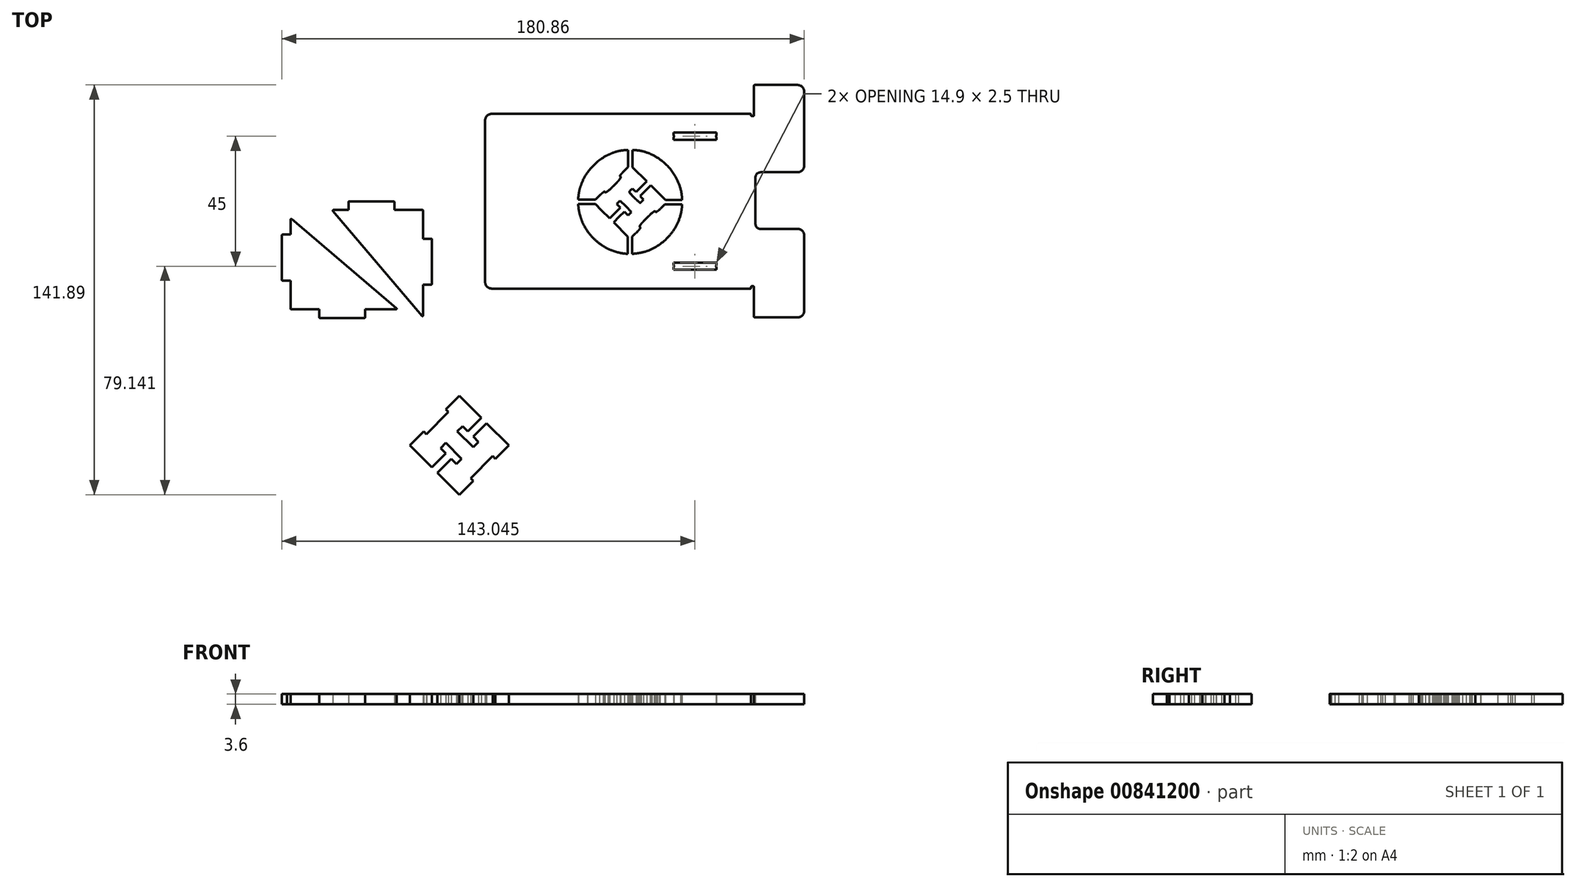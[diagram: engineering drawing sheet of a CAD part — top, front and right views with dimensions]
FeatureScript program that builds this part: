
annotation { "Feature Type Name" : "Feature", "Feature Type Description" : "" }
export const myFeature = defineFeature(function(context is Context, id is Id, definition is map)
    precondition{}
    {
        {
            assignVariable(context, id + "F0", {"name" : "Thickness", "anyValue" : 3.6});
        }
        {
            var Q0;
            Q0=qCreatedBy(makeId("Top.planeOp"),FACE);
            var sketch = newSketch(context, id + "F1", { "sketchPlane" : qUnion([Q0])});
            skLineSegment(sketch, "E0", {"start": v(-51.55, -47.18) * mm, "end": v(-51.61, -46.89) * mm});
            skArc(sketch, "E1", {"start": v(-51.61, -46.89) * mm, "mid": v(-51.65, -46.7) * mm, "end": v(-51.68, -46.5) * mm});
            skArc(sketch, "E2", {"start": v(-51.68, -46.5) * mm, "mid": v(-51.8, -45.73) * mm, "end": v(-51.89, -44.94) * mm});
            skArc(sketch, "E3", {"start": v(-51.89, -44.94) * mm, "mid": v(-51.9, -44.72) * mm, "end": v(-51.93, -44.5) * mm});
            skArc(sketch, "E4", {"start": v(-51.93, -44.5) * mm, "mid": v(-51.97, -43.8) * mm, "end": v(-52, -43.1) * mm});
            skLineSegment(sketch, "E5", {"start": v(-52, -43.1) * mm, "end": v(-44.28, -43.1) * mm});
            skLineSegment(sketch, "E6", {"start": v(-44.28, -43.1) * mm, "end": v(-41.3, -46.07) * mm});
            skLineSegment(sketch, "E7", {"start": v(-41.3, -46.07) * mm, "end": v(-37.5, -49.87) * mm});
            skLineSegment(sketch, "E8", {"start": v(-37.5, -49.87) * mm, "end": v(-35.03, -47.41) * mm});
            skLineSegment(sketch, "E9", {"start": v(-35.03, -47.41) * mm, "end": v(-32.57, -44.96) * mm});
            skLineSegment(sketch, "E10", {"start": v(-32.57, -44.96) * mm, "end": v(-33.4, -44.1) * mm});
            skLineSegment(sketch, "E11", {"start": v(-33.77, -43.73) * mm, "end": v(-34.58, -42.88) * mm});
            skLineSegment(sketch, "E12", {"start": v(-34.2, -43.25) * mm, "end": v(-33.54, -42.54) * mm});
            skArc(sketch, "E13", {"start": v(-33.54, -42.54) * mm, "mid": v(-33.33, -42.33) * mm, "end": v(-33.1, -42.13) * mm});
            skArc(sketch, "E14", {"start": v(-33.1, -42.13) * mm, "mid": v(-32.98, -42.04) * mm, "end": v(-32.86, -41.95) * mm});
            skLineSegment(sketch, "E15", {"start": v(-32.86, -41.95) * mm, "end": v(-32.8, -41.92) * mm});
            skLineSegment(sketch, "E16", {"start": v(-32.8, -41.92) * mm, "end": v(-32.77, -41.9) * mm});
            skArc(sketch, "E17", {"start": v(-32.77, -41.9) * mm, "mid": v(-32.72, -41.88) * mm, "end": v(-32.68, -41.86) * mm});
            skArc(sketch, "E18", {"start": v(-32.68, -41.86) * mm, "mid": v(-32.63, -41.84) * mm, "end": v(-32.58, -41.84) * mm});
            skLineSegment(sketch, "E19", {"start": v(-32.58, -41.84) * mm, "end": v(-32.53, -41.85) * mm});
            skArc(sketch, "E20", {"start": v(-32.53, -41.85) * mm, "mid": v(-32.43, -41.9) * mm, "end": v(-32.34, -41.97) * mm});
            skArc(sketch, "E21", {"start": v(-32.34, -41.97) * mm, "mid": v(-32.19, -42.08) * mm, "end": v(-32.04, -42.2) * mm});
            skLineSegment(sketch, "E22", {"start": v(-32.04, -42.2) * mm, "end": v(-32, -42.23) * mm});
            skLineSegment(sketch, "E23", {"start": v(-32, -42.23) * mm, "end": v(-31.86, -42.36) * mm});
            skLineSegment(sketch, "E24", {"start": v(-31.86, -42.36) * mm, "end": v(-31.79, -42.42) * mm});
            skLineSegment(sketch, "E25", {"start": v(-31.79, -42.42) * mm, "end": v(-31.72, -42.48) * mm});
            skLineSegment(sketch, "E26", {"start": v(-31.72, -42.48) * mm, "end": v(-31.44, -42.73) * mm});
            skLineSegment(sketch, "E27", {"start": v(-31.44, -42.73) * mm, "end": v(-31.18, -42.97) * mm});
            skArc(sketch, "E28", {"start": v(-31.18, -42.97) * mm, "mid": v(-30.7, -43.42) * mm, "end": v(-30.24, -43.88) * mm});
            skLineSegment(sketch, "E29", {"start": v(-30.24, -43.88) * mm, "end": v(-30.07, -44.05) * mm});
            skLineSegment(sketch, "E30", {"start": v(-30.07, -44.05) * mm, "end": v(-29.9, -44.21) * mm});
            skArc(sketch, "E31", {"start": v(-29.9, -44.21) * mm, "mid": v(-29.75, -44.36) * mm, "end": v(-29.6, -44.52) * mm});
            skLineSegment(sketch, "E32", {"start": v(-29.6, -44.52) * mm, "end": v(-29.33, -44.79) * mm});
            skLineSegment(sketch, "E33", {"start": v(-29.33, -44.79) * mm, "end": v(-29.1, -45.02) * mm});
            skLineSegment(sketch, "E34", {"start": v(-29.1, -45.02) * mm, "end": v(-28.9, -45.23) * mm});
            skLineSegment(sketch, "E35", {"start": v(-28.9, -45.23) * mm, "end": v(-28.56, -45.6) * mm});
            skLineSegment(sketch, "E36", {"start": v(-28.56, -45.6) * mm, "end": v(-28.3, -45.88) * mm});
            skLineSegment(sketch, "E37", {"start": v(-28.3, -45.88) * mm, "end": v(-28.11, -46.1) * mm});
            skLineSegment(sketch, "E38", {"start": v(-28.11, -46.1) * mm, "end": v(-28.04, -46.18) * mm});
            skLineSegment(sketch, "E39", {"start": v(-28.04, -46.18) * mm, "end": v(-28.03, -46.2) * mm});
            skArc(sketch, "E40", {"start": v(-28.03, -46.2) * mm, "mid": v(-27.98, -46.26) * mm, "end": v(-27.92, -46.32) * mm});
            skArc(sketch, "E41", {"start": v(-27.92, -46.32) * mm, "mid": v(-27.84, -46.43) * mm, "end": v(-27.75, -46.54) * mm});
            skArc(sketch, "E42", {"start": v(-27.75, -46.54) * mm, "mid": v(-27.71, -46.6) * mm, "end": v(-27.67, -46.66) * mm});
            skLineSegment(sketch, "E43", {"start": v(-27.67, -46.66) * mm, "end": v(-27.63, -46.86) * mm});
            skArc(sketch, "E44", {"start": v(-27.63, -46.86) * mm, "mid": v(-27.66, -46.93) * mm, "end": v(-27.69, -47) * mm});
            skLineSegment(sketch, "E45", {"start": v(-27.69, -47) * mm, "end": v(-27.72, -47.05) * mm});
            skArc(sketch, "E46", {"start": v(-27.72, -47.05) * mm, "mid": v(-27.85, -47.24) * mm, "end": v(-28, -47.43) * mm});
            skArc(sketch, "E47", {"start": v(-28, -47.43) * mm, "mid": v(-28.16, -47.6) * mm, "end": v(-28.32, -47.76) * mm});
            skLineSegment(sketch, "E48", {"start": v(-28.32, -47.76) * mm, "end": v(-29.03, -48.43) * mm});
            skLineSegment(sketch, "E49", {"start": v(-29.03, -48.43) * mm, "end": v(-29.88, -47.61) * mm});
            skLineSegment(sketch, "E50", {"start": v(-29.88, -47.61) * mm, "end": v(-30.74, -46.8) * mm});
            skLineSegment(sketch, "E51", {"start": v(-30.74, -46.8) * mm, "end": v(-33.2, -49.25) * mm});
            skLineSegment(sketch, "E52", {"start": v(-33.2, -49.25) * mm, "end": v(-35.65, -51.71) * mm});
            skLineSegment(sketch, "E53", {"start": v(-35.65, -51.71) * mm, "end": v(-31.85, -55.52) * mm});
            skLineSegment(sketch, "E54", {"start": v(-31.85, -55.52) * mm, "end": v(-29.1, -58.27) * mm});
            skLineSegment(sketch, "E55", {"start": v(-29.1, -58.27) * mm, "end": v(-29.1, -66.2) * mm});
            skArc(sketch, "E56", {"start": v(-29.1, -66.2) * mm, "mid": v(-29.86, -66.16) * mm, "end": v(-30.62, -66.11) * mm});
            skArc(sketch, "E57", {"start": v(-30.62, -66.11) * mm, "mid": v(-31.23, -66.05) * mm, "end": v(-31.83, -65.98) * mm});
            skArc(sketch, "E58", {"start": v(-31.83, -65.98) * mm, "mid": v(-32.16, -65.94) * mm, "end": v(-32.48, -65.89) * mm});
            skArc(sketch, "E59", {"start": v(-32.48, -65.89) * mm, "mid": v(-33.2, -65.75) * mm, "end": v(-33.93, -65.58) * mm});
            skArc(sketch, "E60", {"start": v(-33.93, -65.58) * mm, "mid": v(-36.24, -64.83) * mm, "end": v(-38.46, -63.86) * mm});
            skArc(sketch, "E61", {"start": v(-38.46, -63.86) * mm, "mid": v(-40.57, -62.67) * mm, "end": v(-42.56, -61.28) * mm});
            skArc(sketch, "E62", {"start": v(-42.56, -61.28) * mm, "mid": v(-46.08, -57.95) * mm, "end": v(-48.9, -54) * mm});
            skArc(sketch, "E63", {"start": v(-48.9, -54) * mm, "mid": v(-50.32, -51.1) * mm, "end": v(-51.35, -48.04) * mm});
            skLineSegment(sketch, "E64", {"start": v(-51.35, -48.04) * mm, "end": v(-51.43, -47.72) * mm});
            skLineSegment(sketch, "E65", {"start": v(-51.43, -47.72) * mm, "end": v(-51.5, -47.4) * mm});
            skLineSegment(sketch, "E66", {"start": v(-51.5, -47.4) * mm, "end": v(-51.52, -47.36) * mm});
            skArc(sketch, "E67", {"start": v(-51.52, -47.36) * mm, "mid": v(-51.53, -47.3) * mm, "end": v(-51.54, -47.24) * mm});
            skLineSegment(sketch, "E68", {"start": v(-51.54, -47.24) * mm, "end": v(-51.55, -47.18) * mm});
            skLineSegment(sketch, "E69", {"start": v(-28.2, -36.46) * mm, "end": v(-27.43, -35.69) * mm});
            skLineSegment(sketch, "E70", {"start": v(-27.06, -36.07) * mm, "end": v(-26.2, -36.9) * mm});
            skLineSegment(sketch, "E71", {"start": v(-26.2, -36.9) * mm, "end": v(-25.34, -37.72) * mm});
            skLineSegment(sketch, "E72", {"start": v(-25.34, -37.72) * mm, "end": v(-22.88, -35.26) * mm});
            skLineSegment(sketch, "E73", {"start": v(-22.92, -35.23) * mm, "end": v(-20.46, -32.77) * mm});
            skLineSegment(sketch, "E74", {"start": v(-20.42, -32.8) * mm, "end": v(-24.24, -29) * mm});
            skLineSegment(sketch, "E75", {"start": v(-24.23, -29) * mm, "end": v(-26.96, -26.25) * mm});
            skLineSegment(sketch, "E76", {"start": v(-26.96, -26.25) * mm, "end": v(-26.96, -18.25) * mm});
            skArc(sketch, "E77", {"start": v(-26.96, -18.25) * mm, "mid": v(-26.54, -18.27) * mm, "end": v(-26.12, -18.3) * mm});
            skArc(sketch, "E78", {"start": v(-26.12, -18.3) * mm, "mid": v(-23.87, -18.6) * mm, "end": v(-21.67, -19.11) * mm});
            skArc(sketch, "E79", {"start": v(-21.67, -19.11) * mm, "mid": v(-20.23, -19.58) * mm, "end": v(-18.82, -20.13) * mm});
            skArc(sketch, "E80", {"start": v(-18.82, -20.13) * mm, "mid": v(-17.01, -21) * mm, "end": v(-15.27, -22.02) * mm});
            skArc(sketch, "E81", {"start": v(-15.27, -22.02) * mm, "mid": v(-13.1, -23.6) * mm, "end": v(-11.1, -25.39) * mm});
            skArc(sketch, "E82", {"start": v(-11.1, -25.39) * mm, "mid": v(-8.77, -28.1) * mm, "end": v(-6.86, -31.1) * mm});
            skArc(sketch, "E83", {"start": v(-6.86, -31.1) * mm, "mid": v(-5.96, -32.94) * mm, "end": v(-5.23, -34.85) * mm});
            skArc(sketch, "E84", {"start": v(-5.23, -34.85) * mm, "mid": v(-4.6, -37.1) * mm, "end": v(-4.2, -39.4) * mm});
            skLineSegment(sketch, "E85", {"start": v(-4.2, -39.4) * mm, "end": v(-4.15, -39.74) * mm});
            skLineSegment(sketch, "E86", {"start": v(-4.15, -39.74) * mm, "end": v(-4.11, -40.09) * mm});
            skLineSegment(sketch, "E87", {"start": v(-4.11, -40.09) * mm, "end": v(-4.09, -40.32) * mm});
            skLineSegment(sketch, "E88", {"start": v(-4.09, -40.32) * mm, "end": v(-4.05, -40.63) * mm});
            skLineSegment(sketch, "E89", {"start": v(-4.05, -40.63) * mm, "end": v(-4.04, -40.81) * mm});
            skLineSegment(sketch, "E90", {"start": v(-4.04, -40.81) * mm, "end": v(-4.02, -41.02) * mm});
            skArc(sketch, "E91", {"start": v(-4.02, -41.02) * mm, "mid": v(-4, -41.15) * mm, "end": v(-4, -41.28) * mm});
            skLineSegment(sketch, "E92", {"start": v(-4, -41.28) * mm, "end": v(-11.95, -41.28) * mm});
            skLineSegment(sketch, "E93", {"start": v(-11.95, -41.28) * mm, "end": v(-14.77, -38.45) * mm});
            skLineSegment(sketch, "E94", {"start": v(-14.8, -38.42) * mm, "end": v(-18.62, -34.6) * mm});
            skLineSegment(sketch, "E95", {"start": v(-18.58, -34.64) * mm, "end": v(-21.04, -37.1) * mm});
            skLineSegment(sketch, "E96", {"start": v(-21.04, -37.1) * mm, "end": v(-23.5, -39.56) * mm});
            skLineSegment(sketch, "E97", {"start": v(-23.5, -39.56) * mm, "end": v(-22.68, -40.42) * mm});
            skLineSegment(sketch, "E98", {"start": v(-22.68, -40.42) * mm, "end": v(-21.85, -41.28) * mm});
            skLineSegment(sketch, "E99", {"start": v(-21.85, -41.28) * mm, "end": v(-22.62, -42.05) * mm});
            skLineSegment(sketch, "E100", {"start": v(-22.62, -42.05) * mm, "end": v(-23.39, -42.81) * mm});
            skLineSegment(sketch, "E101", {"start": v(-23.39, -42.81) * mm, "end": v(-26, -40.21) * mm});
            skLineSegment(sketch, "E102", {"start": v(-26, -40.21) * mm, "end": v(-28.6, -37.6) * mm});
            skLineSegment(sketch, "E103", {"start": v(-28.6, -37.6) * mm, "end": v(-27.83, -36.84) * mm});
            skArc(sketch, "E104", {"start": v(-26.67, -66.19) * mm, "mid": v(-26.1, -66.16) * mm, "end": v(-25.53, -66.12) * mm});
            skArc(sketch, "E105", {"start": v(-25.53, -66.12) * mm, "mid": v(-24.68, -66.04) * mm, "end": v(-23.83, -65.92) * mm});
            skArc(sketch, "E106", {"start": v(-23.83, -65.92) * mm, "mid": v(-23.4, -65.86) * mm, "end": v(-22.98, -65.78) * mm});
            skArc(sketch, "E107", {"start": v(-22.98, -65.78) * mm, "mid": v(-22.56, -65.69) * mm, "end": v(-22.15, -65.58) * mm});
            skArc(sketch, "E108", {"start": v(-22.15, -65.58) * mm, "mid": v(-21.29, -65.33) * mm, "end": v(-20.44, -65.05) * mm});
            skArc(sketch, "E109", {"start": v(-20.44, -65.05) * mm, "mid": v(-20.05, -64.9) * mm, "end": v(-19.66, -64.76) * mm});
            skArc(sketch, "E110", {"start": v(-19.66, -64.76) * mm, "mid": v(-18.17, -64.12) * mm, "end": v(-16.72, -63.38) * mm});
            skArc(sketch, "E111", {"start": v(-16.72, -63.38) * mm, "mid": v(-12.1, -60.09) * mm, "end": v(-8.35, -55.85) * mm});
            skArc(sketch, "E112", {"start": v(-8.35, -55.85) * mm, "mid": v(-8.3, -55.78) * mm, "end": v(-8.24, -55.7) * mm});
            skArc(sketch, "E113", {"start": v(-8.24, -55.7) * mm, "mid": v(-6.78, -53.32) * mm, "end": v(-5.6, -50.79) * mm});
            skArc(sketch, "E114", {"start": v(-5.6, -50.79) * mm, "mid": v(-5.13, -49.47) * mm, "end": v(-4.74, -48.13) * mm});
            skArc(sketch, "E115", {"start": v(-4.74, -48.13) * mm, "mid": v(-4.43, -46.76) * mm, "end": v(-4.2, -45.38) * mm});
            skArc(sketch, "E116", {"start": v(-4.2, -45.38) * mm, "mid": v(-4.2, -45.29) * mm, "end": v(-4.18, -45.2) * mm});
            skLineSegment(sketch, "E117", {"start": v(-4.18, -45.2) * mm, "end": v(-4.13, -44.83) * mm});
            skLineSegment(sketch, "E118", {"start": v(-4.13, -44.83) * mm, "end": v(-4.1, -44.5) * mm});
            skLineSegment(sketch, "E119", {"start": v(-4.1, -44.5) * mm, "end": v(-4.1, -44.5) * mm});
            skArc(sketch, "E120", {"start": v(-4.1, -44.5) * mm, "mid": v(-4.08, -44.33) * mm, "end": v(-4.06, -44.18) * mm});
            skLineSegment(sketch, "E121", {"start": v(-4.06, -44.18) * mm, "end": v(-4.03, -43.88) * mm});
            skLineSegment(sketch, "E122", {"start": v(-4.03, -43.88) * mm, "end": v(-4.02, -43.8) * mm});
            skArc(sketch, "E123", {"start": v(-4.02, -43.8) * mm, "mid": v(-4, -43.55) * mm, "end": v(-3.98, -43.28) * mm});
            skLineSegment(sketch, "E124", {"start": v(-3.98, -43.28) * mm, "end": v(-11.98, -43.28) * mm});
            skLineSegment(sketch, "E125", {"start": v(-11.98, -43.28) * mm, "end": v(-13.47, -44.76) * mm});
            skLineSegment(sketch, "E126", {"start": v(-13.47, -44.76) * mm, "end": v(-13.87, -45.16) * mm});
            skLineSegment(sketch, "E127", {"start": v(-13.87, -45.16) * mm, "end": v(-13.9, -45.18) * mm});
            skLineSegment(sketch, "E128", {"start": v(-13.9, -45.18) * mm, "end": v(-14, -45.29) * mm});
            skLineSegment(sketch, "E129", {"start": v(-14, -45.29) * mm, "end": v(-14.18, -45.46) * mm});
            skLineSegment(sketch, "E130", {"start": v(-14.18, -45.46) * mm, "end": v(-14.43, -45.69) * mm});
            skLineSegment(sketch, "E131", {"start": v(-14.43, -45.69) * mm, "end": v(-14.47, -45.73) * mm});
            skArc(sketch, "E132", {"start": v(-14.47, -45.73) * mm, "mid": v(-14.94, -46.15) * mm, "end": v(-15.43, -46.56) * mm});
            skArc(sketch, "E133", {"start": v(-15.43, -46.56) * mm, "mid": v(-15.5, -46.62) * mm, "end": v(-15.57, -46.67) * mm});
            skArc(sketch, "E134", {"start": v(-15.57, -46.67) * mm, "mid": v(-15.74, -46.79) * mm, "end": v(-15.9, -46.9) * mm});
            skArc(sketch, "E135", {"start": v(-15.9, -46.9) * mm, "mid": v(-15.96, -46.92) * mm, "end": v(-16, -46.94) * mm});
            skArc(sketch, "E136", {"start": v(-16, -46.94) * mm, "mid": v(-16.06, -46.96) * mm, "end": v(-16.11, -46.97) * mm});
            skLineSegment(sketch, "E137", {"start": v(-16.11, -46.97) * mm, "end": v(-16.17, -46.94) * mm});
            skArc(sketch, "E138", {"start": v(-16.17, -46.94) * mm, "mid": v(-16.25, -46.83) * mm, "end": v(-16.36, -46.73) * mm});
            skArc(sketch, "E139", {"start": v(-16.36, -46.73) * mm, "mid": v(-16.5, -46.68) * mm, "end": v(-16.64, -46.67) * mm});
            skArc(sketch, "E140", {"start": v(-16.64, -46.67) * mm, "mid": v(-16.74, -46.68) * mm, "end": v(-16.83, -46.7) * mm});
            skArc(sketch, "E141", {"start": v(-16.83, -46.7) * mm, "mid": v(-16.95, -46.75) * mm, "end": v(-17.07, -46.8) * mm});
            skArc(sketch, "E142", {"start": v(-17.07, -46.8) * mm, "mid": v(-17.2, -46.88) * mm, "end": v(-17.35, -46.96) * mm});
            skArc(sketch, "E143", {"start": v(-17.35, -46.96) * mm, "mid": v(-17.52, -47.08) * mm, "end": v(-17.69, -47.2) * mm});
            skLineSegment(sketch, "E144", {"start": v(-17.69, -47.2) * mm, "end": v(-17.87, -47.35) * mm});
            skArc(sketch, "E145", {"start": v(-17.87, -47.35) * mm, "mid": v(-18.1, -47.55) * mm, "end": v(-18.34, -47.75) * mm});
            skLineSegment(sketch, "E146", {"start": v(-18.34, -47.75) * mm, "end": v(-18.6, -47.98) * mm});
            skLineSegment(sketch, "E147", {"start": v(-18.6, -47.98) * mm, "end": v(-18.73, -48.1) * mm});
            skLineSegment(sketch, "E148", {"start": v(-18.73, -48.1) * mm, "end": v(-19.03, -48.38) * mm});
            skArc(sketch, "E149", {"start": v(-19.03, -48.38) * mm, "mid": v(-19.2, -48.55) * mm, "end": v(-19.38, -48.7) * mm});
            skLineSegment(sketch, "E150", {"start": v(-19.38, -48.7) * mm, "end": v(-19.56, -48.88) * mm});
            skArc(sketch, "E151", {"start": v(-19.56, -48.88) * mm, "mid": v(-20.03, -49.35) * mm, "end": v(-20.5, -49.81) * mm});
            skLineSegment(sketch, "E152", {"start": v(-20.5, -49.81) * mm, "end": v(-21.06, -50.38) * mm});
            skLineSegment(sketch, "E153", {"start": v(-21.06, -50.38) * mm, "end": v(-21.24, -50.57) * mm});
            skLineSegment(sketch, "E154", {"start": v(-21.24, -50.57) * mm, "end": v(-21.5, -50.82) * mm});
            skLineSegment(sketch, "E155", {"start": v(-21.5, -50.82) * mm, "end": v(-21.82, -51.17) * mm});
            skLineSegment(sketch, "E156", {"start": v(-21.82, -51.17) * mm, "end": v(-21.9, -51.26) * mm});
            skArc(sketch, "E157", {"start": v(-21.9, -51.26) * mm, "mid": v(-22.14, -51.5) * mm, "end": v(-22.37, -51.75) * mm});
            skArc(sketch, "E158", {"start": v(-22.37, -51.75) * mm, "mid": v(-22.67, -52.08) * mm, "end": v(-22.96, -52.43) * mm});
            skArc(sketch, "E159", {"start": v(-22.96, -52.43) * mm, "mid": v(-23.12, -52.63) * mm, "end": v(-23.27, -52.84) * mm});
            skArc(sketch, "E160", {"start": v(-23.27, -52.84) * mm, "mid": v(-23.35, -52.95) * mm, "end": v(-23.42, -53.07) * mm});
            skArc(sketch, "E161", {"start": v(-23.42, -53.07) * mm, "mid": v(-23.49, -53.2) * mm, "end": v(-23.55, -53.33) * mm});
            skArc(sketch, "E162", {"start": v(-23.55, -53.33) * mm, "mid": v(-23.6, -53.48) * mm, "end": v(-23.62, -53.64) * mm});
            skArc(sketch, "E163", {"start": v(-23.62, -53.64) * mm, "mid": v(-23.6, -53.82) * mm, "end": v(-23.51, -53.99) * mm});
            skArc(sketch, "E164", {"start": v(-23.51, -53.99) * mm, "mid": v(-23.45, -54.06) * mm, "end": v(-23.39, -54.14) * mm});
            skLineSegment(sketch, "E165", {"start": v(-23.39, -54.14) * mm, "end": v(-23.36, -54.26) * mm});
            skArc(sketch, "E166", {"start": v(-23.36, -54.26) * mm, "mid": v(-23.38, -54.31) * mm, "end": v(-23.4, -54.37) * mm});
            skArc(sketch, "E167", {"start": v(-23.4, -54.37) * mm, "mid": v(-23.46, -54.48) * mm, "end": v(-23.52, -54.58) * mm});
            skArc(sketch, "E168", {"start": v(-23.52, -54.58) * mm, "mid": v(-23.65, -54.77) * mm, "end": v(-23.8, -54.95) * mm});
            skArc(sketch, "E169", {"start": v(-23.8, -54.95) * mm, "mid": v(-24.08, -55.3) * mm, "end": v(-24.38, -55.64) * mm});
            skArc(sketch, "E170", {"start": v(-24.38, -55.64) * mm, "mid": v(-24.47, -55.73) * mm, "end": v(-24.56, -55.83) * mm});
            skLineSegment(sketch, "E171", {"start": v(-24.56, -55.83) * mm, "end": v(-24.76, -56.04) * mm});
            skLineSegment(sketch, "E172", {"start": v(-24.76, -56.04) * mm, "end": v(-25, -56.29) * mm});
            skLineSegment(sketch, "E173", {"start": v(-25, -56.29) * mm, "end": v(-25.27, -56.56) * mm});
            skArc(sketch, "E174", {"start": v(-25.27, -56.56) * mm, "mid": v(-25.42, -56.72) * mm, "end": v(-25.58, -56.87) * mm});
            skLineSegment(sketch, "E175", {"start": v(-25.58, -56.87) * mm, "end": v(-27.1, -58.39) * mm});
            skLineSegment(sketch, "E176", {"start": v(-27.1, -58.39) * mm, "end": v(-27.1, -66.2) * mm});
            skArc(sketch, "E177", {"start": v(-27.1, -66.2) * mm, "mid": v(-26.92, -66.2) * mm, "end": v(-26.75, -66.2) * mm});
            skLineSegment(sketch, "E178", {"start": v(-26.75, -66.2) * mm, "end": v(-26.67, -66.19) * mm});
            skLineSegment(sketch, "E179", {"start": v(-42.04, -39.2) * mm, "end": v(-42.12, -39.27) * mm});
            skLineSegment(sketch, "E180", {"start": v(-42.12, -39.27) * mm, "end": v(-42.38, -39.53) * mm});
            skLineSegment(sketch, "E181", {"start": v(-42.38, -39.53) * mm, "end": v(-42.65, -39.8) * mm});
            skLineSegment(sketch, "E182", {"start": v(-42.65, -39.8) * mm, "end": v(-43.94, -41.1) * mm});
            skLineSegment(sketch, "E183", {"start": v(-43.94, -41.1) * mm, "end": v(-52, -41.1) * mm});
            skArc(sketch, "E184", {"start": v(-52, -41.1) * mm, "mid": v(-51.99, -41) * mm, "end": v(-51.98, -40.9) * mm});
            skArc(sketch, "E185", {"start": v(-51.98, -40.9) * mm, "mid": v(-51.9, -39.71) * mm, "end": v(-51.76, -38.52) * mm});
            skArc(sketch, "E186", {"start": v(-51.76, -38.52) * mm, "mid": v(-51.74, -38.37) * mm, "end": v(-51.71, -38.22) * mm});
            skArc(sketch, "E187", {"start": v(-51.71, -38.22) * mm, "mid": v(-51.6, -37.52) * mm, "end": v(-51.44, -36.83) * mm});
            skArc(sketch, "E188", {"start": v(-51.44, -36.83) * mm, "mid": v(-51.4, -36.65) * mm, "end": v(-51.35, -36.48) * mm});
            skArc(sketch, "E189", {"start": v(-51.35, -36.48) * mm, "mid": v(-50.38, -33.55) * mm, "end": v(-49.04, -30.77) * mm});
            skArc(sketch, "E190", {"start": v(-49.04, -30.77) * mm, "mid": v(-47.37, -28.18) * mm, "end": v(-45.39, -25.81) * mm});
            skArc(sketch, "E191", {"start": v(-45.39, -25.81) * mm, "mid": v(-40.63, -21.9) * mm, "end": v(-35.05, -19.3) * mm});
            skArc(sketch, "E192", {"start": v(-35.05, -19.3) * mm, "mid": v(-34.7, -19.2) * mm, "end": v(-34.35, -19.1) * mm});
            skLineSegment(sketch, "E193", {"start": v(-34.35, -19.1) * mm, "end": v(-34.11, -19.04) * mm});
            skLineSegment(sketch, "E194", {"start": v(-34.11, -19.04) * mm, "end": v(-34.03, -19.02) * mm});
            skArc(sketch, "E195", {"start": v(-34.03, -19.02) * mm, "mid": v(-33.94, -19) * mm, "end": v(-33.85, -18.98) * mm});
            skLineSegment(sketch, "E196", {"start": v(-33.85, -18.98) * mm, "end": v(-33.8, -18.97) * mm});
            skLineSegment(sketch, "E197", {"start": v(-33.8, -18.97) * mm, "end": v(-33.37, -18.88) * mm});
            skLineSegment(sketch, "E198", {"start": v(-33.37, -18.88) * mm, "end": v(-33.28, -18.86) * mm});
            skArc(sketch, "E199", {"start": v(-33.28, -18.86) * mm, "mid": v(-33.2, -18.84) * mm, "end": v(-33.13, -18.83) * mm});
            skArc(sketch, "E200", {"start": v(-33.13, -18.83) * mm, "mid": v(-33.07, -18.81) * mm, "end": v(-33, -18.8) * mm});
            skLineSegment(sketch, "E201", {"start": v(-33, -18.8) * mm, "end": v(-32.86, -18.77) * mm});
            skLineSegment(sketch, "E202", {"start": v(-32.86, -18.77) * mm, "end": v(-32.81, -18.76) * mm});
            skArc(sketch, "E203", {"start": v(-32.81, -18.76) * mm, "mid": v(-31.73, -18.56) * mm, "end": v(-30.65, -18.4) * mm});
            skArc(sketch, "E204", {"start": v(-30.65, -18.4) * mm, "mid": v(-29.8, -18.32) * mm, "end": v(-28.97, -18.26) * mm});
            skLineSegment(sketch, "E205", {"start": v(-28.97, -18.26) * mm, "end": v(-28.97, -26.12) * mm});
            skLineSegment(sketch, "E206", {"start": v(-28.97, -26.12) * mm, "end": v(-30.5, -27.64) * mm});
            skArc(sketch, "E207", {"start": v(-30.5, -27.64) * mm, "mid": v(-30.65, -27.8) * mm, "end": v(-30.8, -27.96) * mm});
            skLineSegment(sketch, "E208", {"start": v(-30.8, -27.96) * mm, "end": v(-31.08, -28.23) * mm});
            skLineSegment(sketch, "E209", {"start": v(-31.08, -28.23) * mm, "end": v(-31.31, -28.47) * mm});
            skLineSegment(sketch, "E210", {"start": v(-31.31, -28.47) * mm, "end": v(-31.52, -28.69) * mm});
            skArc(sketch, "E211", {"start": v(-31.52, -28.69) * mm, "mid": v(-31.6, -28.78) * mm, "end": v(-31.7, -28.88) * mm});
            skArc(sketch, "E212", {"start": v(-31.7, -28.88) * mm, "mid": v(-32, -29.22) * mm, "end": v(-32.29, -29.57) * mm});
            skArc(sketch, "E213", {"start": v(-32.29, -29.57) * mm, "mid": v(-32.43, -29.75) * mm, "end": v(-32.56, -29.94) * mm});
            skArc(sketch, "E214", {"start": v(-32.56, -29.94) * mm, "mid": v(-32.62, -30.04) * mm, "end": v(-32.67, -30.15) * mm});
            skArc(sketch, "E215", {"start": v(-32.67, -30.15) * mm, "mid": v(-32.7, -30.2) * mm, "end": v(-32.71, -30.26) * mm});
            skLineSegment(sketch, "E216", {"start": v(-32.71, -30.26) * mm, "end": v(-32.7, -30.38) * mm});
            skArc(sketch, "E217", {"start": v(-32.7, -30.38) * mm, "mid": v(-32.62, -30.45) * mm, "end": v(-32.56, -30.53) * mm});
            skArc(sketch, "E218", {"start": v(-32.56, -30.53) * mm, "mid": v(-32.48, -30.7) * mm, "end": v(-32.46, -30.88) * mm});
            skArc(sketch, "E219", {"start": v(-32.46, -30.88) * mm, "mid": v(-32.48, -31.03) * mm, "end": v(-32.53, -31.19) * mm});
            skArc(sketch, "E220", {"start": v(-32.53, -31.19) * mm, "mid": v(-32.59, -31.32) * mm, "end": v(-32.66, -31.45) * mm});
            skArc(sketch, "E221", {"start": v(-32.66, -31.45) * mm, "mid": v(-32.73, -31.57) * mm, "end": v(-32.8, -31.68) * mm});
            skArc(sketch, "E222", {"start": v(-32.8, -31.68) * mm, "mid": v(-32.96, -31.89) * mm, "end": v(-33.12, -32.09) * mm});
            skArc(sketch, "E223", {"start": v(-33.12, -32.09) * mm, "mid": v(-33.4, -32.43) * mm, "end": v(-33.7, -32.77) * mm});
            skArc(sketch, "E224", {"start": v(-33.7, -32.77) * mm, "mid": v(-33.94, -33.01) * mm, "end": v(-34.17, -33.26) * mm});
            skLineSegment(sketch, "E225", {"start": v(-34.17, -33.26) * mm, "end": v(-34.26, -33.35) * mm});
            skLineSegment(sketch, "E226", {"start": v(-34.26, -33.35) * mm, "end": v(-34.58, -33.7) * mm});
            skLineSegment(sketch, "E227", {"start": v(-34.58, -33.7) * mm, "end": v(-34.83, -33.95) * mm});
            skLineSegment(sketch, "E228", {"start": v(-34.83, -33.95) * mm, "end": v(-35.02, -34.14) * mm});
            skLineSegment(sketch, "E229", {"start": v(-35.02, -34.14) * mm, "end": v(-35.58, -34.7) * mm});
            skLineSegment(sketch, "E230", {"start": v(-35.58, -34.7) * mm, "end": v(-35.7, -34.82) * mm});
            skLineSegment(sketch, "E231", {"start": v(-35.7, -34.82) * mm, "end": v(-36.16, -35.28) * mm});
            skLineSegment(sketch, "E232", {"start": v(-36.16, -35.28) * mm, "end": v(-36.26, -35.37) * mm});
            skLineSegment(sketch, "E233", {"start": v(-36.26, -35.37) * mm, "end": v(-36.35, -35.47) * mm});
            skLineSegment(sketch, "E234", {"start": v(-36.35, -35.47) * mm, "end": v(-36.45, -35.56) * mm});
            skLineSegment(sketch, "E235", {"start": v(-36.45, -35.56) * mm, "end": v(-36.54, -35.65) * mm});
            skArc(sketch, "E236", {"start": v(-36.54, -35.65) * mm, "mid": v(-36.9, -36) * mm, "end": v(-37.26, -36.35) * mm});
            skLineSegment(sketch, "E237", {"start": v(-37.26, -36.35) * mm, "end": v(-37.54, -36.6) * mm});
            skLineSegment(sketch, "E238", {"start": v(-37.54, -36.6) * mm, "end": v(-37.8, -36.83) * mm});
            skLineSegment(sketch, "E239", {"start": v(-37.8, -36.83) * mm, "end": v(-38.02, -37.03) * mm});
            skLineSegment(sketch, "E240", {"start": v(-38.02, -37.03) * mm, "end": v(-38.22, -37.2) * mm});
            skArc(sketch, "E241", {"start": v(-38.22, -37.2) * mm, "mid": v(-38.4, -37.34) * mm, "end": v(-38.6, -37.48) * mm});
            skArc(sketch, "E242", {"start": v(-38.6, -37.48) * mm, "mid": v(-38.74, -37.58) * mm, "end": v(-38.9, -37.67) * mm});
            skArc(sketch, "E243", {"start": v(-38.9, -37.67) * mm, "mid": v(-39.02, -37.73) * mm, "end": v(-39.15, -37.79) * mm});
            skArc(sketch, "E244", {"start": v(-39.15, -37.79) * mm, "mid": v(-39.25, -37.82) * mm, "end": v(-39.35, -37.83) * mm});
            skArc(sketch, "E245", {"start": v(-39.35, -37.83) * mm, "mid": v(-39.5, -37.83) * mm, "end": v(-39.66, -37.79) * mm});
            skArc(sketch, "E246", {"start": v(-39.66, -37.79) * mm, "mid": v(-39.8, -37.7) * mm, "end": v(-39.92, -37.6) * mm});
            skLineSegment(sketch, "E247", {"start": v(-39.92, -37.6) * mm, "end": v(-39.97, -37.58) * mm});
            skArc(sketch, "E248", {"start": v(-39.97, -37.58) * mm, "mid": v(-40.03, -37.58) * mm, "end": v(-40.08, -37.6) * mm});
            skArc(sketch, "E249", {"start": v(-40.08, -37.6) * mm, "mid": v(-40.13, -37.61) * mm, "end": v(-40.18, -37.64) * mm});
            skLineSegment(sketch, "E250", {"start": v(-40.18, -37.64) * mm, "end": v(-40.23, -37.66) * mm});
            skLineSegment(sketch, "E251", {"start": v(-40.23, -37.66) * mm, "end": v(-40.31, -37.71) * mm});
            skArc(sketch, "E252", {"start": v(-40.31, -37.71) * mm, "mid": v(-40.4, -37.77) * mm, "end": v(-40.48, -37.82) * mm});
            skLineSegment(sketch, "E253", {"start": v(-40.48, -37.82) * mm, "end": v(-40.55, -37.87) * mm});
            skLineSegment(sketch, "E254", {"start": v(-40.55, -37.87) * mm, "end": v(-40.6, -37.9) * mm});
            skArc(sketch, "E255", {"start": v(-40.6, -37.9) * mm, "mid": v(-40.61, -37.92) * mm, "end": v(-40.62, -37.93) * mm});
            skArc(sketch, "E256", {"start": v(-40.62, -37.93) * mm, "mid": v(-40.9, -38.14) * mm, "end": v(-41.15, -38.37) * mm});
            skLineSegment(sketch, "E257", {"start": v(-41.15, -38.37) * mm, "end": v(-41.2, -38.41) * mm});
            skLineSegment(sketch, "E258", {"start": v(-41.2, -38.41) * mm, "end": v(-41.39, -38.58) * mm});
            skLineSegment(sketch, "E259", {"start": v(-41.39, -38.58) * mm, "end": v(-41.71, -38.88) * mm});
            skLineSegment(sketch, "E260", {"start": v(-41.71, -38.88) * mm, "end": v(-41.95, -39.1) * mm});
            skLineSegment(sketch, "E261", {"start": v(-41.95, -39.1) * mm, "end": v(-42.04, -39.2) * mm});
            skLineSegment(sketch, "E262", {"start": v(48.77, 45.74) * mm, "end": v(48.8, 45.52) * mm});
            skArc(sketch, "E263", {"start": v(48.8, 45.52) * mm, "mid": v(48.84, 45.38) * mm, "end": v(48.86, 45.23) * mm});
            skArc(sketch, "E264", {"start": v(48.86, 45.23) * mm, "mid": v(48.95, 44.65) * mm, "end": v(49.02, 44.06) * mm});
            skArc(sketch, "E265", {"start": v(49.02, 44.06) * mm, "mid": v(49.03, 43.9) * mm, "end": v(49.05, 43.73) * mm});
            skArc(sketch, "E266", {"start": v(49.05, 43.73) * mm, "mid": v(49.08, 43.2) * mm, "end": v(49.1, 42.68) * mm});
            skLineSegment(sketch, "E267", {"start": v(49.1, 42.68) * mm, "end": v(43.3, 42.68) * mm});
            skLineSegment(sketch, "E268", {"start": v(43.3, 42.68) * mm, "end": v(41.08, 44.9) * mm});
            skLineSegment(sketch, "E269", {"start": v(41.08, 44.9) * mm, "end": v(38.22, 47.76) * mm});
            skLineSegment(sketch, "E270", {"start": v(38.22, 47.76) * mm, "end": v(36.37, 45.92) * mm});
            skLineSegment(sketch, "E271", {"start": v(36.37, 45.92) * mm, "end": v(34.53, 44.07) * mm});
            skLineSegment(sketch, "E272", {"start": v(34.53, 44.07) * mm, "end": v(35.14, 43.43) * mm});
            skLineSegment(sketch, "E273", {"start": v(35.14, 43.43) * mm, "end": v(35.76, 42.8) * mm});
            skLineSegment(sketch, "E274", {"start": v(35.76, 42.8) * mm, "end": v(35.26, 42.26) * mm});
            skArc(sketch, "E275", {"start": v(35.26, 42.26) * mm, "mid": v(35.1, 42.1) * mm, "end": v(34.93, 41.96) * mm});
            skArc(sketch, "E276", {"start": v(34.93, 41.96) * mm, "mid": v(34.84, 41.89) * mm, "end": v(34.74, 41.82) * mm});
            skLineSegment(sketch, "E277", {"start": v(34.74, 41.82) * mm, "end": v(34.7, 41.8) * mm});
            skLineSegment(sketch, "E278", {"start": v(34.7, 41.8) * mm, "end": v(34.68, 41.78) * mm});
            skArc(sketch, "E279", {"start": v(34.68, 41.78) * mm, "mid": v(34.64, 41.77) * mm, "end": v(34.6, 41.75) * mm});
            skArc(sketch, "E280", {"start": v(34.6, 41.75) * mm, "mid": v(34.57, 41.74) * mm, "end": v(34.54, 41.73) * mm});
            skLineSegment(sketch, "E281", {"start": v(34.54, 41.73) * mm, "end": v(34.5, 41.74) * mm});
            skArc(sketch, "E282", {"start": v(34.5, 41.74) * mm, "mid": v(34.42, 41.78) * mm, "end": v(34.36, 41.83) * mm});
            skArc(sketch, "E283", {"start": v(34.36, 41.83) * mm, "mid": v(34.24, 41.92) * mm, "end": v(34.13, 42) * mm});
            skLineSegment(sketch, "E284", {"start": v(34.13, 42) * mm, "end": v(34.1, 42.03) * mm});
            skLineSegment(sketch, "E285", {"start": v(34.1, 42.03) * mm, "end": v(34, 42.13) * mm});
            skLineSegment(sketch, "E286", {"start": v(34, 42.13) * mm, "end": v(33.94, 42.17) * mm});
            skLineSegment(sketch, "E287", {"start": v(33.94, 42.17) * mm, "end": v(33.89, 42.22) * mm});
            skLineSegment(sketch, "E288", {"start": v(33.89, 42.22) * mm, "end": v(33.68, 42.4) * mm});
            skLineSegment(sketch, "E289", {"start": v(33.68, 42.4) * mm, "end": v(33.49, 42.58) * mm});
            skArc(sketch, "E290", {"start": v(33.49, 42.58) * mm, "mid": v(33.13, 42.92) * mm, "end": v(32.78, 43.26) * mm});
            skLineSegment(sketch, "E291", {"start": v(32.78, 43.26) * mm, "end": v(32.65, 43.4) * mm});
            skLineSegment(sketch, "E292", {"start": v(32.65, 43.4) * mm, "end": v(32.53, 43.51) * mm});
            skArc(sketch, "E293", {"start": v(32.53, 43.51) * mm, "mid": v(32.41, 43.63) * mm, "end": v(32.3, 43.74) * mm});
            skLineSegment(sketch, "E294", {"start": v(32.3, 43.74) * mm, "end": v(32.1, 43.95) * mm});
            skLineSegment(sketch, "E295", {"start": v(32.1, 43.95) * mm, "end": v(31.93, 44.12) * mm});
            skLineSegment(sketch, "E296", {"start": v(31.93, 44.12) * mm, "end": v(31.78, 44.28) * mm});
            skLineSegment(sketch, "E297", {"start": v(31.78, 44.28) * mm, "end": v(31.52, 44.56) * mm});
            skLineSegment(sketch, "E298", {"start": v(31.52, 44.56) * mm, "end": v(31.33, 44.77) * mm});
            skLineSegment(sketch, "E299", {"start": v(31.33, 44.77) * mm, "end": v(31.19, 44.93) * mm});
            skLineSegment(sketch, "E300", {"start": v(31.19, 44.93) * mm, "end": v(31.13, 45) * mm});
            skLineSegment(sketch, "E301", {"start": v(31.13, 45) * mm, "end": v(31.12, 45) * mm});
            skArc(sketch, "E302", {"start": v(31.12, 45) * mm, "mid": v(31.08, 45.05) * mm, "end": v(31.04, 45.1) * mm});
            skArc(sketch, "E303", {"start": v(31.04, 45.1) * mm, "mid": v(30.98, 45.18) * mm, "end": v(30.91, 45.26) * mm});
            skArc(sketch, "E304", {"start": v(30.91, 45.26) * mm, "mid": v(30.88, 45.3) * mm, "end": v(30.85, 45.35) * mm});
            skLineSegment(sketch, "E305", {"start": v(30.85, 45.35) * mm, "end": v(30.82, 45.5) * mm});
            skArc(sketch, "E306", {"start": v(30.82, 45.5) * mm, "mid": v(30.84, 45.56) * mm, "end": v(30.87, 45.6) * mm});
            skLineSegment(sketch, "E307", {"start": v(30.87, 45.6) * mm, "end": v(30.9, 45.64) * mm});
            skArc(sketch, "E308", {"start": v(30.9, 45.64) * mm, "mid": v(30.99, 45.79) * mm, "end": v(31.1, 45.93) * mm});
            skArc(sketch, "E309", {"start": v(31.1, 45.93) * mm, "mid": v(31.22, 46.06) * mm, "end": v(31.34, 46.18) * mm});
            skLineSegment(sketch, "E310", {"start": v(31.34, 46.18) * mm, "end": v(31.87, 46.68) * mm});
            skLineSegment(sketch, "E311", {"start": v(31.87, 46.68) * mm, "end": v(32.51, 46.07) * mm});
            skLineSegment(sketch, "E312", {"start": v(32.51, 46.07) * mm, "end": v(33.15, 45.45) * mm});
            skLineSegment(sketch, "E313", {"start": v(33.15, 45.45) * mm, "end": v(35, 47.3) * mm});
            skLineSegment(sketch, "E314", {"start": v(35, 47.3) * mm, "end": v(36.84, 49.14) * mm});
            skLineSegment(sketch, "E315", {"start": v(36.84, 49.14) * mm, "end": v(33.99, 52) * mm});
            skLineSegment(sketch, "E316", {"start": v(33.99, 52) * mm, "end": v(31.93, 54.06) * mm});
            skLineSegment(sketch, "E317", {"start": v(31.93, 54.06) * mm, "end": v(31.93, 60) * mm});
            skArc(sketch, "E318", {"start": v(31.93, 60) * mm, "mid": v(32.5, 59.98) * mm, "end": v(33.07, 59.94) * mm});
            skArc(sketch, "E319", {"start": v(33.07, 59.94) * mm, "mid": v(33.52, 59.9) * mm, "end": v(33.98, 59.84) * mm});
            skArc(sketch, "E320", {"start": v(33.98, 59.84) * mm, "mid": v(34.22, 59.81) * mm, "end": v(34.46, 59.77) * mm});
            skArc(sketch, "E321", {"start": v(34.46, 59.77) * mm, "mid": v(35, 59.67) * mm, "end": v(35.55, 59.54) * mm});
            skArc(sketch, "E322", {"start": v(35.55, 59.54) * mm, "mid": v(37.28, 58.98) * mm, "end": v(38.95, 58.25) * mm});
            skArc(sketch, "E323", {"start": v(38.95, 58.25) * mm, "mid": v(40.53, 57.36) * mm, "end": v(42.02, 56.32) * mm});
            skArc(sketch, "E324", {"start": v(42.02, 56.32) * mm, "mid": v(44.66, 53.82) * mm, "end": v(46.77, 50.86) * mm});
            skArc(sketch, "E325", {"start": v(46.77, 50.86) * mm, "mid": v(47.84, 48.69) * mm, "end": v(48.61, 46.39) * mm});
            skLineSegment(sketch, "E326", {"start": v(48.61, 46.39) * mm, "end": v(48.68, 46.15) * mm});
            skLineSegment(sketch, "E327", {"start": v(48.68, 46.15) * mm, "end": v(48.73, 45.9) * mm});
            skLineSegment(sketch, "E328", {"start": v(48.73, 45.9) * mm, "end": v(48.74, 45.88) * mm});
            skArc(sketch, "E329", {"start": v(48.74, 45.88) * mm, "mid": v(48.75, 45.83) * mm, "end": v(48.76, 45.78) * mm});
            skLineSegment(sketch, "E330", {"start": v(48.76, 45.78) * mm, "end": v(48.77, 45.74) * mm});
            skLineSegment(sketch, "E331", {"start": v(30.97, 37.99) * mm, "end": v(30.4, 37.41) * mm});
            skLineSegment(sketch, "E332", {"start": v(30.4, 37.41) * mm, "end": v(29.75, 38.03) * mm});
            skLineSegment(sketch, "E333", {"start": v(29.75, 38.03) * mm, "end": v(29.1, 38.65) * mm});
            skLineSegment(sketch, "E334", {"start": v(29.1, 38.65) * mm, "end": v(27.26, 36.8) * mm});
            skLineSegment(sketch, "E335", {"start": v(27.26, 36.8) * mm, "end": v(25.42, 34.96) * mm});
            skLineSegment(sketch, "E336", {"start": v(25.42, 34.96) * mm, "end": v(28.27, 32.1) * mm});
            skLineSegment(sketch, "E337", {"start": v(28.27, 32.1) * mm, "end": v(30.32, 30.05) * mm});
            skLineSegment(sketch, "E338", {"start": v(30.32, 30.05) * mm, "end": v(30.32, 24.05) * mm});
            skArc(sketch, "E339", {"start": v(30.32, 24.05) * mm, "mid": v(30, 24.06) * mm, "end": v(29.7, 24.08) * mm});
            skArc(sketch, "E340", {"start": v(29.7, 24.08) * mm, "mid": v(28, 24.3) * mm, "end": v(26.35, 24.7) * mm});
            skArc(sketch, "E341", {"start": v(26.35, 24.7) * mm, "mid": v(25.27, 25.04) * mm, "end": v(24.22, 25.45) * mm});
            skArc(sketch, "E342", {"start": v(24.22, 25.45) * mm, "mid": v(22.86, 26.1) * mm, "end": v(21.56, 26.87) * mm});
            skArc(sketch, "E343", {"start": v(21.56, 26.87) * mm, "mid": v(19.93, 28.05) * mm, "end": v(18.43, 29.4) * mm});
            skArc(sketch, "E344", {"start": v(18.43, 29.4) * mm, "mid": v(16.68, 31.42) * mm, "end": v(15.24, 33.68) * mm});
            skArc(sketch, "E345", {"start": v(15.24, 33.68) * mm, "mid": v(14.57, 35.06) * mm, "end": v(14.02, 36.5) * mm});
            skArc(sketch, "E346", {"start": v(14.02, 36.5) * mm, "mid": v(13.55, 38.18) * mm, "end": v(13.25, 39.9) * mm});
            skLineSegment(sketch, "E347", {"start": v(13.25, 39.9) * mm, "end": v(13.21, 40.16) * mm});
            skLineSegment(sketch, "E348", {"start": v(13.21, 40.16) * mm, "end": v(13.18, 40.42) * mm});
            skLineSegment(sketch, "E349", {"start": v(13.18, 40.42) * mm, "end": v(13.16, 40.6) * mm});
            skLineSegment(sketch, "E350", {"start": v(13.16, 40.6) * mm, "end": v(13.14, 40.83) * mm});
            skLineSegment(sketch, "E351", {"start": v(13.14, 40.83) * mm, "end": v(13.13, 40.97) * mm});
            skLineSegment(sketch, "E352", {"start": v(13.13, 40.97) * mm, "end": v(13.11, 41.12) * mm});
            skArc(sketch, "E353", {"start": v(13.11, 41.12) * mm, "mid": v(13.1, 41.22) * mm, "end": v(13.1, 41.32) * mm});
            skLineSegment(sketch, "E354", {"start": v(13.1, 41.32) * mm, "end": v(19.06, 41.32) * mm});
            skLineSegment(sketch, "E355", {"start": v(19.06, 41.32) * mm, "end": v(21.18, 39.2) * mm});
            skLineSegment(sketch, "E356", {"start": v(21.18, 39.2) * mm, "end": v(24.04, 36.34) * mm});
            skLineSegment(sketch, "E357", {"start": v(24.04, 36.34) * mm, "end": v(25.88, 38.18) * mm});
            skLineSegment(sketch, "E358", {"start": v(25.88, 38.18) * mm, "end": v(27.73, 40.03) * mm});
            skLineSegment(sketch, "E359", {"start": v(27.73, 40.03) * mm, "end": v(27.1, 40.67) * mm});
            skLineSegment(sketch, "E360", {"start": v(27.1, 40.67) * mm, "end": v(26.5, 41.32) * mm});
            skLineSegment(sketch, "E361", {"start": v(26.5, 41.32) * mm, "end": v(27.07, 41.9) * mm});
            skLineSegment(sketch, "E362", {"start": v(27.07, 41.9) * mm, "end": v(27.64, 42.47) * mm});
            skLineSegment(sketch, "E363", {"start": v(27.64, 42.47) * mm, "end": v(29.6, 40.51) * mm});
            skLineSegment(sketch, "E364", {"start": v(29.6, 40.51) * mm, "end": v(31.55, 38.56) * mm});
            skLineSegment(sketch, "E365", {"start": v(31.55, 38.56) * mm, "end": v(30.97, 37.99) * mm});
            skArc(sketch, "E366", {"start": v(30.1, 60) * mm, "mid": v(29.68, 59.98) * mm, "end": v(29.25, 59.95) * mm});
            skArc(sketch, "E367", {"start": v(29.25, 59.95) * mm, "mid": v(28.6, 59.88) * mm, "end": v(27.97, 59.8) * mm});
            skArc(sketch, "E368", {"start": v(27.97, 59.8) * mm, "mid": v(27.65, 59.75) * mm, "end": v(27.34, 59.69) * mm});
            skArc(sketch, "E369", {"start": v(27.34, 59.69) * mm, "mid": v(27.02, 59.62) * mm, "end": v(26.71, 59.54) * mm});
            skArc(sketch, "E370", {"start": v(26.71, 59.54) * mm, "mid": v(26.07, 59.36) * mm, "end": v(25.43, 59.15) * mm});
            skArc(sketch, "E371", {"start": v(25.43, 59.15) * mm, "mid": v(25.14, 59.04) * mm, "end": v(24.84, 58.93) * mm});
            skArc(sketch, "E372", {"start": v(24.84, 58.93) * mm, "mid": v(23.73, 58.45) * mm, "end": v(22.64, 57.9) * mm});
            skArc(sketch, "E373", {"start": v(22.64, 57.9) * mm, "mid": v(19.18, 55.42) * mm, "end": v(16.36, 52.25) * mm});
            skArc(sketch, "E374", {"start": v(16.36, 52.25) * mm, "mid": v(16.32, 52.2) * mm, "end": v(16.28, 52.14) * mm});
            skArc(sketch, "E375", {"start": v(16.28, 52.14) * mm, "mid": v(15.19, 50.35) * mm, "end": v(14.3, 48.45) * mm});
            skArc(sketch, "E376", {"start": v(14.3, 48.45) * mm, "mid": v(13.95, 47.46) * mm, "end": v(13.65, 46.45) * mm});
            skArc(sketch, "E377", {"start": v(13.65, 46.45) * mm, "mid": v(13.42, 45.43) * mm, "end": v(13.25, 44.4) * mm});
            skArc(sketch, "E378", {"start": v(13.25, 44.4) * mm, "mid": v(13.24, 44.32) * mm, "end": v(13.24, 44.25) * mm});
            skLineSegment(sketch, "E379", {"start": v(13.24, 44.25) * mm, "end": v(13.2, 43.98) * mm});
            skLineSegment(sketch, "E380", {"start": v(13.2, 43.98) * mm, "end": v(13.17, 43.73) * mm});
            skLineSegment(sketch, "E381", {"start": v(13.17, 43.73) * mm, "end": v(13.17, 43.73) * mm});
            skArc(sketch, "E382", {"start": v(13.17, 43.73) * mm, "mid": v(13.16, 43.6) * mm, "end": v(13.15, 43.49) * mm});
            skLineSegment(sketch, "E383", {"start": v(13.15, 43.49) * mm, "end": v(13.12, 43.27) * mm});
            skLineSegment(sketch, "E384", {"start": v(13.12, 43.27) * mm, "end": v(13.12, 43.21) * mm});
            skArc(sketch, "E385", {"start": v(13.12, 43.21) * mm, "mid": v(13.1, 43.02) * mm, "end": v(13.09, 42.82) * mm});
            skLineSegment(sketch, "E386", {"start": v(13.09, 42.82) * mm, "end": v(19.09, 42.82) * mm});
            skLineSegment(sketch, "E387", {"start": v(19.09, 42.82) * mm, "end": v(20.2, 43.93) * mm});
            skLineSegment(sketch, "E388", {"start": v(20.2, 43.93) * mm, "end": v(20.5, 44.22) * mm});
            skLineSegment(sketch, "E389", {"start": v(20.5, 44.22) * mm, "end": v(20.52, 44.24) * mm});
            skLineSegment(sketch, "E390", {"start": v(20.52, 44.24) * mm, "end": v(20.6, 44.32) * mm});
            skLineSegment(sketch, "E391", {"start": v(20.6, 44.32) * mm, "end": v(20.74, 44.45) * mm});
            skLineSegment(sketch, "E392", {"start": v(20.74, 44.45) * mm, "end": v(20.92, 44.62) * mm});
            skLineSegment(sketch, "E393", {"start": v(20.92, 44.62) * mm, "end": v(20.95, 44.65) * mm});
            skArc(sketch, "E394", {"start": v(20.95, 44.65) * mm, "mid": v(21.3, 44.97) * mm, "end": v(21.67, 45.28) * mm});
            skArc(sketch, "E395", {"start": v(21.67, 45.28) * mm, "mid": v(21.73, 45.32) * mm, "end": v(21.78, 45.36) * mm});
            skArc(sketch, "E396", {"start": v(21.78, 45.36) * mm, "mid": v(21.9, 45.45) * mm, "end": v(22.03, 45.53) * mm});
            skArc(sketch, "E397", {"start": v(22.03, 45.53) * mm, "mid": v(22.07, 45.55) * mm, "end": v(22.1, 45.56) * mm});
            skArc(sketch, "E398", {"start": v(22.1, 45.56) * mm, "mid": v(22.14, 45.58) * mm, "end": v(22.18, 45.58) * mm});
            skLineSegment(sketch, "E399", {"start": v(22.18, 45.58) * mm, "end": v(22.23, 45.57) * mm});
            skArc(sketch, "E400", {"start": v(22.23, 45.57) * mm, "mid": v(22.29, 45.48) * mm, "end": v(22.37, 45.4) * mm});
            skArc(sketch, "E401", {"start": v(22.37, 45.4) * mm, "mid": v(22.47, 45.36) * mm, "end": v(22.58, 45.36) * mm});
            skArc(sketch, "E402", {"start": v(22.58, 45.36) * mm, "mid": v(22.65, 45.37) * mm, "end": v(22.73, 45.38) * mm});
            skArc(sketch, "E403", {"start": v(22.73, 45.38) * mm, "mid": v(22.81, 45.42) * mm, "end": v(22.9, 45.46) * mm});
            skArc(sketch, "E404", {"start": v(22.9, 45.46) * mm, "mid": v(23, 45.51) * mm, "end": v(23.11, 45.58) * mm});
            skArc(sketch, "E405", {"start": v(23.11, 45.58) * mm, "mid": v(23.24, 45.67) * mm, "end": v(23.37, 45.76) * mm});
            skLineSegment(sketch, "E406", {"start": v(23.37, 45.76) * mm, "end": v(23.5, 45.87) * mm});
            skArc(sketch, "E407", {"start": v(23.5, 45.87) * mm, "mid": v(23.68, 46.02) * mm, "end": v(23.86, 46.17) * mm});
            skLineSegment(sketch, "E408", {"start": v(23.86, 46.17) * mm, "end": v(24.05, 46.34) * mm});
            skLineSegment(sketch, "E409", {"start": v(24.05, 46.34) * mm, "end": v(24.15, 46.43) * mm});
            skLineSegment(sketch, "E410", {"start": v(24.15, 46.43) * mm, "end": v(24.38, 46.64) * mm});
            skArc(sketch, "E411", {"start": v(24.38, 46.64) * mm, "mid": v(24.5, 46.77) * mm, "end": v(24.63, 46.89) * mm});
            skLineSegment(sketch, "E412", {"start": v(24.63, 46.89) * mm, "end": v(24.77, 47.02) * mm});
            skArc(sketch, "E413", {"start": v(24.77, 47.02) * mm, "mid": v(25.12, 47.37) * mm, "end": v(25.47, 47.72) * mm});
            skLineSegment(sketch, "E414", {"start": v(25.47, 47.72) * mm, "end": v(25.9, 48.14) * mm});
            skLineSegment(sketch, "E415", {"start": v(25.9, 48.14) * mm, "end": v(26.03, 48.28) * mm});
            skLineSegment(sketch, "E416", {"start": v(26.03, 48.28) * mm, "end": v(26.22, 48.48) * mm});
            skLineSegment(sketch, "E417", {"start": v(26.22, 48.48) * mm, "end": v(26.47, 48.73) * mm});
            skLineSegment(sketch, "E418", {"start": v(26.47, 48.73) * mm, "end": v(26.53, 48.8) * mm});
            skArc(sketch, "E419", {"start": v(26.53, 48.8) * mm, "mid": v(26.7, 48.98) * mm, "end": v(26.88, 49.17) * mm});
            skArc(sketch, "E420", {"start": v(26.88, 49.17) * mm, "mid": v(27.1, 49.42) * mm, "end": v(27.32, 49.68) * mm});
            skArc(sketch, "E421", {"start": v(27.32, 49.68) * mm, "mid": v(27.44, 49.83) * mm, "end": v(27.55, 49.98) * mm});
            skArc(sketch, "E422", {"start": v(27.55, 49.98) * mm, "mid": v(27.61, 50.07) * mm, "end": v(27.66, 50.16) * mm});
            skArc(sketch, "E423", {"start": v(27.66, 50.16) * mm, "mid": v(27.72, 50.25) * mm, "end": v(27.76, 50.35) * mm});
            skArc(sketch, "E424", {"start": v(27.76, 50.35) * mm, "mid": v(27.8, 50.47) * mm, "end": v(27.81, 50.59) * mm});
            skArc(sketch, "E425", {"start": v(27.81, 50.59) * mm, "mid": v(27.8, 50.72) * mm, "end": v(27.73, 50.85) * mm});
            skArc(sketch, "E426", {"start": v(27.73, 50.85) * mm, "mid": v(27.7, 50.9) * mm, "end": v(27.64, 50.96) * mm});
            skLineSegment(sketch, "E427", {"start": v(27.64, 50.96) * mm, "end": v(27.62, 51.05) * mm});
            skArc(sketch, "E428", {"start": v(27.62, 51.05) * mm, "mid": v(27.64, 51.1) * mm, "end": v(27.65, 51.14) * mm});
            skArc(sketch, "E429", {"start": v(27.65, 51.14) * mm, "mid": v(27.7, 51.21) * mm, "end": v(27.74, 51.29) * mm});
            skArc(sketch, "E430", {"start": v(27.74, 51.29) * mm, "mid": v(27.84, 51.43) * mm, "end": v(27.94, 51.57) * mm});
            skArc(sketch, "E431", {"start": v(27.94, 51.57) * mm, "mid": v(28.16, 51.83) * mm, "end": v(28.39, 52.08) * mm});
            skArc(sketch, "E432", {"start": v(28.39, 52.08) * mm, "mid": v(28.45, 52.16) * mm, "end": v(28.52, 52.23) * mm});
            skLineSegment(sketch, "E433", {"start": v(28.52, 52.23) * mm, "end": v(28.67, 52.39) * mm});
            skLineSegment(sketch, "E434", {"start": v(28.67, 52.39) * mm, "end": v(28.85, 52.57) * mm});
            skLineSegment(sketch, "E435", {"start": v(28.85, 52.57) * mm, "end": v(29.05, 52.78) * mm});
            skArc(sketch, "E436", {"start": v(29.05, 52.78) * mm, "mid": v(29.17, 52.9) * mm, "end": v(29.28, 53.01) * mm});
            skLineSegment(sketch, "E437", {"start": v(29.28, 53.01) * mm, "end": v(30.43, 54.15) * mm});
            skLineSegment(sketch, "E438", {"start": v(30.43, 54.15) * mm, "end": v(30.43, 60) * mm});
            skArc(sketch, "E439", {"start": v(30.43, 60) * mm, "mid": v(30.3, 60) * mm, "end": v(30.16, 60) * mm});
            skLineSegment(sketch, "E440", {"start": v(30.16, 60) * mm, "end": v(30.1, 60) * mm});
            skLineSegment(sketch, "E441", {"start": v(41.63, 39.75) * mm, "end": v(41.69, 39.8) * mm});
            skLineSegment(sketch, "E442", {"start": v(41.69, 39.8) * mm, "end": v(41.89, 40) * mm});
            skLineSegment(sketch, "E443", {"start": v(41.89, 40) * mm, "end": v(42.09, 40.2) * mm});
            skLineSegment(sketch, "E444", {"start": v(42.09, 40.2) * mm, "end": v(43.06, 41.18) * mm});
            skLineSegment(sketch, "E445", {"start": v(43.06, 41.18) * mm, "end": v(49.1, 41.18) * mm});
            skArc(sketch, "E446", {"start": v(49.1, 41.18) * mm, "mid": v(49.1, 41.1) * mm, "end": v(49.09, 41.04) * mm});
            skArc(sketch, "E447", {"start": v(49.09, 41.04) * mm, "mid": v(49.03, 40.14) * mm, "end": v(48.92, 39.25) * mm});
            skArc(sketch, "E448", {"start": v(48.92, 39.25) * mm, "mid": v(48.9, 39.13) * mm, "end": v(48.89, 39.02) * mm});
            skArc(sketch, "E449", {"start": v(48.89, 39.02) * mm, "mid": v(48.8, 38.5) * mm, "end": v(48.68, 37.98) * mm});
            skArc(sketch, "E450", {"start": v(48.68, 37.98) * mm, "mid": v(48.65, 37.85) * mm, "end": v(48.61, 37.71) * mm});
            skArc(sketch, "E451", {"start": v(48.61, 37.71) * mm, "mid": v(47.88, 35.52) * mm, "end": v(46.88, 33.43) * mm});
            skArc(sketch, "E452", {"start": v(46.88, 33.43) * mm, "mid": v(45.63, 31.49) * mm, "end": v(44.14, 29.72) * mm});
            skArc(sketch, "E453", {"start": v(44.14, 29.72) * mm, "mid": v(40.57, 26.79) * mm, "end": v(36.39, 24.83) * mm});
            skArc(sketch, "E454", {"start": v(36.39, 24.83) * mm, "mid": v(36.12, 24.75) * mm, "end": v(35.86, 24.68) * mm});
            skLineSegment(sketch, "E455", {"start": v(35.86, 24.68) * mm, "end": v(35.68, 24.64) * mm});
            skLineSegment(sketch, "E456", {"start": v(35.68, 24.64) * mm, "end": v(35.62, 24.63) * mm});
            skArc(sketch, "E457", {"start": v(35.62, 24.63) * mm, "mid": v(35.56, 24.6) * mm, "end": v(35.49, 24.6) * mm});
            skLineSegment(sketch, "E458", {"start": v(35.49, 24.6) * mm, "end": v(35.45, 24.58) * mm});
            skLineSegment(sketch, "E459", {"start": v(35.45, 24.58) * mm, "end": v(35.13, 24.51) * mm});
            skLineSegment(sketch, "E460", {"start": v(35.13, 24.51) * mm, "end": v(35.06, 24.5) * mm});
            skArc(sketch, "E461", {"start": v(35.06, 24.5) * mm, "mid": v(35, 24.49) * mm, "end": v(34.95, 24.48) * mm});
            skArc(sketch, "E462", {"start": v(34.95, 24.48) * mm, "mid": v(34.9, 24.47) * mm, "end": v(34.85, 24.46) * mm});
            skLineSegment(sketch, "E463", {"start": v(34.85, 24.46) * mm, "end": v(34.75, 24.44) * mm});
            skLineSegment(sketch, "E464", {"start": v(34.75, 24.44) * mm, "end": v(34.7, 24.43) * mm});
            skArc(sketch, "E465", {"start": v(34.7, 24.43) * mm, "mid": v(33.9, 24.28) * mm, "end": v(33.09, 24.16) * mm});
            skArc(sketch, "E466", {"start": v(33.09, 24.16) * mm, "mid": v(32.46, 24.1) * mm, "end": v(31.83, 24.05) * mm});
            skLineSegment(sketch, "E467", {"start": v(31.83, 24.05) * mm, "end": v(31.83, 29.95) * mm});
            skLineSegment(sketch, "E468", {"start": v(31.83, 29.95) * mm, "end": v(32.97, 31.09) * mm});
            skArc(sketch, "E469", {"start": v(32.97, 31.09) * mm, "mid": v(33.1, 31.2) * mm, "end": v(33.2, 31.32) * mm});
            skLineSegment(sketch, "E470", {"start": v(33.2, 31.32) * mm, "end": v(33.41, 31.53) * mm});
            skLineSegment(sketch, "E471", {"start": v(33.41, 31.53) * mm, "end": v(33.59, 31.71) * mm});
            skLineSegment(sketch, "E472", {"start": v(33.59, 31.71) * mm, "end": v(33.74, 31.87) * mm});
            skArc(sketch, "E473", {"start": v(33.74, 31.87) * mm, "mid": v(33.8, 31.95) * mm, "end": v(33.87, 32.02) * mm});
            skArc(sketch, "E474", {"start": v(33.87, 32.02) * mm, "mid": v(34.1, 32.27) * mm, "end": v(34.32, 32.53) * mm});
            skArc(sketch, "E475", {"start": v(34.32, 32.53) * mm, "mid": v(34.42, 32.67) * mm, "end": v(34.52, 32.81) * mm});
            skArc(sketch, "E476", {"start": v(34.52, 32.81) * mm, "mid": v(34.57, 32.89) * mm, "end": v(34.6, 32.97) * mm});
            skArc(sketch, "E477", {"start": v(34.6, 32.97) * mm, "mid": v(34.62, 33) * mm, "end": v(34.64, 33.05) * mm});
            skLineSegment(sketch, "E478", {"start": v(34.64, 33.05) * mm, "end": v(34.62, 33.14) * mm});
            skArc(sketch, "E479", {"start": v(34.62, 33.14) * mm, "mid": v(34.57, 33.2) * mm, "end": v(34.52, 33.26) * mm});
            skArc(sketch, "E480", {"start": v(34.52, 33.26) * mm, "mid": v(34.46, 33.38) * mm, "end": v(34.45, 33.51) * mm});
            skArc(sketch, "E481", {"start": v(34.45, 33.51) * mm, "mid": v(34.46, 33.63) * mm, "end": v(34.5, 33.75) * mm});
            skArc(sketch, "E482", {"start": v(34.5, 33.75) * mm, "mid": v(34.54, 33.85) * mm, "end": v(34.6, 33.94) * mm});
            skArc(sketch, "E483", {"start": v(34.6, 33.94) * mm, "mid": v(34.65, 34.03) * mm, "end": v(34.7, 34.12) * mm});
            skArc(sketch, "E484", {"start": v(34.7, 34.12) * mm, "mid": v(34.82, 34.27) * mm, "end": v(34.94, 34.42) * mm});
            skArc(sketch, "E485", {"start": v(34.94, 34.42) * mm, "mid": v(35.16, 34.68) * mm, "end": v(35.38, 34.93) * mm});
            skArc(sketch, "E486", {"start": v(35.38, 34.93) * mm, "mid": v(35.55, 35.12) * mm, "end": v(35.73, 35.3) * mm});
            skLineSegment(sketch, "E487", {"start": v(35.73, 35.3) * mm, "end": v(35.8, 35.37) * mm});
            skLineSegment(sketch, "E488", {"start": v(35.8, 35.37) * mm, "end": v(36.04, 35.63) * mm});
            skLineSegment(sketch, "E489", {"start": v(36.04, 35.63) * mm, "end": v(36.23, 35.82) * mm});
            skLineSegment(sketch, "E490", {"start": v(36.23, 35.82) * mm, "end": v(36.37, 35.96) * mm});
            skLineSegment(sketch, "E491", {"start": v(36.37, 35.96) * mm, "end": v(36.79, 36.39) * mm});
            skLineSegment(sketch, "E492", {"start": v(36.79, 36.39) * mm, "end": v(36.88, 36.47) * mm});
            skLineSegment(sketch, "E493", {"start": v(36.88, 36.47) * mm, "end": v(37.22, 36.81) * mm});
            skLineSegment(sketch, "E494", {"start": v(37.22, 36.81) * mm, "end": v(37.3, 36.89) * mm});
            skLineSegment(sketch, "E495", {"start": v(37.3, 36.89) * mm, "end": v(37.37, 36.96) * mm});
            skLineSegment(sketch, "E496", {"start": v(37.37, 36.96) * mm, "end": v(37.44, 37.03) * mm});
            skLineSegment(sketch, "E497", {"start": v(37.44, 37.03) * mm, "end": v(37.5, 37.1) * mm});
            skArc(sketch, "E498", {"start": v(37.5, 37.1) * mm, "mid": v(37.78, 37.36) * mm, "end": v(38.05, 37.62) * mm});
            skLineSegment(sketch, "E499", {"start": v(38.05, 37.62) * mm, "end": v(38.26, 37.81) * mm});
            skLineSegment(sketch, "E500", {"start": v(38.26, 37.81) * mm, "end": v(38.44, 37.98) * mm});
            skLineSegment(sketch, "E501", {"start": v(38.44, 37.98) * mm, "end": v(38.61, 38.13) * mm});
            skLineSegment(sketch, "E502", {"start": v(38.61, 38.13) * mm, "end": v(38.76, 38.25) * mm});
            skArc(sketch, "E503", {"start": v(38.76, 38.25) * mm, "mid": v(38.9, 38.36) * mm, "end": v(39.04, 38.47) * mm});
            skArc(sketch, "E504", {"start": v(39.04, 38.47) * mm, "mid": v(39.16, 38.54) * mm, "end": v(39.27, 38.6) * mm});
            skArc(sketch, "E505", {"start": v(39.27, 38.6) * mm, "mid": v(39.36, 38.66) * mm, "end": v(39.46, 38.7) * mm});
            skArc(sketch, "E506", {"start": v(39.46, 38.7) * mm, "mid": v(39.54, 38.72) * mm, "end": v(39.61, 38.73) * mm});
            skArc(sketch, "E507", {"start": v(39.61, 38.73) * mm, "mid": v(39.73, 38.73) * mm, "end": v(39.85, 38.7) * mm});
            skArc(sketch, "E508", {"start": v(39.85, 38.7) * mm, "mid": v(39.95, 38.64) * mm, "end": v(40.04, 38.56) * mm});
            skLineSegment(sketch, "E509", {"start": v(40.04, 38.56) * mm, "end": v(40.08, 38.54) * mm});
            skArc(sketch, "E510", {"start": v(40.08, 38.54) * mm, "mid": v(40.12, 38.54) * mm, "end": v(40.16, 38.55) * mm});
            skArc(sketch, "E511", {"start": v(40.16, 38.55) * mm, "mid": v(40.2, 38.57) * mm, "end": v(40.24, 38.58) * mm});
            skLineSegment(sketch, "E512", {"start": v(40.24, 38.58) * mm, "end": v(40.27, 38.6) * mm});
            skLineSegment(sketch, "E513", {"start": v(40.27, 38.6) * mm, "end": v(40.34, 38.64) * mm});
            skArc(sketch, "E514", {"start": v(40.34, 38.64) * mm, "mid": v(40.4, 38.68) * mm, "end": v(40.46, 38.72) * mm});
            skLineSegment(sketch, "E515", {"start": v(40.46, 38.72) * mm, "end": v(40.52, 38.76) * mm});
            skLineSegment(sketch, "E516", {"start": v(40.52, 38.76) * mm, "end": v(40.55, 38.79) * mm});
            skArc(sketch, "E517", {"start": v(40.55, 38.79) * mm, "mid": v(40.56, 38.8) * mm, "end": v(40.57, 38.8) * mm});
            skArc(sketch, "E518", {"start": v(40.57, 38.8) * mm, "mid": v(40.77, 38.97) * mm, "end": v(40.97, 39.13) * mm});
            skLineSegment(sketch, "E519", {"start": v(40.97, 39.13) * mm, "end": v(41, 39.17) * mm});
            skLineSegment(sketch, "E520", {"start": v(41, 39.17) * mm, "end": v(41.14, 39.3) * mm});
            skLineSegment(sketch, "E521", {"start": v(41.14, 39.3) * mm, "end": v(41.38, 39.52) * mm});
            skLineSegment(sketch, "E522", {"start": v(41.38, 39.52) * mm, "end": v(41.56, 39.69) * mm});
            skLineSegment(sketch, "E523", {"start": v(41.56, 39.69) * mm, "end": v(41.63, 39.75) * mm});
            skLineSegment(sketch, "E524", {"start": v(26.47, -21.02) * mm, "end": v(33.6, -21.02) * mm});
            skLineSegment(sketch, "E525", {"start": v(33.6, -21.02) * mm, "end": v(33.92, -21.02) * mm});
            skLineSegment(sketch, "E526", {"start": v(33.92, -21.02) * mm, "end": v(33.92, -20.11) * mm});
            skArc(sketch, "E527", {"start": v(33.92, -20.11) * mm, "mid": v(33.78, -20.03) * mm, "end": v(33.72, -19.87) * mm});
            skLineSegment(sketch, "E528", {"start": v(33.72, -19.87) * mm, "end": v(33.72, -19.67) * mm});
            skArc(sketch, "E529", {"start": v(33.72, -19.67) * mm, "mid": v(33.78, -19.5) * mm, "end": v(33.92, -19.42) * mm});
            skLineSegment(sketch, "E530", {"start": v(33.92, -19.42) * mm, "end": v(33.92, -18.52) * mm});
            skLineSegment(sketch, "E531", {"start": v(33.92, -18.52) * mm, "end": v(33.6, -18.52) * mm});
            skLineSegment(sketch, "E532", {"start": v(33.6, -18.52) * mm, "end": v(26.47, -18.52) * mm});
            skLineSegment(sketch, "E533", {"start": v(26.47, -18.52) * mm, "end": v(19.35, -18.52) * mm});
            skLineSegment(sketch, "E534", {"start": v(19.35, -18.52) * mm, "end": v(19.02, -18.52) * mm});
            skLineSegment(sketch, "E535", {"start": v(19.02, -18.52) * mm, "end": v(19.02, -19.42) * mm});
            skArc(sketch, "E536", {"start": v(19.02, -19.42) * mm, "mid": v(19.17, -19.5) * mm, "end": v(19.22, -19.67) * mm});
            skLineSegment(sketch, "E537", {"start": v(19.22, -19.67) * mm, "end": v(19.22, -19.87) * mm});
            skArc(sketch, "E538", {"start": v(19.22, -19.87) * mm, "mid": v(19.17, -20.03) * mm, "end": v(19.02, -20.11) * mm});
            skLineSegment(sketch, "E539", {"start": v(19.02, -20.11) * mm, "end": v(19.02, -21.02) * mm});
            skLineSegment(sketch, "E540", {"start": v(19.02, -21.02) * mm, "end": v(19.35, -21.02) * mm});
            skLineSegment(sketch, "E541", {"start": v(19.35, -21.02) * mm, "end": v(26.47, -21.02) * mm});
            skLineSegment(sketch, "E542", {"start": v(26.47, -66.02) * mm, "end": v(33.6, -66.02) * mm});
            skLineSegment(sketch, "E543", {"start": v(33.6, -66.02) * mm, "end": v(33.92, -66.02) * mm});
            skLineSegment(sketch, "E544", {"start": v(33.92, -66.02) * mm, "end": v(33.92, -65.11) * mm});
            skArc(sketch, "E545", {"start": v(33.92, -65.11) * mm, "mid": v(33.78, -65.03) * mm, "end": v(33.72, -64.87) * mm});
            skLineSegment(sketch, "E546", {"start": v(33.72, -64.87) * mm, "end": v(33.72, -64.67) * mm});
            skArc(sketch, "E547", {"start": v(33.72, -64.67) * mm, "mid": v(33.78, -64.5) * mm, "end": v(33.92, -64.42) * mm});
            skLineSegment(sketch, "E548", {"start": v(33.92, -64.42) * mm, "end": v(33.92, -63.52) * mm});
            skLineSegment(sketch, "E549", {"start": v(33.92, -63.52) * mm, "end": v(33.6, -63.52) * mm});
            skLineSegment(sketch, "E550", {"start": v(33.6, -63.52) * mm, "end": v(26.47, -63.52) * mm});
            skLineSegment(sketch, "E551", {"start": v(26.47, -63.52) * mm, "end": v(19.35, -63.52) * mm});
            skLineSegment(sketch, "E552", {"start": v(19.35, -63.52) * mm, "end": v(19.02, -63.52) * mm});
            skLineSegment(sketch, "E553", {"start": v(19.02, -63.52) * mm, "end": v(19.02, -64.42) * mm});
            skArc(sketch, "E554", {"start": v(19.02, -64.42) * mm, "mid": v(19.17, -64.5) * mm, "end": v(19.22, -64.67) * mm});
            skLineSegment(sketch, "E555", {"start": v(19.22, -64.67) * mm, "end": v(19.22, -64.87) * mm});
            skArc(sketch, "E556", {"start": v(19.22, -64.87) * mm, "mid": v(19.17, -65.03) * mm, "end": v(19.02, -65.11) * mm});
            skLineSegment(sketch, "E557", {"start": v(19.02, -65.11) * mm, "end": v(19.02, -66.02) * mm});
            skLineSegment(sketch, "E558", {"start": v(19.02, -66.02) * mm, "end": v(19.35, -66.02) * mm});
            skLineSegment(sketch, "E559", {"start": v(19.35, -66.02) * mm, "end": v(26.47, -66.02) * mm});
            skLineSegment(sketch, "E560", {"start": v(44.25, -42.27) * mm, "end": v(44.25, -70.77) * mm});
            skLineSegment(sketch, "E561", {"start": v(44.25, -70.77) * mm, "end": v(44.25, -72.27) * mm});
            skLineSegment(sketch, "E562", {"start": v(44.25, -72.27) * mm, "end": v(44.25, -72.82) * mm});
            skLineSegment(sketch, "E563", {"start": v(44.25, -72.82) * mm, "end": v(45.15, -72.82) * mm});
            skLineSegment(sketch, "E564", {"start": v(45.15, -72.82) * mm, "end": v(45.15, -72.27) * mm});
            skArc(sketch, "E565", {"start": v(45.15, -72.27) * mm, "mid": v(45.22, -72.1) * mm, "end": v(45.4, -72.02) * mm});
            skLineSegment(sketch, "E566", {"start": v(45.4, -72.02) * mm, "end": v(45.6, -72.02) * mm});
            skArc(sketch, "E567", {"start": v(45.6, -72.02) * mm, "mid": v(45.78, -72.1) * mm, "end": v(45.85, -72.27) * mm});
            skLineSegment(sketch, "E568", {"start": v(45.85, -72.27) * mm, "end": v(45.85, -72.82) * mm});
            skLineSegment(sketch, "E569", {"start": v(45.85, -72.82) * mm, "end": v(46.75, -72.82) * mm});
            skLineSegment(sketch, "E570", {"start": v(46.75, -72.82) * mm, "end": v(46.75, -72.27) * mm});
            skLineSegment(sketch, "E571", {"start": v(46.75, -72.27) * mm, "end": v(46.75, -70.77) * mm});
            skLineSegment(sketch, "E572", {"start": v(46.75, -70.77) * mm, "end": v(46.75, -42.27) * mm});
            skLineSegment(sketch, "E573", {"start": v(46.75, -42.27) * mm, "end": v(46.75, -13.77) * mm});
            skLineSegment(sketch, "E574", {"start": v(46.75, -13.77) * mm, "end": v(46.75, -12.27) * mm});
            skLineSegment(sketch, "E575", {"start": v(46.75, -12.27) * mm, "end": v(46.75, -11.72) * mm});
            skLineSegment(sketch, "E576", {"start": v(46.75, -11.72) * mm, "end": v(45.85, -11.72) * mm});
            skLineSegment(sketch, "E577", {"start": v(45.85, -11.72) * mm, "end": v(45.85, -12.27) * mm});
            skArc(sketch, "E578", {"start": v(45.85, -12.27) * mm, "mid": v(45.78, -12.45) * mm, "end": v(45.6, -12.52) * mm});
            skLineSegment(sketch, "E579", {"start": v(45.6, -12.52) * mm, "end": v(45.4, -12.52) * mm});
            skArc(sketch, "E580", {"start": v(45.4, -12.52) * mm, "mid": v(45.22, -12.45) * mm, "end": v(45.15, -12.27) * mm});
            skLineSegment(sketch, "E581", {"start": v(45.15, -12.27) * mm, "end": v(45.15, -11.72) * mm});
            skLineSegment(sketch, "E582", {"start": v(45.15, -11.72) * mm, "end": v(44.25, -11.72) * mm});
            skLineSegment(sketch, "E583", {"start": v(44.25, -11.72) * mm, "end": v(44.25, -12.27) * mm});
            skLineSegment(sketch, "E584", {"start": v(44.25, -12.27) * mm, "end": v(44.25, -13.77) * mm});
            skLineSegment(sketch, "E585", {"start": v(44.25, -13.77) * mm, "end": v(44.25, -42.27) * mm});
            skLineSegment(sketch, "E586", {"start": v(53.57, 18.52) * mm, "end": v(60.7, 18.52) * mm});
            skLineSegment(sketch, "E587", {"start": v(60.7, 18.52) * mm, "end": v(61.02, 18.52) * mm});
            skLineSegment(sketch, "E588", {"start": v(61.02, 18.52) * mm, "end": v(61.02, 19.43) * mm});
            skArc(sketch, "E589", {"start": v(61.02, 19.43) * mm, "mid": v(60.87, 19.51) * mm, "end": v(60.82, 19.67) * mm});
            skLineSegment(sketch, "E590", {"start": v(60.82, 19.67) * mm, "end": v(60.82, 19.87) * mm});
            skArc(sketch, "E591", {"start": v(60.82, 19.87) * mm, "mid": v(60.87, 20.03) * mm, "end": v(61.02, 20.12) * mm});
            skLineSegment(sketch, "E592", {"start": v(61.02, 20.12) * mm, "end": v(61.02, 21.02) * mm});
            skLineSegment(sketch, "E593", {"start": v(61.02, 21.02) * mm, "end": v(60.7, 21.02) * mm});
            skLineSegment(sketch, "E594", {"start": v(60.7, 21.02) * mm, "end": v(53.57, 21.02) * mm});
            skLineSegment(sketch, "E595", {"start": v(53.57, 21.02) * mm, "end": v(46.44, 21.02) * mm});
            skLineSegment(sketch, "E596", {"start": v(46.44, 21.02) * mm, "end": v(46.12, 21.02) * mm});
            skLineSegment(sketch, "E597", {"start": v(46.12, 21.02) * mm, "end": v(46.12, 20.12) * mm});
            skArc(sketch, "E598", {"start": v(46.12, 20.12) * mm, "mid": v(46.26, 20.03) * mm, "end": v(46.32, 19.87) * mm});
            skLineSegment(sketch, "E599", {"start": v(46.32, 19.87) * mm, "end": v(46.32, 19.67) * mm});
            skArc(sketch, "E600", {"start": v(46.32, 19.67) * mm, "mid": v(46.26, 19.51) * mm, "end": v(46.12, 19.43) * mm});
            skLineSegment(sketch, "E601", {"start": v(46.12, 19.43) * mm, "end": v(46.12, 18.52) * mm});
            skLineSegment(sketch, "E602", {"start": v(46.12, 18.52) * mm, "end": v(46.44, 18.52) * mm});
            skLineSegment(sketch, "E603", {"start": v(46.44, 18.52) * mm, "end": v(53.57, 18.52) * mm});
            skLineSegment(sketch, "E604", {"start": v(53.57, 63.52) * mm, "end": v(60.7, 63.52) * mm});
            skLineSegment(sketch, "E605", {"start": v(60.7, 63.52) * mm, "end": v(61.02, 63.52) * mm});
            skLineSegment(sketch, "E606", {"start": v(61.02, 63.52) * mm, "end": v(61.02, 64.43) * mm});
            skArc(sketch, "E607", {"start": v(61.02, 64.43) * mm, "mid": v(60.87, 64.51) * mm, "end": v(60.82, 64.67) * mm});
            skLineSegment(sketch, "E608", {"start": v(60.82, 64.67) * mm, "end": v(60.82, 64.87) * mm});
            skArc(sketch, "E609", {"start": v(60.82, 64.87) * mm, "mid": v(60.87, 65.03) * mm, "end": v(61.02, 65.12) * mm});
            skLineSegment(sketch, "E610", {"start": v(61.02, 65.12) * mm, "end": v(61.02, 66.02) * mm});
            skLineSegment(sketch, "E611", {"start": v(61.02, 66.02) * mm, "end": v(60.7, 66.02) * mm});
            skLineSegment(sketch, "E612", {"start": v(60.7, 66.02) * mm, "end": v(53.57, 66.02) * mm});
            skLineSegment(sketch, "E613", {"start": v(53.57, 66.02) * mm, "end": v(46.44, 66.02) * mm});
            skLineSegment(sketch, "E614", {"start": v(46.44, 66.02) * mm, "end": v(46.12, 66.02) * mm});
            skLineSegment(sketch, "E615", {"start": v(46.12, 66.02) * mm, "end": v(46.12, 65.12) * mm});
            skArc(sketch, "E616", {"start": v(46.12, 65.12) * mm, "mid": v(46.26, 65.03) * mm, "end": v(46.32, 64.87) * mm});
            skLineSegment(sketch, "E617", {"start": v(46.32, 64.87) * mm, "end": v(46.32, 64.67) * mm});
            skArc(sketch, "E618", {"start": v(46.32, 64.67) * mm, "mid": v(46.26, 64.51) * mm, "end": v(46.12, 64.43) * mm});
            skLineSegment(sketch, "E619", {"start": v(46.12, 64.43) * mm, "end": v(46.12, 63.52) * mm});
            skLineSegment(sketch, "E620", {"start": v(46.12, 63.52) * mm, "end": v(46.44, 63.52) * mm});
            skLineSegment(sketch, "E621", {"start": v(46.44, 63.52) * mm, "end": v(53.57, 63.52) * mm});
            skLineSegment(sketch, "E622", {"start": v(92, -32.25) * mm, "end": v(92, -32.25) * mm});
            skLineSegment(sketch, "E623", {"start": v(92, -32.25) * mm, "end": v(91.87, -32.25) * mm});
            skArc(sketch, "E624", {"start": v(91.87, -32.25) * mm, "mid": v(83.37, -37.15) * mm, "end": v(83.37, -46.96) * mm});
            skArc(sketch, "E625", {"start": v(83.37, -46.96) * mm, "mid": v(87.02, -50.58) * mm, "end": v(92, -51.86) * mm});
            skArc(sketch, "E626", {"start": v(92, -51.86) * mm, "mid": v(92.18, -51.93) * mm, "end": v(92.25, -52.11) * mm});
            skLineSegment(sketch, "E627", {"start": v(92.25, -52.11) * mm, "end": v(92.25, -80.27) * mm});
            skArc(sketch, "E628", {"start": v(92.25, -80.27) * mm, "mid": v(91.6, -81.86) * mm, "end": v(90, -82.52) * mm});
            skLineSegment(sketch, "E629", {"start": v(90, -82.52) * mm, "end": v(-28, -82.52) * mm});
            skLineSegment(sketch, "E630", {"start": v(-28, -82.52) * mm, "end": v(-90, -82.52) * mm});
            skArc(sketch, "E631", {"start": v(-90, -82.52) * mm, "mid": v(-91.6, -81.86) * mm, "end": v(-92.25, -80.27) * mm});
            skLineSegment(sketch, "E632", {"start": v(-92.25, -80.27) * mm, "end": v(-92.25, -4.27) * mm});
            skArc(sketch, "E633", {"start": v(-92.25, -4.27) * mm, "mid": v(-91.6, -2.68) * mm, "end": v(-90, -2.02) * mm});
            skLineSegment(sketch, "E634", {"start": v(-90, -2.02) * mm, "end": v(-28, -2.02) * mm});
            skLineSegment(sketch, "E635", {"start": v(-28, -2.02) * mm, "end": v(90, -2.02) * mm});
            skArc(sketch, "E636", {"start": v(90, -2.02) * mm, "mid": v(91.6, -2.68) * mm, "end": v(92.25, -4.27) * mm});
            skLineSegment(sketch, "E637", {"start": v(92.25, -4.27) * mm, "end": v(92.25, -4.42) * mm});
            skLineSegment(sketch, "E638", {"start": v(92.25, -4.42) * mm, "end": v(92.25, -32) * mm});
            skArc(sketch, "E639", {"start": v(92.25, -32) * mm, "mid": v(92.18, -32.17) * mm, "end": v(92, -32.25) * mm});
            skLineSegment(sketch, "E640", {"start": v(89.13, 2.02) * mm, "end": v(74.24, 2.02) * mm});
            skArc(sketch, "E641", {"start": v(74.24, 2.02) * mm, "mid": v(74.07, 2.1) * mm, "end": v(74, 2.27) * mm});
            skLineSegment(sketch, "E642", {"start": v(74, 2.27) * mm, "end": v(74, 10.77) * mm});
            skLineSegment(sketch, "E643", {"start": v(74, 10.77) * mm, "end": v(74, 12.27) * mm});
            skLineSegment(sketch, "E644", {"start": v(74, 12.27) * mm, "end": v(74, 12.57) * mm});
            skArc(sketch, "E645", {"start": v(74, 12.57) * mm, "mid": v(73.92, 12.75) * mm, "end": v(73.74, 12.82) * mm});
            skLineSegment(sketch, "E646", {"start": v(73.74, 12.82) * mm, "end": v(73.24, 12.82) * mm});
            skArc(sketch, "E647", {"start": v(73.24, 12.82) * mm, "mid": v(73.07, 12.75) * mm, "end": v(73, 12.57) * mm});
            skLineSegment(sketch, "E648", {"start": v(73, 12.57) * mm, "end": v(73, 12.27) * mm});
            skArc(sketch, "E649", {"start": v(73, 12.27) * mm, "mid": v(72.92, 12.1) * mm, "end": v(72.74, 12.02) * mm});
            skLineSegment(sketch, "E650", {"start": v(72.74, 12.02) * mm, "end": v(43.13, 12.02) * mm});
            skLineSegment(sketch, "E651", {"start": v(43.13, 12.02) * mm, "end": v(-16.87, 12.02) * mm});
            skArc(sketch, "E652", {"start": v(-16.87, 12.02) * mm, "mid": v(-18.46, 12.68) * mm, "end": v(-19.12, 14.27) * mm});
            skLineSegment(sketch, "E653", {"start": v(-19.12, 14.27) * mm, "end": v(-19.12, 70.27) * mm});
            skArc(sketch, "E654", {"start": v(-19.12, 70.27) * mm, "mid": v(-18.46, 71.86) * mm, "end": v(-16.87, 72.52) * mm});
            skLineSegment(sketch, "E655", {"start": v(-16.87, 72.52) * mm, "end": v(43.13, 72.52) * mm});
            skLineSegment(sketch, "E656", {"start": v(43.13, 72.52) * mm, "end": v(72.74, 72.52) * mm});
            skArc(sketch, "E657", {"start": v(72.74, 72.52) * mm, "mid": v(72.92, 72.45) * mm, "end": v(73, 72.27) * mm});
            skLineSegment(sketch, "E658", {"start": v(73, 72.27) * mm, "end": v(73, 71.97) * mm});
            skArc(sketch, "E659", {"start": v(73, 71.97) * mm, "mid": v(73.07, 71.8) * mm, "end": v(73.24, 71.72) * mm});
            skLineSegment(sketch, "E660", {"start": v(73.24, 71.72) * mm, "end": v(73.74, 71.72) * mm});
            skArc(sketch, "E661", {"start": v(73.74, 71.72) * mm, "mid": v(73.92, 71.8) * mm, "end": v(74, 71.97) * mm});
            skLineSegment(sketch, "E662", {"start": v(74, 71.97) * mm, "end": v(74, 72.27) * mm});
            skLineSegment(sketch, "E663", {"start": v(74, 72.27) * mm, "end": v(74, 73.77) * mm});
            skLineSegment(sketch, "E664", {"start": v(74, 73.77) * mm, "end": v(74, 82.27) * mm});
            skArc(sketch, "E665", {"start": v(74, 82.27) * mm, "mid": v(74.07, 82.45) * mm, "end": v(74.24, 82.52) * mm});
            skLineSegment(sketch, "E666", {"start": v(74.24, 82.52) * mm, "end": v(89.13, 82.52) * mm});
            skArc(sketch, "E667", {"start": v(89.13, 82.52) * mm, "mid": v(90.72, 81.86) * mm, "end": v(91.38, 80.27) * mm});
            skLineSegment(sketch, "E668", {"start": v(91.38, 80.27) * mm, "end": v(91.38, 54.54) * mm});
            skArc(sketch, "E669", {"start": v(91.38, 54.54) * mm, "mid": v(90.72, 52.95) * mm, "end": v(89.13, 52.3) * mm});
            skLineSegment(sketch, "E670", {"start": v(89.13, 52.3) * mm, "end": v(78.24, 52.3) * mm});
            skLineSegment(sketch, "E671", {"start": v(78.24, 52.3) * mm, "end": v(76.24, 52.3) * mm});
            skArc(sketch, "E672", {"start": v(76.24, 52.3) * mm, "mid": v(75, 51.78) * mm, "end": v(74.5, 50.54) * mm});
            skLineSegment(sketch, "E673", {"start": v(74.5, 50.54) * mm, "end": v(74.5, 34.43) * mm});
            skArc(sketch, "E674", {"start": v(74.5, 34.43) * mm, "mid": v(75, 33.2) * mm, "end": v(76.24, 32.68) * mm});
            skLineSegment(sketch, "E675", {"start": v(76.24, 32.68) * mm, "end": v(78.24, 32.68) * mm});
            skLineSegment(sketch, "E676", {"start": v(78.24, 32.68) * mm, "end": v(89.13, 32.68) * mm});
            skArc(sketch, "E677", {"start": v(89.13, 32.68) * mm, "mid": v(90.72, 32.02) * mm, "end": v(91.38, 30.43) * mm});
            skLineSegment(sketch, "E678", {"start": v(91.38, 30.43) * mm, "end": v(91.38, 4.27) * mm});
            skArc(sketch, "E679", {"start": v(91.38, 4.27) * mm, "mid": v(90.72, 2.68) * mm, "end": v(89.13, 2.02) * mm});
            skLineSegment(sketch, "E680", {"start": v(-71.81, 38.83) * mm, "end": v(-40.99, 2.58) * mm});
            skArc(sketch, "E681", {"start": v(-40.99, 2.58) * mm, "mid": v(-40.71, 2.5) * mm, "end": v(-40.55, 2.74) * mm});
            skLineSegment(sketch, "E682", {"start": v(-40.55, 2.74) * mm, "end": v(-40.55, 13.4) * mm});
            skLineSegment(sketch, "E683", {"start": v(-40.55, 13.4) * mm, "end": v(-39.4, 13.4) * mm});
            skArc(sketch, "E684", {"start": v(-39.4, 13.4) * mm, "mid": v(-39.35, 13.4) * mm, "end": v(-39.3, 13.42) * mm});
            skArc(sketch, "E685", {"start": v(-39.3, 13.42) * mm, "mid": v(-39.25, 13.4) * mm, "end": v(-39.2, 13.4) * mm});
            skLineSegment(sketch, "E686", {"start": v(-39.2, 13.4) * mm, "end": v(-37.8, 13.4) * mm});
            skArc(sketch, "E687", {"start": v(-37.8, 13.4) * mm, "mid": v(-37.62, 13.47) * mm, "end": v(-37.55, 13.65) * mm});
            skLineSegment(sketch, "E688", {"start": v(-37.55, 13.65) * mm, "end": v(-37.55, 13.85) * mm});
            skLineSegment(sketch, "E689", {"start": v(-37.55, 13.85) * mm, "end": v(-37.55, 14.22) * mm});
            skLineSegment(sketch, "E690", {"start": v(-37.55, 14.22) * mm, "end": v(-37.55, 21.35) * mm});
            skLineSegment(sketch, "E691", {"start": v(-37.55, 21.35) * mm, "end": v(-37.55, 28.47) * mm});
            skLineSegment(sketch, "E692", {"start": v(-37.55, 28.47) * mm, "end": v(-37.55, 28.85) * mm});
            skLineSegment(sketch, "E693", {"start": v(-37.55, 28.85) * mm, "end": v(-37.55, 29.05) * mm});
            skArc(sketch, "E694", {"start": v(-37.55, 29.05) * mm, "mid": v(-37.62, 29.22) * mm, "end": v(-37.8, 29.3) * mm});
            skLineSegment(sketch, "E695", {"start": v(-37.8, 29.3) * mm, "end": v(-39.2, 29.3) * mm});
            skArc(sketch, "E696", {"start": v(-39.2, 29.3) * mm, "mid": v(-39.25, 29.3) * mm, "end": v(-39.3, 29.28) * mm});
            skArc(sketch, "E697", {"start": v(-39.3, 29.28) * mm, "mid": v(-39.35, 29.3) * mm, "end": v(-39.4, 29.3) * mm});
            skLineSegment(sketch, "E698", {"start": v(-39.4, 29.3) * mm, "end": v(-40.55, 29.3) * mm});
            skLineSegment(sketch, "E699", {"start": v(-40.55, 29.3) * mm, "end": v(-40.55, 39) * mm});
            skArc(sketch, "E700", {"start": v(-40.55, 39) * mm, "mid": v(-40.62, 39.17) * mm, "end": v(-40.8, 39.24) * mm});
            skLineSegment(sketch, "E701", {"start": v(-40.8, 39.24) * mm, "end": v(-50.53, 39.24) * mm});
            skLineSegment(sketch, "E702", {"start": v(-50.53, 39.24) * mm, "end": v(-50.53, 40.4) * mm});
            skArc(sketch, "E703", {"start": v(-50.53, 40.4) * mm, "mid": v(-50.53, 40.44) * mm, "end": v(-50.55, 40.5) * mm});
            skArc(sketch, "E704", {"start": v(-50.55, 40.5) * mm, "mid": v(-50.53, 40.54) * mm, "end": v(-50.53, 40.6) * mm});
            skLineSegment(sketch, "E705", {"start": v(-50.53, 40.6) * mm, "end": v(-50.53, 42) * mm});
            skArc(sketch, "E706", {"start": v(-50.53, 42) * mm, "mid": v(-50.6, 42.17) * mm, "end": v(-50.78, 42.24) * mm});
            skLineSegment(sketch, "E707", {"start": v(-50.78, 42.24) * mm, "end": v(-50.98, 42.24) * mm});
            skLineSegment(sketch, "E708", {"start": v(-50.98, 42.24) * mm, "end": v(-51.35, 42.24) * mm});
            skLineSegment(sketch, "E709", {"start": v(-51.35, 42.24) * mm, "end": v(-58.48, 42.24) * mm});
            skLineSegment(sketch, "E710", {"start": v(-58.48, 42.24) * mm, "end": v(-65.6, 42.24) * mm});
            skLineSegment(sketch, "E711", {"start": v(-65.6, 42.24) * mm, "end": v(-65.98, 42.24) * mm});
            skLineSegment(sketch, "E712", {"start": v(-65.98, 42.24) * mm, "end": v(-66.18, 42.24) * mm});
            skArc(sketch, "E713", {"start": v(-66.18, 42.24) * mm, "mid": v(-66.35, 42.17) * mm, "end": v(-66.43, 42) * mm});
            skLineSegment(sketch, "E714", {"start": v(-66.43, 42) * mm, "end": v(-66.43, 40.6) * mm});
            skArc(sketch, "E715", {"start": v(-66.43, 40.6) * mm, "mid": v(-66.42, 40.54) * mm, "end": v(-66.4, 40.5) * mm});
            skArc(sketch, "E716", {"start": v(-66.4, 40.5) * mm, "mid": v(-66.42, 40.44) * mm, "end": v(-66.43, 40.4) * mm});
            skLineSegment(sketch, "E717", {"start": v(-66.43, 40.4) * mm, "end": v(-66.43, 39.24) * mm});
            skLineSegment(sketch, "E718", {"start": v(-66.43, 39.24) * mm, "end": v(-71.62, 39.24) * mm});
            skArc(sketch, "E719", {"start": v(-71.62, 39.24) * mm, "mid": v(-71.85, 39.1) * mm, "end": v(-71.81, 38.83) * mm});
            skLineSegment(sketch, "E720", {"start": v(-86.07, 36.09) * mm, "end": v(-49.81, 5.26) * mm});
            skArc(sketch, "E721", {"start": v(-49.81, 5.26) * mm, "mid": v(-49.74, 4.99) * mm, "end": v(-49.97, 4.82) * mm});
            skLineSegment(sketch, "E722", {"start": v(-49.97, 4.82) * mm, "end": v(-60.63, 4.82) * mm});
            skLineSegment(sketch, "E723", {"start": v(-60.63, 4.82) * mm, "end": v(-60.63, 3.67) * mm});
            skArc(sketch, "E724", {"start": v(-60.63, 3.67) * mm, "mid": v(-60.64, 3.62) * mm, "end": v(-60.65, 3.57) * mm});
            skArc(sketch, "E725", {"start": v(-60.65, 3.57) * mm, "mid": v(-60.64, 3.52) * mm, "end": v(-60.63, 3.47) * mm});
            skLineSegment(sketch, "E726", {"start": v(-60.63, 3.47) * mm, "end": v(-60.63, 2.07) * mm});
            skArc(sketch, "E727", {"start": v(-60.63, 2.07) * mm, "mid": v(-60.7, 1.9) * mm, "end": v(-60.88, 1.82) * mm});
            skLineSegment(sketch, "E728", {"start": v(-60.88, 1.82) * mm, "end": v(-61.08, 1.82) * mm});
            skLineSegment(sketch, "E729", {"start": v(-61.08, 1.82) * mm, "end": v(-61.46, 1.82) * mm});
            skLineSegment(sketch, "E730", {"start": v(-61.46, 1.82) * mm, "end": v(-68.58, 1.82) * mm});
            skLineSegment(sketch, "E731", {"start": v(-68.58, 1.82) * mm, "end": v(-75.7, 1.82) * mm});
            skLineSegment(sketch, "E732", {"start": v(-75.7, 1.82) * mm, "end": v(-76.08, 1.82) * mm});
            skLineSegment(sketch, "E733", {"start": v(-76.08, 1.82) * mm, "end": v(-76.28, 1.82) * mm});
            skArc(sketch, "E734", {"start": v(-76.28, 1.82) * mm, "mid": v(-76.46, 1.9) * mm, "end": v(-76.53, 2.07) * mm});
            skLineSegment(sketch, "E735", {"start": v(-76.53, 2.07) * mm, "end": v(-76.53, 3.47) * mm});
            skArc(sketch, "E736", {"start": v(-76.53, 3.47) * mm, "mid": v(-76.53, 3.52) * mm, "end": v(-76.51, 3.57) * mm});
            skArc(sketch, "E737", {"start": v(-76.51, 3.57) * mm, "mid": v(-76.53, 3.62) * mm, "end": v(-76.53, 3.67) * mm});
            skLineSegment(sketch, "E738", {"start": v(-76.53, 3.67) * mm, "end": v(-76.53, 4.82) * mm});
            skLineSegment(sketch, "E739", {"start": v(-76.53, 4.82) * mm, "end": v(-86.23, 4.82) * mm});
            skArc(sketch, "E740", {"start": v(-86.23, 4.82) * mm, "mid": v(-86.4, 4.9) * mm, "end": v(-86.48, 5.07) * mm});
            skLineSegment(sketch, "E741", {"start": v(-86.48, 5.07) * mm, "end": v(-86.48, 14.8) * mm});
            skLineSegment(sketch, "E742", {"start": v(-86.48, 14.8) * mm, "end": v(-87.63, 14.8) * mm});
            skArc(sketch, "E743", {"start": v(-87.63, 14.8) * mm, "mid": v(-87.68, 14.8) * mm, "end": v(-87.73, 14.82) * mm});
            skArc(sketch, "E744", {"start": v(-87.73, 14.82) * mm, "mid": v(-87.78, 14.8) * mm, "end": v(-87.83, 14.8) * mm});
            skLineSegment(sketch, "E745", {"start": v(-87.83, 14.8) * mm, "end": v(-89.23, 14.8) * mm});
            skArc(sketch, "E746", {"start": v(-89.23, 14.8) * mm, "mid": v(-89.4, 14.87) * mm, "end": v(-89.48, 15.05) * mm});
            skLineSegment(sketch, "E747", {"start": v(-89.48, 15.05) * mm, "end": v(-89.48, 15.25) * mm});
            skLineSegment(sketch, "E748", {"start": v(-89.48, 15.25) * mm, "end": v(-89.48, 15.62) * mm});
            skLineSegment(sketch, "E749", {"start": v(-89.48, 15.62) * mm, "end": v(-89.48, 22.75) * mm});
            skLineSegment(sketch, "E750", {"start": v(-89.48, 22.75) * mm, "end": v(-89.48, 29.87) * mm});
            skLineSegment(sketch, "E751", {"start": v(-89.48, 29.87) * mm, "end": v(-89.48, 30.25) * mm});
            skLineSegment(sketch, "E752", {"start": v(-89.48, 30.25) * mm, "end": v(-89.48, 30.45) * mm});
            skArc(sketch, "E753", {"start": v(-89.48, 30.45) * mm, "mid": v(-89.4, 30.63) * mm, "end": v(-89.23, 30.7) * mm});
            skLineSegment(sketch, "E754", {"start": v(-89.23, 30.7) * mm, "end": v(-87.83, 30.7) * mm});
            skArc(sketch, "E755", {"start": v(-87.83, 30.7) * mm, "mid": v(-87.78, 30.7) * mm, "end": v(-87.73, 30.68) * mm});
            skArc(sketch, "E756", {"start": v(-87.73, 30.68) * mm, "mid": v(-87.68, 30.7) * mm, "end": v(-87.63, 30.7) * mm});
            skLineSegment(sketch, "E757", {"start": v(-87.63, 30.7) * mm, "end": v(-86.48, 30.7) * mm});
            skLineSegment(sketch, "E758", {"start": v(-86.48, 30.7) * mm, "end": v(-86.48, 35.9) * mm});
            skArc(sketch, "E759", {"start": v(-86.48, 35.9) * mm, "mid": v(-86.33, 36.12) * mm, "end": v(-86.07, 36.09) * mm});
            skLineSegment(sketch, "E760.bottom", {"start": v(-90, -82.52) * mm, "end": v(90, -82.52) * mm});
            skLineSegment(sketch, "E760.top", {"start": v(-90, -2.02) * mm, "end": v(90, -2.02) * mm});
            skLineSegment(sketch, "E760.left", {"start": v(-90, -82.52) * mm, "end": v(-90, -2.02) * mm});
            skLineSegment(sketch, "E760.right", {"start": v(90, -82.52) * mm, "end": v(90, -2.02) * mm});
            skLineSegment(sketch, "E761.bottom", {"start": v(92.25, -4.27) * mm, "end": v(-92.25, -4.27) * mm});
            skLineSegment(sketch, "E761.top", {"start": v(92.25, -80.27) * mm, "end": v(-92.25, -80.27) * mm});
            skLineSegment(sketch, "E761.left", {"start": v(92.25, -4.27) * mm, "end": v(92.25, -80.27) * mm});
            skLineSegment(sketch, "E761.right", {"start": v(-92.25, -4.27) * mm, "end": v(-92.25, -80.27) * mm});
            skLineSegment(sketch, "E762.bottom", {"start": v(-92.25, -80.27) * mm, "end": v(-90, -80.27) * mm});
            skLineSegment(sketch, "E762.top", {"start": v(-92.25, -82.52) * mm, "end": v(-90, -82.52) * mm});
            skLineSegment(sketch, "E762.left", {"start": v(-92.25, -80.27) * mm, "end": v(-92.25, -82.52) * mm});
            skLineSegment(sketch, "E762.right", {"start": v(-90, -80.27) * mm, "end": v(-90, -82.52) * mm});
            skLineSegment(sketch, "E763.bottom", {"start": v(90, -82.52) * mm, "end": v(92.25, -82.52) * mm});
            skLineSegment(sketch, "E763.top", {"start": v(90, -80.27) * mm, "end": v(92.25, -80.27) * mm});
            skLineSegment(sketch, "E763.left", {"start": v(90, -82.52) * mm, "end": v(90, -80.27) * mm});
            skLineSegment(sketch, "E763.right", {"start": v(92.25, -82.52) * mm, "end": v(92.25, -80.27) * mm});
            skLineSegment(sketch, "E764.bottom", {"start": v(92.25, -4.27) * mm, "end": v(90, -4.27) * mm});
            skLineSegment(sketch, "E764.top", {"start": v(92.25, -2.02) * mm, "end": v(90, -2.02) * mm});
            skLineSegment(sketch, "E764.left", {"start": v(92.25, -4.27) * mm, "end": v(92.25, -2.02) * mm});
            skLineSegment(sketch, "E764.right", {"start": v(90, -4.27) * mm, "end": v(90, -2.02) * mm});
            skLineSegment(sketch, "E765.bottom", {"start": v(-92.25, -4.27) * mm, "end": v(-90, -4.27) * mm});
            skLineSegment(sketch, "E765.top", {"start": v(-92.25, -2.02) * mm, "end": v(-90, -2.02) * mm});
            skLineSegment(sketch, "E765.left", {"start": v(-92.25, -4.27) * mm, "end": v(-92.25, -2.02) * mm});
            skLineSegment(sketch, "E765.right", {"start": v(-90, -4.27) * mm, "end": v(-90, -2.02) * mm});
            skLineSegment(sketch, "E766.left", {"start": v(-52, -41.1) * mm, "end": v(-52, -43.28) * mm});
            skLineSegment(sketch, "E766.right", {"start": v(-3.98, -41.1) * mm, "end": v(-3.98, -43.28) * mm});
            skLineSegment(sketch, "E767", {"start": v(-52, -41.1) * mm, "end": v(-43.94, -41.1) * mm});
            skLineSegment(sketch, "E768.bottom", {"start": v(-29.1, -66.2) * mm, "end": v(-26.96, -66.2) * mm});
            skLineSegment(sketch, "E768.top", {"start": v(-29.1, -18.25) * mm, "end": v(-26.96, -18.25) * mm});
            skLineSegment(sketch, "E769", {"start": v(-26.96, -26.25) * mm, "end": v(-2.54, -50.57) * mm});
            skLineSegment(sketch, "E770", {"start": v(-28, -59.37) * mm, "end": v(-56.37, -31.13) * mm});
            skLineSegment(sketch, "E771", {"start": v(-45.14, -42.3) * mm, "end": v(-25.18, -22.25) * mm});
            skPoint(sketch, "E771.endSnap0", {"position": v(-26.96, -22.25) * mm});
            skLineSegment(sketch, "E772", {"start": v(-11.98, -43.28) * mm, "end": v(-31.11, -62.5) * mm});
            skLineSegment(sketch, "E773", {"start": v(-37.5, -49.87) * mm, "end": v(-20.44, -32.75) * mm});
            skLineSegment(sketch, "E774", {"start": v(-35.65, -51.71) * mm, "end": v(-18.6, -34.58) * mm});
            skLineSegment(sketch, "E775.0", {"start": v(-33.8, -53.55) * mm, "end": v(-16.78, -36.44) * mm});
            skLineSegment(sketch, "E776.0", {"start": v(-39.33, -48.04) * mm, "end": v(-22.3, -30.93) * mm});
            skLineSegment(sketch, "E777", {"start": v(-17.42, -48.75) * mm, "end": v(-40.32, -25.95) * mm});
            skLineSegment(sketch, "E778.0", {"start": v(-21.38, -52.72) * mm, "end": v(-44.27, -29.92) * mm});
            skLineSegment(sketch, "E779.0", {"start": v(-15.59, -46.9) * mm, "end": v(-38.49, -24.11) * mm});
            skLineSegment(sketch, "E780.0", {"start": v(-23.2, -54.56) * mm, "end": v(-46.1, -31.76) * mm});
            skLineSegment(sketch, "E781.0", {"start": v(-43.02, -42.01) * mm, "end": v(-24.26, -23.17) * mm});
            skLineSegment(sketch, "E782.0", {"start": v(-12.9, -42.37) * mm, "end": v(-32.03, -61.58) * mm});
            skCircle(sketch, "E783", {"center": v(92.25, -42.27) * mm, "radius": 10.04 * mm});
            skLineSegment(sketch, "E784", {"start": v(-15.59, -46.9) * mm, "end": v(-10.92, -42.22) * mm});
            skLineSegment(sketch, "E785", {"start": v(-26.96, -26.25) * mm, "end": v(-28.48, -24.74) * mm});
            skSolve(sketch);
        }
        {
            var Q0;
            Q0=qCreatedBy(makeId("Top.planeOp"),FACE);
            var sketch = newSketch(context, id + "F2", { "sketchPlane" : qUnion([Q0])});
            skPoint(sketch, "E786.0", {"position": v(-92.25, -2.02) * mm});
            skPoint(sketch, "E786.1", {"position": v(-92.25, -82.52) * mm});
            skPoint(sketch, "E786.2", {"position": v(92.25, -82.52) * mm});
            skPoint(sketch, "E786.3", {"position": v(92.25, -2.02) * mm});
            skLineSegment(sketch, "E787.bottom", {"start": v(90.75, -2.02) * mm, "end": v(-90.75, -2.02) * mm});
            skLineSegment(sketch, "E787.top", {"start": v(90.75, -82.52) * mm, "end": v(-90.75, -82.52) * mm});
            skLineSegment(sketch, "E787.left", {"start": v(92.25, -3.52) * mm, "end": v(92.25, -81.02) * mm});
            skLineSegment(sketch, "E787.right", {"start": v(-92.25, -3.52) * mm, "end": v(-92.25, -81.02) * mm});
            skLineSegment(sketch, "E788", {"start": v(92.25, -42.27) * mm, "end": v(-26.8, -42.27) * mm, "construction": true});
            skPoint(sketch, "E789.0", {"position": v(44.25, -42.27) * mm});
            skLineSegment(sketch, "E790", {"start": v(44.25, -82.52) * mm, "end": v(44.25, 4.93) * mm, "construction": true});
            skPoint(sketch, "E791", {"position": v(-28.1, -42.27) * mm});
            skArc(sketch, "E792", {"start": v(-26.8, -66.24) * mm, "mid": v(-11.13, -59.24) * mm, "end": v(-4.13, -43.57) * mm});
            skLineSegment(sketch, "E793.bottom", {"start": v(-28.1, -42.27) * mm, "end": v(-26.8, -42.27) * mm});
            skLineSegment(sketch, "E793.right", {"start": v(-26.8, -40.97) * mm, "end": v(-26.8, -18.3) * mm});
            skLineSegment(sketch, "E794.MirrorCS", {"start": v(-29.4, -40.97) * mm, "end": v(-29.4, -18.3) * mm});
            skLineSegment(sketch, "E795.MirrorCS", {"start": v(-26.8, -43.57) * mm, "end": v(-26.8, -66.24) * mm});
            skLineSegment(sketch, "E796.MirrorCS", {"start": v(-29.4, -43.57) * mm, "end": v(-29.4, -66.24) * mm});
            skLineSegment(sketch, "E797.trimOffspring", {"start": v(-4.13, -40.97) * mm, "end": v(-26.8, -40.97) * mm});
            skLineSegment(sketch, "E798.trimOffspring", {"start": v(-29.4, -40.97) * mm, "end": v(-52.06, -40.97) * mm});
            skLineSegment(sketch, "E799.MirrorCS", {"start": v(-4.13, -43.57) * mm, "end": v(-26.8, -43.57) * mm});
            skLineSegment(sketch, "E800.MirrorCS", {"start": v(-29.4, -43.57) * mm, "end": v(-52.06, -43.57) * mm});
            skPoint(sketch, "E801.orphan", {"position": v(-26.8, -42.27) * mm});
            skPoint(sketch, "E802.orphan", {"position": v(-29.4, -42.27) * mm});
            skPoint(sketch, "E803.orphan", {"position": v(-29.4, -17.27) * mm});
            skPoint(sketch, "E793.top.end.orphan", {"position": v(-26.8, -17.27) * mm});
            skPoint(sketch, "E804.orphan", {"position": v(-26.8, -67.27) * mm});
            skPoint(sketch, "E805.orphan", {"position": v(-29.4, -67.27) * mm});
            skArc(sketch, "E806.trimOffspring", {"start": v(-52.06, -43.57) * mm, "mid": v(-45.07, -59.24) * mm, "end": v(-29.4, -66.24) * mm});
            skArc(sketch, "E807.trimOffspring", {"start": v(-4.13, -40.97) * mm, "mid": v(-11.13, -25.3) * mm, "end": v(-26.8, -18.3) * mm});
            skArc(sketch, "E808.trimOffspring", {"start": v(-29.4, -18.3) * mm, "mid": v(-45.07, -25.3) * mm, "end": v(-52.06, -40.97) * mm});
            skLineSegment(sketch, "E809.trimOffspring", {"start": v(-29.4, -42.27) * mm, "end": v(-92.25, -42.27) * mm, "construction": true});
            skArc(sketch, "E810.filletArc", {"start": v(-90.75, -2.02) * mm, "mid": v(-91.81, -2.46) * mm, "end": v(-92.25, -3.52) * mm});
            skArc(sketch, "E811.filletArc", {"start": v(-92.25, -81.02) * mm, "mid": v(-91.81, -82.08) * mm, "end": v(-90.75, -82.52) * mm});
            skArc(sketch, "E812.filletArc", {"start": v(90.75, -82.52) * mm, "mid": v(91.81, -82.08) * mm, "end": v(92.25, -81.02) * mm});
            skArc(sketch, "E813.filletArc", {"start": v(92.25, -3.52) * mm, "mid": v(91.81, -2.46) * mm, "end": v(90.75, -2.02) * mm});
            skLineSegment(sketch, "E814.0.0", {"start": v(19.02, -21.02) * mm, "end": v(19.35, -21.02) * mm});
            skLineSegment(sketch, "E814.0.1", {"start": v(19.35, -21.02) * mm, "end": v(26.47, -21.02) * mm});
            skLineSegment(sketch, "E814.0.2", {"start": v(26.47, -21.02) * mm, "end": v(33.6, -21.02) * mm});
            skLineSegment(sketch, "E814.0.3", {"start": v(33.6, -21.02) * mm, "end": v(33.92, -21.02) * mm});
            skLineSegment(sketch, "E814.0.4", {"start": v(33.92, -21.02) * mm, "end": v(33.92, -20.11) * mm});
            skArc(sketch, "E814.0.5", {"start": v(33.92, -20.11) * mm, "mid": v(33.78, -20.03) * mm, "end": v(33.72, -19.87) * mm});
            skLineSegment(sketch, "E814.0.6", {"start": v(33.72, -19.87) * mm, "end": v(33.72, -19.67) * mm});
            skArc(sketch, "E814.0.7", {"start": v(33.72, -19.67) * mm, "mid": v(33.78, -19.5) * mm, "end": v(33.92, -19.42) * mm});
            skLineSegment(sketch, "E814.0.8", {"start": v(33.92, -19.42) * mm, "end": v(33.92, -18.52) * mm});
            skLineSegment(sketch, "E814.0.9", {"start": v(33.92, -18.52) * mm, "end": v(33.6, -18.52) * mm});
            skLineSegment(sketch, "E814.0.10", {"start": v(33.6, -18.52) * mm, "end": v(26.47, -18.52) * mm});
            skLineSegment(sketch, "E814.0.11", {"start": v(26.47, -18.52) * mm, "end": v(19.35, -18.52) * mm});
            skLineSegment(sketch, "E814.0.12", {"start": v(19.35, -18.52) * mm, "end": v(19.02, -18.52) * mm});
            skLineSegment(sketch, "E814.0.13", {"start": v(19.02, -18.52) * mm, "end": v(19.02, -19.42) * mm});
            skArc(sketch, "E814.0.14", {"start": v(19.02, -19.42) * mm, "mid": v(19.17, -19.5) * mm, "end": v(19.22, -19.67) * mm});
            skLineSegment(sketch, "E814.0.15", {"start": v(19.22, -19.67) * mm, "end": v(19.22, -19.87) * mm});
            skArc(sketch, "E814.0.16", {"start": v(19.22, -19.87) * mm, "mid": v(19.17, -20.03) * mm, "end": v(19.02, -20.11) * mm});
            skLineSegment(sketch, "E814.0.17", {"start": v(19.02, -20.11) * mm, "end": v(19.02, -21.02) * mm});
            skLineSegment(sketch, "E815.0.0", {"start": v(19.02, -66.02) * mm, "end": v(19.35, -66.02) * mm});
            skLineSegment(sketch, "E815.0.1", {"start": v(19.35, -66.02) * mm, "end": v(26.47, -66.02) * mm});
            skLineSegment(sketch, "E815.0.2", {"start": v(26.47, -66.02) * mm, "end": v(33.6, -66.02) * mm});
            skLineSegment(sketch, "E815.0.3", {"start": v(33.6, -66.02) * mm, "end": v(33.92, -66.02) * mm});
            skLineSegment(sketch, "E815.0.4", {"start": v(33.92, -66.02) * mm, "end": v(33.92, -65.11) * mm});
            skArc(sketch, "E815.0.5", {"start": v(33.92, -65.11) * mm, "mid": v(33.78, -65.03) * mm, "end": v(33.72, -64.87) * mm});
            skLineSegment(sketch, "E815.0.6", {"start": v(33.72, -64.87) * mm, "end": v(33.72, -64.67) * mm});
            skArc(sketch, "E815.0.7", {"start": v(33.72, -64.67) * mm, "mid": v(33.78, -64.5) * mm, "end": v(33.92, -64.42) * mm});
            skLineSegment(sketch, "E815.0.8", {"start": v(33.92, -64.42) * mm, "end": v(33.92, -63.52) * mm});
            skLineSegment(sketch, "E815.0.9", {"start": v(33.92, -63.52) * mm, "end": v(33.6, -63.52) * mm});
            skLineSegment(sketch, "E815.0.10", {"start": v(33.6, -63.52) * mm, "end": v(26.47, -63.52) * mm});
            skLineSegment(sketch, "E815.0.11", {"start": v(26.47, -63.52) * mm, "end": v(19.35, -63.52) * mm});
            skLineSegment(sketch, "E815.0.12", {"start": v(19.35, -63.52) * mm, "end": v(19.02, -63.52) * mm});
            skLineSegment(sketch, "E815.0.13", {"start": v(19.02, -63.52) * mm, "end": v(19.02, -64.42) * mm});
            skArc(sketch, "E815.0.14", {"start": v(19.02, -64.42) * mm, "mid": v(19.17, -64.5) * mm, "end": v(19.22, -64.67) * mm});
            skLineSegment(sketch, "E815.0.15", {"start": v(19.22, -64.67) * mm, "end": v(19.22, -64.87) * mm});
            skArc(sketch, "E815.0.16", {"start": v(19.22, -64.87) * mm, "mid": v(19.17, -65.03) * mm, "end": v(19.02, -65.11) * mm});
            skLineSegment(sketch, "E815.0.17", {"start": v(19.02, -65.11) * mm, "end": v(19.02, -66.02) * mm});
            skLineSegment(sketch, "E816.0.0", {"start": v(44.25, -12.27) * mm, "end": v(44.25, -13.77) * mm});
            skLineSegment(sketch, "E816.0.1", {"start": v(44.25, -13.77) * mm, "end": v(44.25, -42.27) * mm});
            skLineSegment(sketch, "E816.0.2", {"start": v(44.25, -42.27) * mm, "end": v(44.25, -70.77) * mm});
            skLineSegment(sketch, "E816.0.3", {"start": v(44.25, -70.77) * mm, "end": v(44.25, -72.27) * mm});
            skLineSegment(sketch, "E816.0.4", {"start": v(44.25, -72.27) * mm, "end": v(44.25, -72.82) * mm});
            skLineSegment(sketch, "E816.0.5", {"start": v(44.25, -72.82) * mm, "end": v(45.15, -72.82) * mm});
            skLineSegment(sketch, "E816.0.6", {"start": v(45.15, -72.82) * mm, "end": v(45.15, -72.27) * mm});
            skArc(sketch, "E816.0.7", {"start": v(45.15, -72.27) * mm, "mid": v(45.22, -72.1) * mm, "end": v(45.4, -72.02) * mm});
            skLineSegment(sketch, "E816.0.8", {"start": v(45.4, -72.02) * mm, "end": v(45.6, -72.02) * mm});
            skArc(sketch, "E816.0.9", {"start": v(45.6, -72.02) * mm, "mid": v(45.78, -72.1) * mm, "end": v(45.85, -72.27) * mm});
            skLineSegment(sketch, "E816.0.10", {"start": v(45.85, -72.27) * mm, "end": v(45.85, -72.82) * mm});
            skLineSegment(sketch, "E816.0.11", {"start": v(45.85, -72.82) * mm, "end": v(46.75, -72.82) * mm});
            skLineSegment(sketch, "E816.0.12", {"start": v(46.75, -72.82) * mm, "end": v(46.75, -72.27) * mm});
            skLineSegment(sketch, "E816.0.13", {"start": v(46.75, -72.27) * mm, "end": v(46.75, -70.77) * mm});
            skLineSegment(sketch, "E816.0.14", {"start": v(46.75, -70.77) * mm, "end": v(46.75, -42.27) * mm});
            skLineSegment(sketch, "E816.0.15", {"start": v(46.75, -42.27) * mm, "end": v(46.75, -13.77) * mm});
            skLineSegment(sketch, "E816.0.16", {"start": v(46.75, -13.77) * mm, "end": v(46.75, -12.27) * mm});
            skLineSegment(sketch, "E816.0.17", {"start": v(46.75, -12.27) * mm, "end": v(46.75, -11.72) * mm});
            skLineSegment(sketch, "E816.0.18", {"start": v(46.75, -11.72) * mm, "end": v(45.85, -11.72) * mm});
            skLineSegment(sketch, "E816.0.19", {"start": v(45.85, -11.72) * mm, "end": v(45.85, -12.27) * mm});
            skArc(sketch, "E816.0.20", {"start": v(45.85, -12.27) * mm, "mid": v(45.78, -12.45) * mm, "end": v(45.6, -12.52) * mm});
            skLineSegment(sketch, "E816.0.21", {"start": v(45.6, -12.52) * mm, "end": v(45.4, -12.52) * mm});
            skArc(sketch, "E816.0.22", {"start": v(45.4, -12.52) * mm, "mid": v(45.22, -12.45) * mm, "end": v(45.15, -12.27) * mm});
            skLineSegment(sketch, "E816.0.23", {"start": v(45.15, -12.27) * mm, "end": v(45.15, -11.72) * mm});
            skLineSegment(sketch, "E816.0.24", {"start": v(45.15, -11.72) * mm, "end": v(44.25, -11.72) * mm});
            skLineSegment(sketch, "E816.0.25", {"start": v(44.25, -11.72) * mm, "end": v(44.25, -12.27) * mm});
            skSolve(sketch);
        }
        {
            var Q0;
            Q0=qCreatedBy(makeId("Top.planeOp"),FACE);
            var sketch = newSketch(context, id + "F3", { "sketchPlane" : qUnion([Q0])});
            skPoint(sketch, "E817.0", {"position": v(-45.14, -42.3) * mm});
            skLineSegment(sketch, "E817.1", {"start": v(-45.14, -42.3) * mm, "end": v(-25.18, -22.25) * mm});
            skLineSegment(sketch, "E817.2", {"start": v(-26.96, -26.25) * mm, "end": v(-2.54, -50.57) * mm});
            skLineSegment(sketch, "E817.3", {"start": v(-28, -59.37) * mm, "end": v(-56.37, -31.13) * mm});
            skLineSegment(sketch, "E817.4", {"start": v(-15.59, -46.9) * mm, "end": v(-10.92, -42.22) * mm});
            skLineSegment(sketch, "E817.5", {"start": v(-11.98, -43.28) * mm, "end": v(-31.11, -62.5) * mm});
            skLineSegment(sketch, "E817.6", {"start": v(-21.38, -52.72) * mm, "end": v(-44.27, -29.92) * mm});
            skLineSegment(sketch, "E817.7", {"start": v(-17.42, -48.75) * mm, "end": v(-40.32, -25.95) * mm});
            skLineSegment(sketch, "E817.8", {"start": v(-15.59, -46.9) * mm, "end": v(-38.49, -24.11) * mm});
            skLineSegment(sketch, "E817.9", {"start": v(-23.2, -54.56) * mm, "end": v(-46.1, -31.76) * mm});
            skLineSegment(sketch, "E817.10", {"start": v(-33.83, -53.57) * mm, "end": v(-16.76, -36.42) * mm});
            skLineSegment(sketch, "E817.11", {"start": v(-35.67, -51.73) * mm, "end": v(-18.6, -34.58) * mm});
            skLineSegment(sketch, "E817.12", {"start": v(-37.52, -49.9) * mm, "end": v(-20.44, -32.75) * mm});
            skLineSegment(sketch, "E817.13", {"start": v(-39.36, -48.06) * mm, "end": v(-22.28, -30.91) * mm});
            skLineSegment(sketch, "E818.0", {"start": v(-26.96, -26.25) * mm, "end": v(-28.48, -24.74) * mm});
            skLineSegment(sketch, "E819.0", {"start": v(-43.02, -42.01) * mm, "end": v(-24.26, -23.17) * mm});
            skLineSegment(sketch, "E819.1", {"start": v(-12.9, -42.37) * mm, "end": v(-32.03, -61.58) * mm});
            skPoint(sketch, "E820.orphan", {"position": v(-39.33, -48.04) * mm});
            skPoint(sketch, "E821.orphan", {"position": v(-37.5, -49.87) * mm});
            skPoint(sketch, "E822.orphan", {"position": v(-35.65, -51.71) * mm});
            skPoint(sketch, "E823.orphan", {"position": v(-33.8, -53.55) * mm});
            skPoint(sketch, "E824.orphan", {"position": v(-16.78, -36.44) * mm});
            skPoint(sketch, "E825.orphan", {"position": v(-22.3, -30.93) * mm});
            skSolve(sketch);
        }
        {
            var Q0;
            {var subQ0=sQuery(id+"F3.wireOp",EDGE,"E818.0");var subQ1=sQuery(id+"F3.wireOp",EDGE,"E817.1");var subQ2=makeQuery(id+"F3.imprint","INTERSECT",VERTEX,{"derivedFrom":[subQ1,subQ0]});Q0=makeQuery(id+"F3.imprint","IMPRINT",FACE,{"disambiguationData":[TD([[makeQuery(id+"F3.imprint","IMPRINT",EDGE,{"disambiguationData":[TD([[subQ2,1.0]])],"derivedFrom":subQ1}),-1.0]])]});}
            var Q1;
            {var subQ1=sQuery(id+"F3.wireOp",EDGE,"E817.2");var subQ7=sQuery(id+"F3.wireOp",EDGE,"E818.0");var subQ8=makeQuery(id+"F3.imprint","INTERSECT",VERTEX,{"derivedFrom":[subQ1,subQ7]});Q1=makeQuery(id+"F3.imprint","IMPRINT",FACE,{"disambiguationData":[TD([[makeQuery(id+"F3.imprint","IMPRINT",EDGE,{"disambiguationData":[TD([[subQ8,-1.0]])],"derivedFrom":subQ1}),-1.0]])]});}
            var Q2;
            {var subQ0=sQuery(id+"F3.wireOp",EDGE,"E817.12");var subQ1=sQuery(id+"F3.wireOp",EDGE,"E817.2");var subQ2=makeQuery(id+"F3.imprint","INTERSECT",VERTEX,{"derivedFrom":[subQ1,subQ0]});Q2=makeQuery(id+"F3.imprint","IMPRINT",FACE,{"disambiguationData":[TD([[makeQuery(id+"F3.imprint","IMPRINT",EDGE,{"disambiguationData":[TD([[subQ2,1.0]])],"derivedFrom":subQ1}),-1.0]])]});}
            var Q3;
            {var subQ0=sQuery(id+"F3.wireOp",EDGE,"E817.10");var subQ1=sQuery(id+"F3.wireOp",EDGE,"E817.2");var subQ2=makeQuery(id+"F3.imprint","INTERSECT",VERTEX,{"derivedFrom":[subQ1,subQ0]});Q3=makeQuery(id+"F3.imprint","IMPRINT",FACE,{"disambiguationData":[TD([[makeQuery(id+"F3.imprint","IMPRINT",EDGE,{"disambiguationData":[TD([[subQ2,1.0]])],"derivedFrom":subQ1}),-1.0]])]});}
            var Q4;
            {var subQ1=sQuery(id+"F3.wireOp",EDGE,"E817.4");Q4=makeQuery(id+"F3.imprint","IMPRINT",FACE,{"disambiguationData":[TD([[makeQuery(id+"F3.imprint","IMPRINT",EDGE,{"derivedFrom":subQ1}),1.0]])]});}
            var Q5;
            {var subQ0=sQuery(id+"F3.wireOp",EDGE,"E817.5");var subQ1=sQuery(id+"F3.wireOp",EDGE,"E817.3");var subQ2=makeQuery(id+"F3.imprint","INTERSECT",VERTEX,{"derivedFrom":[subQ1,subQ0]});Q5=makeQuery(id+"F3.imprint","IMPRINT",FACE,{"disambiguationData":[TD([[makeQuery(id+"F3.imprint","IMPRINT",EDGE,{"disambiguationData":[TD([[subQ2,-1.0]])],"derivedFrom":subQ1}),-1.0]])]});}
            var Q6;
            {var subQ0=sQuery(id+"F3.wireOp",EDGE,"E819.1");var subQ1=sQuery(id+"F3.wireOp",EDGE,"E817.6");var subQ2=makeQuery(id+"F3.imprint","INTERSECT",VERTEX,{"derivedFrom":[subQ1,subQ0]});Q6=makeQuery(id+"F3.imprint","IMPRINT",FACE,{"disambiguationData":[TD([[makeQuery(id+"F3.imprint","IMPRINT",EDGE,{"disambiguationData":[TD([[subQ2,-1.0]])],"derivedFrom":subQ1}),-1.0]])]});}
            var Q7;
            {var subQ0=sQuery(id+"F3.wireOp",EDGE,"E819.1");var subQ1=sQuery(id+"F3.wireOp",EDGE,"E817.7");var subQ2=makeQuery(id+"F3.imprint","INTERSECT",VERTEX,{"derivedFrom":[subQ1,subQ0]});Q7=makeQuery(id+"F3.imprint","IMPRINT",FACE,{"disambiguationData":[TD([[makeQuery(id+"F3.imprint","IMPRINT",EDGE,{"disambiguationData":[TD([[subQ2,-1.0]])],"derivedFrom":subQ1}),-1.0]])]});}
            var Q8;
            {var subQ0=sQuery(id+"F3.wireOp",EDGE,"E819.1");var subQ1=sQuery(id+"F3.wireOp",EDGE,"E817.6");var subQ2=makeQuery(id+"F3.imprint","INTERSECT",VERTEX,{"derivedFrom":[subQ1,subQ0]});Q8=makeQuery(id+"F3.imprint","IMPRINT",FACE,{"disambiguationData":[TD([[makeQuery(id+"F3.imprint","IMPRINT",EDGE,{"disambiguationData":[TD([[subQ2,-1.0]])],"derivedFrom":subQ1}),1.0]])]});}
            var Q9;
            {var subQ0=sQuery(id+"F3.wireOp",EDGE,"E817.10");var subQ1=sQuery(id+"F3.wireOp",EDGE,"E817.3");var subQ2=makeQuery(id+"F3.imprint","INTERSECT",VERTEX,{"derivedFrom":[subQ1,subQ0]});Q9=makeQuery(id+"F3.imprint","IMPRINT",FACE,{"disambiguationData":[TD([[makeQuery(id+"F3.imprint","IMPRINT",EDGE,{"disambiguationData":[TD([[subQ2,1.0]])],"derivedFrom":subQ1}),-1.0]])]});}
            var Q10;
            {var subQ1=sQuery(id+"F3.wireOp",EDGE,"E817.1");var subQ6=sQuery(id+"F3.wireOp",EDGE,"E817.3");var subQ7=makeQuery(id+"F3.imprint","INTERSECT",VERTEX,{"derivedFrom":[subQ1,subQ6]});Q10=makeQuery(id+"F3.imprint","IMPRINT",FACE,{"disambiguationData":[TD([[makeQuery(id+"F3.imprint","IMPRINT",EDGE,{"disambiguationData":[TD([[subQ7,-1.0]])],"derivedFrom":subQ1}),-1.0]])]});}
            var Q11;
            {var subQ0=sQuery(id+"F3.wireOp",EDGE,"E817.13");var subQ1=sQuery(id+"F3.wireOp",EDGE,"E817.6");var subQ2=makeQuery(id+"F3.imprint","INTERSECT",VERTEX,{"derivedFrom":[subQ1,subQ0]});Q11=makeQuery(id+"F3.imprint","IMPRINT",FACE,{"disambiguationData":[TD([[makeQuery(id+"F3.imprint","IMPRINT",EDGE,{"disambiguationData":[TD([[subQ2,-1.0]])],"derivedFrom":subQ1}),-1.0]])]});}
            var Q12;
            {var subQ0=sQuery(id+"F3.wireOp",EDGE,"E817.13");var subQ1=sQuery(id+"F3.wireOp",EDGE,"E817.6");var subQ2=makeQuery(id+"F3.imprint","INTERSECT",VERTEX,{"derivedFrom":[subQ1,subQ0]});Q12=makeQuery(id+"F3.imprint","IMPRINT",FACE,{"disambiguationData":[TD([[makeQuery(id+"F3.imprint","IMPRINT",EDGE,{"disambiguationData":[TD([[subQ2,-1.0]])],"derivedFrom":subQ1}),1.0]])]});}
            var Q13;
            {var subQ0=sQuery(id+"F3.wireOp",EDGE,"E817.12");var subQ1=sQuery(id+"F3.wireOp",EDGE,"E817.3");var subQ2=makeQuery(id+"F3.imprint","INTERSECT",VERTEX,{"derivedFrom":[subQ1,subQ0]});Q13=makeQuery(id+"F3.imprint","IMPRINT",FACE,{"disambiguationData":[TD([[makeQuery(id+"F3.imprint","IMPRINT",EDGE,{"disambiguationData":[TD([[subQ2,-1.0]])],"derivedFrom":subQ1}),-1.0]])]});}
            var Q14;
            {var subQ0=sQuery(id+"F3.wireOp",EDGE,"E817.10");var subQ1=sQuery(id+"F3.wireOp",EDGE,"E817.3");var subQ2=makeQuery(id+"F3.imprint","INTERSECT",VERTEX,{"derivedFrom":[subQ1,subQ0]});Q14=makeQuery(id+"F3.imprint","IMPRINT",FACE,{"disambiguationData":[TD([[makeQuery(id+"F3.imprint","IMPRINT",EDGE,{"disambiguationData":[TD([[subQ2,-1.0]])],"derivedFrom":subQ1}),-1.0]])]});}
            var Q15;
            {var subQ0=sQuery(id+"F3.wireOp",EDGE,"E817.13");var subQ1=sQuery(id+"F3.wireOp",EDGE,"E817.7");var subQ2=makeQuery(id+"F3.imprint","INTERSECT",VERTEX,{"derivedFrom":[subQ1,subQ0]});Q15=makeQuery(id+"F3.imprint","IMPRINT",FACE,{"disambiguationData":[TD([[makeQuery(id+"F3.imprint","IMPRINT",EDGE,{"disambiguationData":[TD([[subQ2,-1.0]])],"derivedFrom":subQ1}),-1.0]])]});}
            var Q16;
            {var subQ0=sQuery(id+"F3.wireOp",EDGE,"E817.12");var subQ1=sQuery(id+"F3.wireOp",EDGE,"E817.6");var subQ2=makeQuery(id+"F3.imprint","INTERSECT",VERTEX,{"derivedFrom":[subQ1,subQ0]});Q16=makeQuery(id+"F3.imprint","IMPRINT",FACE,{"disambiguationData":[TD([[makeQuery(id+"F3.imprint","IMPRINT",EDGE,{"disambiguationData":[TD([[subQ2,-1.0]])],"derivedFrom":subQ1}),-1.0]])]});}
            var Q17;
            {var subQ0=sQuery(id+"F3.wireOp",EDGE,"E817.11");var subQ1=sQuery(id+"F3.wireOp",EDGE,"E817.6");var subQ2=makeQuery(id+"F3.imprint","INTERSECT",VERTEX,{"derivedFrom":[subQ1,subQ0]});Q17=makeQuery(id+"F3.imprint","IMPRINT",FACE,{"disambiguationData":[TD([[makeQuery(id+"F3.imprint","IMPRINT",EDGE,{"disambiguationData":[TD([[subQ2,-1.0]])],"derivedFrom":subQ1}),-1.0]])]});}
            var Q18;
            {var subQ0=sQuery(id+"F3.wireOp",EDGE,"E817.10");var subQ1=sQuery(id+"F3.wireOp",EDGE,"E817.6");var subQ2=makeQuery(id+"F3.imprint","INTERSECT",VERTEX,{"derivedFrom":[subQ1,subQ0]});Q18=makeQuery(id+"F3.imprint","IMPRINT",FACE,{"disambiguationData":[TD([[makeQuery(id+"F3.imprint","IMPRINT",EDGE,{"disambiguationData":[TD([[subQ2,-1.0]])],"derivedFrom":subQ1}),-1.0]])]});}
            extrude(context, id + "F4", {"entities" : qUnion([Q0, Q1, Q2, Q3, Q4, Q5, Q6, Q7, Q8, Q9, Q10, Q11, Q12, Q13, Q14, Q15, Q16, Q17, Q18]), "depth" : (getVariable(context, 'Thickness')) * mm, "offsetDistance" : 25 * mm});
        }
        {
            var Q0;
            Q0=makeQuery(id+"F2.imprint","IMPRINT",FACE,{"disambiguationData":[TD([[makeQuery(id+"F2.imprint","IMPRINT",EDGE,{"derivedFrom":sQuery(id+"F2.wireOp",EDGE,"E787.bottom")}),1.0]])]});
            extrude(context, id + "F5", {"entities" : qUnion([Q0]), "depth" : (getVariable(context, 'Thickness')) * mm, "offsetDistance" : 25 * mm});
        }
        {
            var Q0;
            Q0=makeQuery(id+"F4.opExtrude","SWEPT_BODY",BODY,{"disambiguationData":[OSD([sQuery(id+"F3.wireOp",EDGE,"E817.1"),sQuery(id+"F3.wireOp",EDGE,"E817.2"),sQuery(id+"F3.wireOp",EDGE,"E817.3"),sQuery(id+"F3.wireOp",EDGE,"E817.4"),sQuery(id+"F3.wireOp",EDGE,"E817.5"),sQuery(id+"F3.wireOp",EDGE,"E817.6"),sQuery(id+"F3.wireOp",EDGE,"E817.7"),sQuery(id+"F3.wireOp",EDGE,"E817.8"),sQuery(id+"F3.wireOp",EDGE,"E817.9"),sQuery(id+"F3.wireOp",EDGE,"E817.10"),sQuery(id+"F3.wireOp",EDGE,"E817.11"),sQuery(id+"F3.wireOp",EDGE,"E817.12"),sQuery(id+"F3.wireOp",EDGE,"E817.13"),sQuery(id+"F3.wireOp",EDGE,"E818.0"),sQuery(id+"F3.wireOp",EDGE,"E819.0"),sQuery(id+"F3.wireOp",EDGE,"E819.1")])]});
            var Q1;
            Q1=makeQuery(id+"F5.opExtrude","SWEPT_BODY",BODY,{"disambiguationData":[OSD([sQuery(id+"F2.wireOp",EDGE,"E787.bottom"),sQuery(id+"F2.wireOp",EDGE,"E787.top"),sQuery(id+"F2.wireOp",EDGE,"E787.left"),sQuery(id+"F2.wireOp",EDGE,"E787.right"),sQuery(id+"F2.wireOp",EDGE,"E792"),sQuery(id+"F2.wireOp",EDGE,"E793.right"),sQuery(id+"F2.wireOp",EDGE,"E794.MirrorCS"),sQuery(id+"F2.wireOp",EDGE,"E795.MirrorCS"),sQuery(id+"F2.wireOp",EDGE,"E796.MirrorCS"),sQuery(id+"F2.wireOp",EDGE,"E797.trimOffspring"),sQuery(id+"F2.wireOp",EDGE,"E798.trimOffspring"),sQuery(id+"F2.wireOp",EDGE,"E799.MirrorCS"),sQuery(id+"F2.wireOp",EDGE,"E800.MirrorCS"),sQuery(id+"F2.wireOp",EDGE,"E806.trimOffspring"),sQuery(id+"F2.wireOp",EDGE,"E807.trimOffspring"),sQuery(id+"F2.wireOp",EDGE,"E808.trimOffspring"),sQuery(id+"F2.wireOp",EDGE,"E810.filletArc"),sQuery(id+"F2.wireOp",EDGE,"E811.filletArc"),sQuery(id+"F2.wireOp",EDGE,"E812.filletArc"),sQuery(id+"F2.wireOp",EDGE,"E813.filletArc")])]});
            booleanBodies(context, id + "F6", {"operationType" : BooleanOperationType.SUBTRACTION, "tools" : qUnion([Q0]), "targets" : qUnion([Q1]), "keepTools" : true});
        }
        {
            var Q0;
            Q0=makeQuery(id+"F6.opBoolean","SPLIT",BODY,{"disambiguationData":[OD(1.0)],"derivedFrom":makeQuery(id+"F5.opExtrude","SWEPT_BODY",BODY,{"disambiguationData":[OSD([sQuery(id+"F2.wireOp",EDGE,"E787.bottom"),sQuery(id+"F2.wireOp",EDGE,"E787.top"),sQuery(id+"F2.wireOp",EDGE,"E787.left"),sQuery(id+"F2.wireOp",EDGE,"E787.right"),sQuery(id+"F2.wireOp",EDGE,"E792"),sQuery(id+"F2.wireOp",EDGE,"E793.right"),sQuery(id+"F2.wireOp",EDGE,"E794.MirrorCS"),sQuery(id+"F2.wireOp",EDGE,"E795.MirrorCS"),sQuery(id+"F2.wireOp",EDGE,"E796.MirrorCS"),sQuery(id+"F2.wireOp",EDGE,"E797.trimOffspring"),sQuery(id+"F2.wireOp",EDGE,"E798.trimOffspring"),sQuery(id+"F2.wireOp",EDGE,"E799.MirrorCS"),sQuery(id+"F2.wireOp",EDGE,"E800.MirrorCS"),sQuery(id+"F2.wireOp",EDGE,"E806.trimOffspring"),sQuery(id+"F2.wireOp",EDGE,"E807.trimOffspring"),sQuery(id+"F2.wireOp",EDGE,"E808.trimOffspring"),sQuery(id+"F2.wireOp",EDGE,"E810.filletArc"),sQuery(id+"F2.wireOp",EDGE,"E811.filletArc"),sQuery(id+"F2.wireOp",EDGE,"E812.filletArc"),sQuery(id+"F2.wireOp",EDGE,"E813.filletArc")])]})});
            var Q1;
            Q1=makeQuery(id+"F6.opBoolean","SPLIT",BODY,{"disambiguationData":[OD(0.0)],"derivedFrom":makeQuery(id+"F5.opExtrude","SWEPT_BODY",BODY,{"disambiguationData":[OSD([sQuery(id+"F2.wireOp",EDGE,"E787.bottom"),sQuery(id+"F2.wireOp",EDGE,"E787.top"),sQuery(id+"F2.wireOp",EDGE,"E787.left"),sQuery(id+"F2.wireOp",EDGE,"E787.right"),sQuery(id+"F2.wireOp",EDGE,"E792"),sQuery(id+"F2.wireOp",EDGE,"E793.right"),sQuery(id+"F2.wireOp",EDGE,"E794.MirrorCS"),sQuery(id+"F2.wireOp",EDGE,"E795.MirrorCS"),sQuery(id+"F2.wireOp",EDGE,"E796.MirrorCS"),sQuery(id+"F2.wireOp",EDGE,"E797.trimOffspring"),sQuery(id+"F2.wireOp",EDGE,"E798.trimOffspring"),sQuery(id+"F2.wireOp",EDGE,"E799.MirrorCS"),sQuery(id+"F2.wireOp",EDGE,"E800.MirrorCS"),sQuery(id+"F2.wireOp",EDGE,"E806.trimOffspring"),sQuery(id+"F2.wireOp",EDGE,"E807.trimOffspring"),sQuery(id+"F2.wireOp",EDGE,"E808.trimOffspring"),sQuery(id+"F2.wireOp",EDGE,"E810.filletArc"),sQuery(id+"F2.wireOp",EDGE,"E811.filletArc"),sQuery(id+"F2.wireOp",EDGE,"E812.filletArc"),sQuery(id+"F2.wireOp",EDGE,"E813.filletArc")])]})});
            var Q2;
            Q2=makeQuery(id+"F6.opBoolean","SPLIT",BODY,{"disambiguationData":[OD(2.0)],"derivedFrom":makeQuery(id+"F5.opExtrude","SWEPT_BODY",BODY,{"disambiguationData":[OSD([sQuery(id+"F2.wireOp",EDGE,"E787.bottom"),sQuery(id+"F2.wireOp",EDGE,"E787.top"),sQuery(id+"F2.wireOp",EDGE,"E787.left"),sQuery(id+"F2.wireOp",EDGE,"E787.right"),sQuery(id+"F2.wireOp",EDGE,"E792"),sQuery(id+"F2.wireOp",EDGE,"E793.right"),sQuery(id+"F2.wireOp",EDGE,"E794.MirrorCS"),sQuery(id+"F2.wireOp",EDGE,"E795.MirrorCS"),sQuery(id+"F2.wireOp",EDGE,"E796.MirrorCS"),sQuery(id+"F2.wireOp",EDGE,"E797.trimOffspring"),sQuery(id+"F2.wireOp",EDGE,"E798.trimOffspring"),sQuery(id+"F2.wireOp",EDGE,"E799.MirrorCS"),sQuery(id+"F2.wireOp",EDGE,"E800.MirrorCS"),sQuery(id+"F2.wireOp",EDGE,"E806.trimOffspring"),sQuery(id+"F2.wireOp",EDGE,"E807.trimOffspring"),sQuery(id+"F2.wireOp",EDGE,"E808.trimOffspring"),sQuery(id+"F2.wireOp",EDGE,"E810.filletArc"),sQuery(id+"F2.wireOp",EDGE,"E811.filletArc"),sQuery(id+"F2.wireOp",EDGE,"E812.filletArc"),sQuery(id+"F2.wireOp",EDGE,"E813.filletArc")])]})});
            var Q3;
            Q3=makeQuery(id+"F6.opBoolean","SPLIT",BODY,{"disambiguationData":[OD(3.0)],"derivedFrom":makeQuery(id+"F5.opExtrude","SWEPT_BODY",BODY,{"disambiguationData":[OSD([sQuery(id+"F2.wireOp",EDGE,"E787.bottom"),sQuery(id+"F2.wireOp",EDGE,"E787.top"),sQuery(id+"F2.wireOp",EDGE,"E787.left"),sQuery(id+"F2.wireOp",EDGE,"E787.right"),sQuery(id+"F2.wireOp",EDGE,"E792"),sQuery(id+"F2.wireOp",EDGE,"E793.right"),sQuery(id+"F2.wireOp",EDGE,"E794.MirrorCS"),sQuery(id+"F2.wireOp",EDGE,"E795.MirrorCS"),sQuery(id+"F2.wireOp",EDGE,"E796.MirrorCS"),sQuery(id+"F2.wireOp",EDGE,"E797.trimOffspring"),sQuery(id+"F2.wireOp",EDGE,"E798.trimOffspring"),sQuery(id+"F2.wireOp",EDGE,"E799.MirrorCS"),sQuery(id+"F2.wireOp",EDGE,"E800.MirrorCS"),sQuery(id+"F2.wireOp",EDGE,"E806.trimOffspring"),sQuery(id+"F2.wireOp",EDGE,"E807.trimOffspring"),sQuery(id+"F2.wireOp",EDGE,"E808.trimOffspring"),sQuery(id+"F2.wireOp",EDGE,"E810.filletArc"),sQuery(id+"F2.wireOp",EDGE,"E811.filletArc"),sQuery(id+"F2.wireOp",EDGE,"E812.filletArc"),sQuery(id+"F2.wireOp",EDGE,"E813.filletArc")])]})});
            deleteBodies(context, id + "F7", {"entities" : qUnion([Q0, Q1, Q2, Q3])});
        }
        {
            var Q0;
            Q0=qCreatedBy(makeId("Top.planeOp"),FACE);
            var sketch = newSketch(context, id + "F8", { "sketchPlane" : qUnion([Q0])});
            skLineSegment(sketch, "E826.0", {"start": v(-86.07, 36.09) * mm, "end": v(-49.81, 5.26) * mm});
            skLineSegment(sketch, "E826.1", {"start": v(-49.97, 4.82) * mm, "end": v(-60.63, 4.82) * mm});
            skLineSegment(sketch, "E826.2", {"start": v(-76.53, 4.82) * mm, "end": v(-86.23, 4.82) * mm});
            skLineSegment(sketch, "E826.3", {"start": v(-86.48, 5.07) * mm, "end": v(-86.48, 14.8) * mm});
            skLineSegment(sketch, "E826.4", {"start": v(-86.48, 30.7) * mm, "end": v(-86.48, 35.9) * mm});
            skLineSegment(sketch, "E826.5", {"start": v(-89.48, 22.75) * mm, "end": v(-89.48, 29.87) * mm});
            skLineSegment(sketch, "E826.6", {"start": v(-89.48, 15.62) * mm, "end": v(-89.48, 22.75) * mm});
            skLineSegment(sketch, "E826.7", {"start": v(-68.58, 1.82) * mm, "end": v(-75.7, 1.82) * mm});
            skLineSegment(sketch, "E826.8", {"start": v(-61.46, 1.82) * mm, "end": v(-68.58, 1.82) * mm});
            skArc(sketch, "E827.0.0", {"start": v(-86.07, 36.09) * mm, "mid": v(-86.33, 36.12) * mm, "end": v(-86.48, 35.9) * mm});
            skLineSegment(sketch, "E827.0.1", {"start": v(-86.48, 35.9) * mm, "end": v(-86.48, 30.7) * mm});
            skLineSegment(sketch, "E827.0.2", {"start": v(-86.48, 30.7) * mm, "end": v(-87.63, 30.7) * mm});
            skArc(sketch, "E827.0.3", {"start": v(-87.63, 30.7) * mm, "mid": v(-87.68, 30.7) * mm, "end": v(-87.73, 30.68) * mm});
            skArc(sketch, "E827.0.4", {"start": v(-87.73, 30.68) * mm, "mid": v(-87.78, 30.7) * mm, "end": v(-87.83, 30.7) * mm});
            skLineSegment(sketch, "E827.0.5", {"start": v(-87.83, 30.7) * mm, "end": v(-89.23, 30.7) * mm});
            skArc(sketch, "E827.0.6", {"start": v(-89.23, 30.7) * mm, "mid": v(-89.4, 30.63) * mm, "end": v(-89.48, 30.45) * mm});
            skLineSegment(sketch, "E827.0.7", {"start": v(-89.48, 30.45) * mm, "end": v(-89.48, 30.25) * mm});
            skLineSegment(sketch, "E827.0.8", {"start": v(-89.48, 30.25) * mm, "end": v(-89.48, 29.87) * mm});
            skLineSegment(sketch, "E827.0.9", {"start": v(-89.48, 29.87) * mm, "end": v(-89.48, 22.75) * mm});
            skLineSegment(sketch, "E827.0.10", {"start": v(-89.48, 22.75) * mm, "end": v(-89.48, 15.62) * mm});
            skLineSegment(sketch, "E827.0.11", {"start": v(-89.48, 15.62) * mm, "end": v(-89.48, 15.25) * mm});
            skLineSegment(sketch, "E827.0.12", {"start": v(-89.48, 15.25) * mm, "end": v(-89.48, 15.05) * mm});
            skArc(sketch, "E827.0.13", {"start": v(-89.48, 15.05) * mm, "mid": v(-89.4, 14.87) * mm, "end": v(-89.23, 14.8) * mm});
            skLineSegment(sketch, "E827.0.14", {"start": v(-89.23, 14.8) * mm, "end": v(-87.83, 14.8) * mm});
            skArc(sketch, "E827.0.15", {"start": v(-87.83, 14.8) * mm, "mid": v(-87.78, 14.8) * mm, "end": v(-87.73, 14.82) * mm});
            skArc(sketch, "E827.0.16", {"start": v(-87.73, 14.82) * mm, "mid": v(-87.68, 14.8) * mm, "end": v(-87.63, 14.8) * mm});
            skLineSegment(sketch, "E827.0.17", {"start": v(-87.63, 14.8) * mm, "end": v(-86.48, 14.8) * mm});
            skLineSegment(sketch, "E827.0.18", {"start": v(-86.48, 14.8) * mm, "end": v(-86.48, 5.07) * mm});
            skArc(sketch, "E827.0.19", {"start": v(-86.48, 5.07) * mm, "mid": v(-86.4, 4.9) * mm, "end": v(-86.23, 4.82) * mm});
            skLineSegment(sketch, "E827.0.20", {"start": v(-86.23, 4.82) * mm, "end": v(-76.53, 4.82) * mm});
            skLineSegment(sketch, "E827.0.21", {"start": v(-76.53, 4.82) * mm, "end": v(-76.53, 3.67) * mm});
            skArc(sketch, "E827.0.22", {"start": v(-76.53, 3.67) * mm, "mid": v(-76.53, 3.62) * mm, "end": v(-76.51, 3.57) * mm});
            skArc(sketch, "E827.0.23", {"start": v(-76.51, 3.57) * mm, "mid": v(-76.53, 3.52) * mm, "end": v(-76.53, 3.47) * mm});
            skLineSegment(sketch, "E827.0.24", {"start": v(-76.53, 3.47) * mm, "end": v(-76.53, 2.07) * mm});
            skArc(sketch, "E827.0.25", {"start": v(-76.53, 2.07) * mm, "mid": v(-76.46, 1.9) * mm, "end": v(-76.28, 1.82) * mm});
            skLineSegment(sketch, "E827.0.26", {"start": v(-76.28, 1.82) * mm, "end": v(-76.08, 1.82) * mm});
            skLineSegment(sketch, "E827.0.27", {"start": v(-76.08, 1.82) * mm, "end": v(-75.7, 1.82) * mm});
            skLineSegment(sketch, "E827.0.28", {"start": v(-75.7, 1.82) * mm, "end": v(-68.58, 1.82) * mm});
            skLineSegment(sketch, "E827.0.29", {"start": v(-68.58, 1.82) * mm, "end": v(-61.46, 1.82) * mm});
            skLineSegment(sketch, "E827.0.30", {"start": v(-61.46, 1.82) * mm, "end": v(-61.08, 1.82) * mm});
            skLineSegment(sketch, "E827.0.31", {"start": v(-61.08, 1.82) * mm, "end": v(-60.88, 1.82) * mm});
            skArc(sketch, "E827.0.32", {"start": v(-60.88, 1.82) * mm, "mid": v(-60.7, 1.9) * mm, "end": v(-60.63, 2.07) * mm});
            skLineSegment(sketch, "E827.0.33", {"start": v(-60.63, 2.07) * mm, "end": v(-60.63, 3.47) * mm});
            skArc(sketch, "E827.0.34", {"start": v(-60.63, 3.47) * mm, "mid": v(-60.64, 3.52) * mm, "end": v(-60.65, 3.57) * mm});
            skArc(sketch, "E827.0.35", {"start": v(-60.65, 3.57) * mm, "mid": v(-60.64, 3.62) * mm, "end": v(-60.63, 3.67) * mm});
            skLineSegment(sketch, "E827.0.36", {"start": v(-60.63, 3.67) * mm, "end": v(-60.63, 4.82) * mm});
            skLineSegment(sketch, "E827.0.37", {"start": v(-60.63, 4.82) * mm, "end": v(-49.97, 4.82) * mm});
            skArc(sketch, "E827.0.38", {"start": v(-49.97, 4.82) * mm, "mid": v(-49.74, 4.99) * mm, "end": v(-49.81, 5.26) * mm});
            skLineSegment(sketch, "E827.0.39", {"start": v(-49.81, 5.26) * mm, "end": v(-86.07, 36.09) * mm});
            skSolve(sketch);
        }
        {
            var Q0;
            Q0=makeQuery(id+"F8.imprint","IMPRINT",FACE,{"disambiguationData":[TD([[makeQuery(id+"F8.imprint","IMPRINT",EDGE,{"derivedFrom":sQuery(id+"F8.wireOp",EDGE,"E827.0.0")}),1.0]])]});
            extrude(context, id + "F9", {"entities" : qUnion([Q0]), "depth" : (getVariable(context, 'Thickness')) * mm, "offsetDistance" : 25 * mm});
        }
        {
            var Q0;
            Q0=qCreatedBy(makeId("Top.planeOp"),FACE);
            var sketch = newSketch(context, id + "F10", { "sketchPlane" : qUnion([Q0])});
            skLineSegment(sketch, "E828.0.0", {"start": v(-66.43, 39.24) * mm, "end": v(-71.62, 39.24) * mm});
            skArc(sketch, "E828.0.1", {"start": v(-71.62, 39.24) * mm, "mid": v(-71.85, 39.1) * mm, "end": v(-71.81, 38.83) * mm});
            skLineSegment(sketch, "E828.0.2", {"start": v(-71.81, 38.83) * mm, "end": v(-40.99, 2.58) * mm});
            skArc(sketch, "E828.0.3", {"start": v(-40.99, 2.58) * mm, "mid": v(-40.71, 2.5) * mm, "end": v(-40.55, 2.74) * mm});
            skLineSegment(sketch, "E828.0.4", {"start": v(-40.55, 2.74) * mm, "end": v(-40.55, 13.4) * mm});
            skLineSegment(sketch, "E828.0.5", {"start": v(-40.55, 13.4) * mm, "end": v(-39.4, 13.4) * mm});
            skArc(sketch, "E828.0.6", {"start": v(-39.4, 13.4) * mm, "mid": v(-39.35, 13.4) * mm, "end": v(-39.3, 13.42) * mm});
            skArc(sketch, "E828.0.7", {"start": v(-39.3, 13.42) * mm, "mid": v(-39.25, 13.4) * mm, "end": v(-39.2, 13.4) * mm});
            skLineSegment(sketch, "E828.0.8", {"start": v(-39.2, 13.4) * mm, "end": v(-37.8, 13.4) * mm});
            skArc(sketch, "E828.0.9", {"start": v(-37.8, 13.4) * mm, "mid": v(-37.62, 13.47) * mm, "end": v(-37.55, 13.65) * mm});
            skLineSegment(sketch, "E828.0.10", {"start": v(-37.55, 13.65) * mm, "end": v(-37.55, 13.85) * mm});
            skLineSegment(sketch, "E828.0.11", {"start": v(-37.55, 13.85) * mm, "end": v(-37.55, 14.22) * mm});
            skLineSegment(sketch, "E828.0.12", {"start": v(-37.55, 14.22) * mm, "end": v(-37.55, 21.35) * mm});
            skLineSegment(sketch, "E828.0.13", {"start": v(-37.55, 21.35) * mm, "end": v(-37.55, 28.47) * mm});
            skLineSegment(sketch, "E828.0.14", {"start": v(-37.55, 28.47) * mm, "end": v(-37.55, 28.85) * mm});
            skLineSegment(sketch, "E828.0.15", {"start": v(-37.55, 28.85) * mm, "end": v(-37.55, 29.05) * mm});
            skArc(sketch, "E828.0.16", {"start": v(-37.55, 29.05) * mm, "mid": v(-37.62, 29.22) * mm, "end": v(-37.8, 29.3) * mm});
            skLineSegment(sketch, "E828.0.17", {"start": v(-37.8, 29.3) * mm, "end": v(-39.2, 29.3) * mm});
            skArc(sketch, "E828.0.18", {"start": v(-39.2, 29.3) * mm, "mid": v(-39.25, 29.3) * mm, "end": v(-39.3, 29.28) * mm});
            skArc(sketch, "E828.0.19", {"start": v(-39.3, 29.28) * mm, "mid": v(-39.35, 29.3) * mm, "end": v(-39.4, 29.3) * mm});
            skLineSegment(sketch, "E828.0.20", {"start": v(-39.4, 29.3) * mm, "end": v(-40.55, 29.3) * mm});
            skLineSegment(sketch, "E828.0.21", {"start": v(-40.55, 29.3) * mm, "end": v(-40.55, 39) * mm});
            skArc(sketch, "E828.0.22", {"start": v(-40.55, 39) * mm, "mid": v(-40.62, 39.17) * mm, "end": v(-40.8, 39.24) * mm});
            skLineSegment(sketch, "E828.0.23", {"start": v(-40.8, 39.24) * mm, "end": v(-50.53, 39.24) * mm});
            skLineSegment(sketch, "E828.0.24", {"start": v(-50.53, 39.24) * mm, "end": v(-50.53, 40.4) * mm});
            skArc(sketch, "E828.0.25", {"start": v(-50.53, 40.4) * mm, "mid": v(-50.53, 40.44) * mm, "end": v(-50.55, 40.5) * mm});
            skArc(sketch, "E828.0.26", {"start": v(-50.55, 40.5) * mm, "mid": v(-50.53, 40.54) * mm, "end": v(-50.53, 40.6) * mm});
            skLineSegment(sketch, "E828.0.27", {"start": v(-50.53, 40.6) * mm, "end": v(-50.53, 42) * mm});
            skArc(sketch, "E828.0.28", {"start": v(-50.53, 42) * mm, "mid": v(-50.6, 42.17) * mm, "end": v(-50.78, 42.24) * mm});
            skLineSegment(sketch, "E828.0.29", {"start": v(-50.78, 42.24) * mm, "end": v(-50.98, 42.24) * mm});
            skLineSegment(sketch, "E828.0.30", {"start": v(-50.98, 42.24) * mm, "end": v(-51.35, 42.24) * mm});
            skLineSegment(sketch, "E828.0.31", {"start": v(-51.35, 42.24) * mm, "end": v(-58.48, 42.24) * mm});
            skLineSegment(sketch, "E828.0.32", {"start": v(-58.48, 42.24) * mm, "end": v(-65.6, 42.24) * mm});
            skLineSegment(sketch, "E828.0.33", {"start": v(-65.6, 42.24) * mm, "end": v(-65.98, 42.24) * mm});
            skLineSegment(sketch, "E828.0.34", {"start": v(-65.98, 42.24) * mm, "end": v(-66.18, 42.24) * mm});
            skArc(sketch, "E828.0.35", {"start": v(-66.18, 42.24) * mm, "mid": v(-66.35, 42.17) * mm, "end": v(-66.43, 42) * mm});
            skLineSegment(sketch, "E828.0.36", {"start": v(-66.43, 42) * mm, "end": v(-66.43, 40.6) * mm});
            skArc(sketch, "E828.0.37", {"start": v(-66.43, 40.6) * mm, "mid": v(-66.42, 40.54) * mm, "end": v(-66.4, 40.5) * mm});
            skArc(sketch, "E828.0.38", {"start": v(-66.4, 40.5) * mm, "mid": v(-66.42, 40.44) * mm, "end": v(-66.43, 40.4) * mm});
            skLineSegment(sketch, "E828.0.39", {"start": v(-66.43, 40.4) * mm, "end": v(-66.43, 39.24) * mm});
            skSolve(sketch);
        }
        {
            var Q0;
            Q0=makeQuery(id+"F10.imprint","IMPRINT",FACE,{"disambiguationData":[TD([[makeQuery(id+"F10.imprint","IMPRINT",EDGE,{"derivedFrom":sQuery(id+"F10.wireOp",EDGE,"E828.0.0")}),1.0]])]});
            extrude(context, id + "F11", {"entities" : qUnion([Q0]), "depth" : (getVariable(context, 'Thickness')) * mm, "offsetDistance" : 25 * mm});
        }
        {
            var Q0;
            Q0=qCreatedBy(makeId("Top.planeOp"),FACE);
            var sketch = newSketch(context, id + "F12", { "sketchPlane" : qUnion([Q0])});
            skArc(sketch, "E829.0.0", {"start": v(89.13, 2.02) * mm, "mid": v(90.72, 2.68) * mm, "end": v(91.38, 4.27) * mm});
            skLineSegment(sketch, "E829.0.1", {"start": v(91.38, 4.27) * mm, "end": v(91.38, 30.43) * mm});
            skArc(sketch, "E829.0.2", {"start": v(91.38, 30.43) * mm, "mid": v(90.72, 32.02) * mm, "end": v(89.13, 32.68) * mm});
            skLineSegment(sketch, "E829.0.3", {"start": v(89.13, 32.68) * mm, "end": v(78.24, 32.68) * mm});
            skLineSegment(sketch, "E829.0.4", {"start": v(78.24, 32.68) * mm, "end": v(76.24, 32.68) * mm});
            skArc(sketch, "E829.0.5", {"start": v(76.24, 32.68) * mm, "mid": v(75, 33.2) * mm, "end": v(74.5, 34.43) * mm});
            skLineSegment(sketch, "E829.0.6", {"start": v(74.5, 34.43) * mm, "end": v(74.5, 50.54) * mm});
            skArc(sketch, "E829.0.7", {"start": v(74.5, 50.54) * mm, "mid": v(75, 51.78) * mm, "end": v(76.24, 52.3) * mm});
            skLineSegment(sketch, "E829.0.8", {"start": v(76.24, 52.3) * mm, "end": v(78.24, 52.3) * mm});
            skLineSegment(sketch, "E829.0.9", {"start": v(78.24, 52.3) * mm, "end": v(89.13, 52.3) * mm});
            skArc(sketch, "E829.0.10", {"start": v(89.13, 52.3) * mm, "mid": v(90.72, 52.95) * mm, "end": v(91.38, 54.54) * mm});
            skLineSegment(sketch, "E829.0.11", {"start": v(91.38, 54.54) * mm, "end": v(91.38, 80.27) * mm});
            skArc(sketch, "E829.0.12", {"start": v(91.38, 80.27) * mm, "mid": v(90.72, 81.86) * mm, "end": v(89.13, 82.52) * mm});
            skLineSegment(sketch, "E829.0.13", {"start": v(89.13, 82.52) * mm, "end": v(74.24, 82.52) * mm});
            skArc(sketch, "E829.0.14", {"start": v(74.24, 82.52) * mm, "mid": v(74.07, 82.45) * mm, "end": v(74, 82.27) * mm});
            skLineSegment(sketch, "E829.0.15", {"start": v(74, 82.27) * mm, "end": v(74, 73.77) * mm});
            skLineSegment(sketch, "E829.0.16", {"start": v(74, 73.77) * mm, "end": v(74, 72.27) * mm});
            skLineSegment(sketch, "E829.0.17", {"start": v(74, 72.27) * mm, "end": v(74, 71.97) * mm});
            skArc(sketch, "E829.0.18", {"start": v(74, 71.97) * mm, "mid": v(73.92, 71.8) * mm, "end": v(73.74, 71.72) * mm});
            skLineSegment(sketch, "E829.0.19", {"start": v(73.74, 71.72) * mm, "end": v(73.24, 71.72) * mm});
            skArc(sketch, "E829.0.20", {"start": v(73.24, 71.72) * mm, "mid": v(73.07, 71.8) * mm, "end": v(73, 71.97) * mm});
            skLineSegment(sketch, "E829.0.21", {"start": v(73, 71.97) * mm, "end": v(73, 72.27) * mm});
            skArc(sketch, "E829.0.22", {"start": v(73, 72.27) * mm, "mid": v(72.92, 72.45) * mm, "end": v(72.74, 72.52) * mm});
            skLineSegment(sketch, "E829.0.23", {"start": v(72.74, 72.52) * mm, "end": v(43.13, 72.52) * mm});
            skLineSegment(sketch, "E829.0.24", {"start": v(43.13, 72.52) * mm, "end": v(-16.87, 72.52) * mm});
            skArc(sketch, "E829.0.25", {"start": v(-16.87, 72.52) * mm, "mid": v(-18.46, 71.86) * mm, "end": v(-19.12, 70.27) * mm});
            skLineSegment(sketch, "E829.0.26", {"start": v(-19.12, 70.27) * mm, "end": v(-19.12, 14.27) * mm});
            skArc(sketch, "E829.0.27", {"start": v(-19.12, 14.27) * mm, "mid": v(-18.46, 12.68) * mm, "end": v(-16.87, 12.02) * mm});
            skLineSegment(sketch, "E829.0.28", {"start": v(-16.87, 12.02) * mm, "end": v(43.13, 12.02) * mm});
            skLineSegment(sketch, "E829.0.29", {"start": v(43.13, 12.02) * mm, "end": v(72.74, 12.02) * mm});
            skArc(sketch, "E829.0.30", {"start": v(72.74, 12.02) * mm, "mid": v(72.92, 12.1) * mm, "end": v(73, 12.27) * mm});
            skLineSegment(sketch, "E829.0.31", {"start": v(73, 12.27) * mm, "end": v(73, 12.57) * mm});
            skArc(sketch, "E829.0.32", {"start": v(73, 12.57) * mm, "mid": v(73.07, 12.75) * mm, "end": v(73.24, 12.82) * mm});
            skLineSegment(sketch, "E829.0.33", {"start": v(73.24, 12.82) * mm, "end": v(73.74, 12.82) * mm});
            skArc(sketch, "E829.0.34", {"start": v(73.74, 12.82) * mm, "mid": v(73.92, 12.75) * mm, "end": v(74, 12.57) * mm});
            skLineSegment(sketch, "E829.0.35", {"start": v(74, 12.57) * mm, "end": v(74, 12.27) * mm});
            skLineSegment(sketch, "E829.0.36", {"start": v(74, 12.27) * mm, "end": v(74, 10.77) * mm});
            skLineSegment(sketch, "E829.0.37", {"start": v(74, 10.77) * mm, "end": v(74, 2.27) * mm});
            skArc(sketch, "E829.0.38", {"start": v(74, 2.27) * mm, "mid": v(74.07, 2.1) * mm, "end": v(74.24, 2.02) * mm});
            skLineSegment(sketch, "E829.0.39", {"start": v(74.24, 2.02) * mm, "end": v(89.13, 2.02) * mm});
            skLineSegment(sketch, "E830.0.0", {"start": v(48.77, 45.74) * mm, "end": v(48.76, 45.78) * mm});
            skArc(sketch, "E830.0.1", {"start": v(48.76, 45.78) * mm, "mid": v(48.75, 45.83) * mm, "end": v(48.74, 45.88) * mm});
            skLineSegment(sketch, "E830.0.2", {"start": v(48.74, 45.88) * mm, "end": v(48.73, 45.9) * mm});
            skLineSegment(sketch, "E830.0.3", {"start": v(48.73, 45.9) * mm, "end": v(48.68, 46.15) * mm});
            skLineSegment(sketch, "E830.0.4", {"start": v(48.68, 46.15) * mm, "end": v(48.61, 46.39) * mm});
            skArc(sketch, "E830.0.5", {"start": v(48.61, 46.39) * mm, "mid": v(47.84, 48.69) * mm, "end": v(46.77, 50.86) * mm});
            skArc(sketch, "E830.0.6", {"start": v(46.77, 50.86) * mm, "mid": v(44.66, 53.82) * mm, "end": v(42.02, 56.32) * mm});
            skArc(sketch, "E830.0.7", {"start": v(42.02, 56.32) * mm, "mid": v(40.53, 57.36) * mm, "end": v(38.95, 58.25) * mm});
            skArc(sketch, "E830.0.8", {"start": v(38.95, 58.25) * mm, "mid": v(37.28, 58.98) * mm, "end": v(35.55, 59.54) * mm});
            skArc(sketch, "E830.0.9", {"start": v(35.55, 59.54) * mm, "mid": v(35, 59.67) * mm, "end": v(34.46, 59.77) * mm});
            skArc(sketch, "E830.0.10", {"start": v(34.46, 59.77) * mm, "mid": v(34.22, 59.81) * mm, "end": v(33.98, 59.84) * mm});
            skArc(sketch, "E830.0.11", {"start": v(33.98, 59.84) * mm, "mid": v(33.52, 59.9) * mm, "end": v(33.07, 59.94) * mm});
            skArc(sketch, "E830.0.12", {"start": v(33.07, 59.94) * mm, "mid": v(32.5, 59.98) * mm, "end": v(31.93, 60) * mm});
            skLineSegment(sketch, "E830.0.13", {"start": v(31.93, 60) * mm, "end": v(31.93, 54.06) * mm});
            skLineSegment(sketch, "E830.0.14", {"start": v(31.93, 54.06) * mm, "end": v(33.99, 52) * mm});
            skLineSegment(sketch, "E830.0.15", {"start": v(33.99, 52) * mm, "end": v(36.84, 49.14) * mm});
            skLineSegment(sketch, "E830.0.16", {"start": v(36.84, 49.14) * mm, "end": v(35, 47.3) * mm});
            skLineSegment(sketch, "E830.0.17", {"start": v(35, 47.3) * mm, "end": v(33.15, 45.45) * mm});
            skLineSegment(sketch, "E830.0.18", {"start": v(33.15, 45.45) * mm, "end": v(32.51, 46.07) * mm});
            skLineSegment(sketch, "E830.0.19", {"start": v(32.51, 46.07) * mm, "end": v(31.87, 46.68) * mm});
            skLineSegment(sketch, "E830.0.20", {"start": v(31.87, 46.68) * mm, "end": v(31.34, 46.18) * mm});
            skArc(sketch, "E830.0.21", {"start": v(31.34, 46.18) * mm, "mid": v(31.22, 46.06) * mm, "end": v(31.1, 45.93) * mm});
            skArc(sketch, "E830.0.22", {"start": v(31.1, 45.93) * mm, "mid": v(30.99, 45.79) * mm, "end": v(30.9, 45.64) * mm});
            skLineSegment(sketch, "E830.0.23", {"start": v(30.9, 45.64) * mm, "end": v(30.87, 45.6) * mm});
            skArc(sketch, "E830.0.24", {"start": v(30.87, 45.6) * mm, "mid": v(30.84, 45.56) * mm, "end": v(30.82, 45.5) * mm});
            skLineSegment(sketch, "E830.0.25", {"start": v(30.82, 45.5) * mm, "end": v(30.85, 45.35) * mm});
            skArc(sketch, "E830.0.26", {"start": v(30.85, 45.35) * mm, "mid": v(30.88, 45.3) * mm, "end": v(30.91, 45.26) * mm});
            skArc(sketch, "E830.0.27", {"start": v(30.91, 45.26) * mm, "mid": v(30.98, 45.18) * mm, "end": v(31.04, 45.1) * mm});
            skArc(sketch, "E830.0.28", {"start": v(31.04, 45.1) * mm, "mid": v(31.08, 45.05) * mm, "end": v(31.12, 45) * mm});
            skLineSegment(sketch, "E830.0.29", {"start": v(31.12, 45) * mm, "end": v(31.13, 45) * mm});
            skLineSegment(sketch, "E830.0.30", {"start": v(31.13, 45) * mm, "end": v(31.19, 44.93) * mm});
            skLineSegment(sketch, "E830.0.31", {"start": v(31.19, 44.93) * mm, "end": v(31.33, 44.77) * mm});
            skLineSegment(sketch, "E830.0.32", {"start": v(31.33, 44.77) * mm, "end": v(31.52, 44.56) * mm});
            skLineSegment(sketch, "E830.0.33", {"start": v(31.52, 44.56) * mm, "end": v(31.78, 44.28) * mm});
            skLineSegment(sketch, "E830.0.34", {"start": v(31.78, 44.28) * mm, "end": v(31.93, 44.12) * mm});
            skLineSegment(sketch, "E830.0.35", {"start": v(31.93, 44.12) * mm, "end": v(32.1, 43.95) * mm});
            skLineSegment(sketch, "E830.0.36", {"start": v(32.1, 43.95) * mm, "end": v(32.3, 43.74) * mm});
            skArc(sketch, "E830.0.37", {"start": v(32.3, 43.74) * mm, "mid": v(32.41, 43.63) * mm, "end": v(32.53, 43.51) * mm});
            skLineSegment(sketch, "E830.0.38", {"start": v(32.53, 43.51) * mm, "end": v(32.65, 43.4) * mm});
            skLineSegment(sketch, "E830.0.39", {"start": v(32.65, 43.4) * mm, "end": v(32.78, 43.26) * mm});
            skArc(sketch, "E830.0.40", {"start": v(32.78, 43.26) * mm, "mid": v(33.13, 42.92) * mm, "end": v(33.49, 42.58) * mm});
            skLineSegment(sketch, "E830.0.41", {"start": v(33.49, 42.58) * mm, "end": v(33.68, 42.4) * mm});
            skLineSegment(sketch, "E830.0.42", {"start": v(33.68, 42.4) * mm, "end": v(33.89, 42.22) * mm});
            skLineSegment(sketch, "E830.0.43", {"start": v(33.89, 42.22) * mm, "end": v(33.94, 42.17) * mm});
            skLineSegment(sketch, "E830.0.44", {"start": v(33.94, 42.17) * mm, "end": v(34, 42.13) * mm});
            skLineSegment(sketch, "E830.0.45", {"start": v(34, 42.13) * mm, "end": v(34.1, 42.03) * mm});
            skLineSegment(sketch, "E830.0.46", {"start": v(34.1, 42.03) * mm, "end": v(34.13, 42) * mm});
            skArc(sketch, "E830.0.47", {"start": v(34.13, 42) * mm, "mid": v(34.24, 41.92) * mm, "end": v(34.36, 41.83) * mm});
            skArc(sketch, "E830.0.48", {"start": v(34.36, 41.83) * mm, "mid": v(34.42, 41.78) * mm, "end": v(34.5, 41.74) * mm});
            skLineSegment(sketch, "E830.0.49", {"start": v(34.5, 41.74) * mm, "end": v(34.54, 41.73) * mm});
            skArc(sketch, "E830.0.50", {"start": v(34.54, 41.73) * mm, "mid": v(34.57, 41.74) * mm, "end": v(34.6, 41.75) * mm});
            skArc(sketch, "E830.0.51", {"start": v(34.6, 41.75) * mm, "mid": v(34.64, 41.77) * mm, "end": v(34.68, 41.78) * mm});
            skLineSegment(sketch, "E830.0.52", {"start": v(34.68, 41.78) * mm, "end": v(34.7, 41.8) * mm});
            skLineSegment(sketch, "E830.0.53", {"start": v(34.7, 41.8) * mm, "end": v(34.74, 41.82) * mm});
            skArc(sketch, "E830.0.54", {"start": v(34.74, 41.82) * mm, "mid": v(34.84, 41.89) * mm, "end": v(34.93, 41.96) * mm});
            skArc(sketch, "E830.0.55", {"start": v(34.93, 41.96) * mm, "mid": v(35.1, 42.1) * mm, "end": v(35.26, 42.26) * mm});
            skLineSegment(sketch, "E830.0.56", {"start": v(35.26, 42.26) * mm, "end": v(35.76, 42.8) * mm});
            skLineSegment(sketch, "E830.0.57", {"start": v(35.76, 42.8) * mm, "end": v(35.14, 43.43) * mm});
            skLineSegment(sketch, "E830.0.58", {"start": v(35.14, 43.43) * mm, "end": v(34.53, 44.07) * mm});
            skLineSegment(sketch, "E830.0.59", {"start": v(34.53, 44.07) * mm, "end": v(36.37, 45.92) * mm});
            skLineSegment(sketch, "E830.0.60", {"start": v(36.37, 45.92) * mm, "end": v(38.22, 47.76) * mm});
            skLineSegment(sketch, "E830.0.61", {"start": v(38.22, 47.76) * mm, "end": v(41.08, 44.9) * mm});
            skLineSegment(sketch, "E830.0.62", {"start": v(41.08, 44.9) * mm, "end": v(43.3, 42.68) * mm});
            skLineSegment(sketch, "E830.0.63", {"start": v(43.3, 42.68) * mm, "end": v(49.1, 42.68) * mm});
            skArc(sketch, "E830.0.64", {"start": v(49.1, 42.68) * mm, "mid": v(49.08, 43.2) * mm, "end": v(49.05, 43.73) * mm});
            skArc(sketch, "E830.0.65", {"start": v(49.05, 43.73) * mm, "mid": v(49.03, 43.9) * mm, "end": v(49.02, 44.06) * mm});
            skArc(sketch, "E830.0.66", {"start": v(49.02, 44.06) * mm, "mid": v(48.95, 44.65) * mm, "end": v(48.86, 45.23) * mm});
            skArc(sketch, "E830.0.67", {"start": v(48.86, 45.23) * mm, "mid": v(48.84, 45.38) * mm, "end": v(48.8, 45.52) * mm});
            skLineSegment(sketch, "E830.0.68", {"start": v(48.8, 45.52) * mm, "end": v(48.77, 45.74) * mm});
            skLineSegment(sketch, "E831.0.0", {"start": v(30.97, 37.99) * mm, "end": v(31.55, 38.56) * mm});
            skLineSegment(sketch, "E831.0.1", {"start": v(31.55, 38.56) * mm, "end": v(29.6, 40.51) * mm});
            skLineSegment(sketch, "E831.0.2", {"start": v(29.6, 40.51) * mm, "end": v(27.64, 42.47) * mm});
            skLineSegment(sketch, "E831.0.3", {"start": v(27.64, 42.47) * mm, "end": v(27.07, 41.9) * mm});
            skLineSegment(sketch, "E831.0.4", {"start": v(27.07, 41.9) * mm, "end": v(26.5, 41.32) * mm});
            skLineSegment(sketch, "E831.0.5", {"start": v(26.5, 41.32) * mm, "end": v(27.1, 40.67) * mm});
            skLineSegment(sketch, "E831.0.6", {"start": v(27.1, 40.67) * mm, "end": v(27.73, 40.03) * mm});
            skLineSegment(sketch, "E831.0.7", {"start": v(27.73, 40.03) * mm, "end": v(25.88, 38.18) * mm});
            skLineSegment(sketch, "E831.0.8", {"start": v(25.88, 38.18) * mm, "end": v(24.04, 36.34) * mm});
            skLineSegment(sketch, "E831.0.9", {"start": v(24.04, 36.34) * mm, "end": v(21.18, 39.2) * mm});
            skLineSegment(sketch, "E831.0.10", {"start": v(21.18, 39.2) * mm, "end": v(19.06, 41.32) * mm});
            skLineSegment(sketch, "E831.0.11", {"start": v(19.06, 41.32) * mm, "end": v(13.1, 41.32) * mm});
            skArc(sketch, "E831.0.12", {"start": v(13.1, 41.32) * mm, "mid": v(13.1, 41.22) * mm, "end": v(13.11, 41.12) * mm});
            skLineSegment(sketch, "E831.0.13", {"start": v(13.11, 41.12) * mm, "end": v(13.13, 40.97) * mm});
            skLineSegment(sketch, "E831.0.14", {"start": v(13.13, 40.97) * mm, "end": v(13.14, 40.83) * mm});
            skLineSegment(sketch, "E831.0.15", {"start": v(13.14, 40.83) * mm, "end": v(13.16, 40.6) * mm});
            skLineSegment(sketch, "E831.0.16", {"start": v(13.16, 40.6) * mm, "end": v(13.18, 40.42) * mm});
            skLineSegment(sketch, "E831.0.17", {"start": v(13.18, 40.42) * mm, "end": v(13.21, 40.16) * mm});
            skLineSegment(sketch, "E831.0.18", {"start": v(13.21, 40.16) * mm, "end": v(13.25, 39.9) * mm});
            skArc(sketch, "E831.0.19", {"start": v(13.25, 39.9) * mm, "mid": v(13.55, 38.18) * mm, "end": v(14.02, 36.5) * mm});
            skArc(sketch, "E831.0.20", {"start": v(14.02, 36.5) * mm, "mid": v(14.57, 35.06) * mm, "end": v(15.24, 33.68) * mm});
            skArc(sketch, "E831.0.21", {"start": v(15.24, 33.68) * mm, "mid": v(16.68, 31.42) * mm, "end": v(18.43, 29.4) * mm});
            skArc(sketch, "E831.0.22", {"start": v(18.43, 29.4) * mm, "mid": v(19.93, 28.05) * mm, "end": v(21.56, 26.87) * mm});
            skArc(sketch, "E831.0.23", {"start": v(21.56, 26.87) * mm, "mid": v(22.86, 26.1) * mm, "end": v(24.22, 25.45) * mm});
            skArc(sketch, "E831.0.24", {"start": v(24.22, 25.45) * mm, "mid": v(25.27, 25.04) * mm, "end": v(26.35, 24.7) * mm});
            skArc(sketch, "E831.0.25", {"start": v(26.35, 24.7) * mm, "mid": v(28, 24.3) * mm, "end": v(29.7, 24.08) * mm});
            skArc(sketch, "E831.0.26", {"start": v(29.7, 24.08) * mm, "mid": v(30, 24.06) * mm, "end": v(30.32, 24.05) * mm});
            skLineSegment(sketch, "E831.0.27", {"start": v(30.32, 24.05) * mm, "end": v(30.32, 30.05) * mm});
            skLineSegment(sketch, "E831.0.28", {"start": v(30.32, 30.05) * mm, "end": v(28.27, 32.1) * mm});
            skLineSegment(sketch, "E831.0.29", {"start": v(28.27, 32.1) * mm, "end": v(25.42, 34.96) * mm});
            skLineSegment(sketch, "E831.0.30", {"start": v(25.42, 34.96) * mm, "end": v(27.26, 36.8) * mm});
            skLineSegment(sketch, "E831.0.31", {"start": v(27.26, 36.8) * mm, "end": v(29.1, 38.65) * mm});
            skLineSegment(sketch, "E831.0.32", {"start": v(29.1, 38.65) * mm, "end": v(29.75, 38.03) * mm});
            skLineSegment(sketch, "E831.0.33", {"start": v(29.75, 38.03) * mm, "end": v(30.4, 37.41) * mm});
            skLineSegment(sketch, "E831.0.34", {"start": v(30.4, 37.41) * mm, "end": v(30.97, 37.99) * mm});
            skLineSegment(sketch, "E832.0.0", {"start": v(41.63, 39.75) * mm, "end": v(41.56, 39.69) * mm});
            skLineSegment(sketch, "E832.0.1", {"start": v(41.56, 39.69) * mm, "end": v(41.38, 39.52) * mm});
            skLineSegment(sketch, "E832.0.2", {"start": v(41.38, 39.52) * mm, "end": v(41.14, 39.3) * mm});
            skLineSegment(sketch, "E832.0.3", {"start": v(41.14, 39.3) * mm, "end": v(41, 39.17) * mm});
            skLineSegment(sketch, "E832.0.4", {"start": v(41, 39.17) * mm, "end": v(40.97, 39.13) * mm});
            skArc(sketch, "E832.0.5", {"start": v(40.97, 39.13) * mm, "mid": v(40.77, 38.97) * mm, "end": v(40.57, 38.8) * mm});
            skArc(sketch, "E832.0.6", {"start": v(40.57, 38.8) * mm, "mid": v(40.56, 38.8) * mm, "end": v(40.55, 38.79) * mm});
            skLineSegment(sketch, "E832.0.7", {"start": v(40.55, 38.79) * mm, "end": v(40.52, 38.76) * mm});
            skLineSegment(sketch, "E832.0.8", {"start": v(40.52, 38.76) * mm, "end": v(40.46, 38.72) * mm});
            skArc(sketch, "E832.0.9", {"start": v(40.46, 38.72) * mm, "mid": v(40.4, 38.68) * mm, "end": v(40.34, 38.64) * mm});
            skLineSegment(sketch, "E832.0.10", {"start": v(40.34, 38.64) * mm, "end": v(40.27, 38.6) * mm});
            skLineSegment(sketch, "E832.0.11", {"start": v(40.27, 38.6) * mm, "end": v(40.24, 38.58) * mm});
            skArc(sketch, "E832.0.12", {"start": v(40.24, 38.58) * mm, "mid": v(40.2, 38.57) * mm, "end": v(40.16, 38.55) * mm});
            skArc(sketch, "E832.0.13", {"start": v(40.16, 38.55) * mm, "mid": v(40.12, 38.54) * mm, "end": v(40.08, 38.54) * mm});
            skLineSegment(sketch, "E832.0.14", {"start": v(40.08, 38.54) * mm, "end": v(40.04, 38.56) * mm});
            skArc(sketch, "E832.0.15", {"start": v(40.04, 38.56) * mm, "mid": v(39.95, 38.64) * mm, "end": v(39.85, 38.7) * mm});
            skArc(sketch, "E832.0.16", {"start": v(39.85, 38.7) * mm, "mid": v(39.73, 38.73) * mm, "end": v(39.61, 38.73) * mm});
            skArc(sketch, "E832.0.17", {"start": v(39.61, 38.73) * mm, "mid": v(39.54, 38.72) * mm, "end": v(39.46, 38.7) * mm});
            skArc(sketch, "E832.0.18", {"start": v(39.46, 38.7) * mm, "mid": v(39.36, 38.66) * mm, "end": v(39.27, 38.6) * mm});
            skArc(sketch, "E832.0.19", {"start": v(39.27, 38.6) * mm, "mid": v(39.16, 38.54) * mm, "end": v(39.04, 38.47) * mm});
            skArc(sketch, "E832.0.20", {"start": v(39.04, 38.47) * mm, "mid": v(38.9, 38.36) * mm, "end": v(38.76, 38.25) * mm});
            skLineSegment(sketch, "E832.0.21", {"start": v(38.76, 38.25) * mm, "end": v(38.61, 38.13) * mm});
            skLineSegment(sketch, "E832.0.22", {"start": v(38.61, 38.13) * mm, "end": v(38.44, 37.98) * mm});
            skLineSegment(sketch, "E832.0.23", {"start": v(38.44, 37.98) * mm, "end": v(38.26, 37.81) * mm});
            skLineSegment(sketch, "E832.0.24", {"start": v(38.26, 37.81) * mm, "end": v(38.05, 37.62) * mm});
            skArc(sketch, "E832.0.25", {"start": v(38.05, 37.62) * mm, "mid": v(37.78, 37.36) * mm, "end": v(37.5, 37.1) * mm});
            skLineSegment(sketch, "E832.0.26", {"start": v(37.5, 37.1) * mm, "end": v(37.44, 37.03) * mm});
            skLineSegment(sketch, "E832.0.27", {"start": v(37.44, 37.03) * mm, "end": v(37.37, 36.96) * mm});
            skLineSegment(sketch, "E832.0.28", {"start": v(37.37, 36.96) * mm, "end": v(37.3, 36.89) * mm});
            skLineSegment(sketch, "E832.0.29", {"start": v(37.3, 36.89) * mm, "end": v(37.22, 36.81) * mm});
            skLineSegment(sketch, "E832.0.30", {"start": v(37.22, 36.81) * mm, "end": v(36.88, 36.47) * mm});
            skLineSegment(sketch, "E832.0.31", {"start": v(36.88, 36.47) * mm, "end": v(36.79, 36.39) * mm});
            skLineSegment(sketch, "E832.0.32", {"start": v(36.79, 36.39) * mm, "end": v(36.37, 35.96) * mm});
            skLineSegment(sketch, "E832.0.33", {"start": v(36.37, 35.96) * mm, "end": v(36.23, 35.82) * mm});
            skLineSegment(sketch, "E832.0.34", {"start": v(36.23, 35.82) * mm, "end": v(36.04, 35.63) * mm});
            skLineSegment(sketch, "E832.0.35", {"start": v(36.04, 35.63) * mm, "end": v(35.8, 35.37) * mm});
            skLineSegment(sketch, "E832.0.36", {"start": v(35.8, 35.37) * mm, "end": v(35.73, 35.3) * mm});
            skArc(sketch, "E832.0.37", {"start": v(35.73, 35.3) * mm, "mid": v(35.55, 35.12) * mm, "end": v(35.38, 34.93) * mm});
            skArc(sketch, "E832.0.38", {"start": v(35.38, 34.93) * mm, "mid": v(35.16, 34.68) * mm, "end": v(34.94, 34.42) * mm});
            skArc(sketch, "E832.0.39", {"start": v(34.94, 34.42) * mm, "mid": v(34.82, 34.27) * mm, "end": v(34.7, 34.12) * mm});
            skArc(sketch, "E832.0.40", {"start": v(34.7, 34.12) * mm, "mid": v(34.65, 34.03) * mm, "end": v(34.6, 33.94) * mm});
            skArc(sketch, "E832.0.41", {"start": v(34.6, 33.94) * mm, "mid": v(34.54, 33.85) * mm, "end": v(34.5, 33.75) * mm});
            skArc(sketch, "E832.0.42", {"start": v(34.5, 33.75) * mm, "mid": v(34.46, 33.63) * mm, "end": v(34.45, 33.51) * mm});
            skArc(sketch, "E832.0.43", {"start": v(34.45, 33.51) * mm, "mid": v(34.46, 33.38) * mm, "end": v(34.52, 33.26) * mm});
            skArc(sketch, "E832.0.44", {"start": v(34.52, 33.26) * mm, "mid": v(34.57, 33.2) * mm, "end": v(34.62, 33.14) * mm});
            skLineSegment(sketch, "E832.0.45", {"start": v(34.62, 33.14) * mm, "end": v(34.64, 33.05) * mm});
            skArc(sketch, "E832.0.46", {"start": v(34.64, 33.05) * mm, "mid": v(34.62, 33) * mm, "end": v(34.6, 32.97) * mm});
            skArc(sketch, "E832.0.47", {"start": v(34.6, 32.97) * mm, "mid": v(34.57, 32.89) * mm, "end": v(34.52, 32.81) * mm});
            skArc(sketch, "E832.0.48", {"start": v(34.52, 32.81) * mm, "mid": v(34.42, 32.67) * mm, "end": v(34.32, 32.53) * mm});
            skArc(sketch, "E832.0.49", {"start": v(34.32, 32.53) * mm, "mid": v(34.1, 32.27) * mm, "end": v(33.87, 32.02) * mm});
            skArc(sketch, "E832.0.50", {"start": v(33.87, 32.02) * mm, "mid": v(33.8, 31.95) * mm, "end": v(33.74, 31.87) * mm});
            skLineSegment(sketch, "E832.0.51", {"start": v(33.74, 31.87) * mm, "end": v(33.59, 31.71) * mm});
            skLineSegment(sketch, "E832.0.52", {"start": v(33.59, 31.71) * mm, "end": v(33.41, 31.53) * mm});
            skLineSegment(sketch, "E832.0.53", {"start": v(33.41, 31.53) * mm, "end": v(33.2, 31.32) * mm});
            skArc(sketch, "E832.0.54", {"start": v(33.2, 31.32) * mm, "mid": v(33.1, 31.2) * mm, "end": v(32.97, 31.09) * mm});
            skLineSegment(sketch, "E832.0.55", {"start": v(32.97, 31.09) * mm, "end": v(31.83, 29.95) * mm});
            skLineSegment(sketch, "E832.0.56", {"start": v(31.83, 29.95) * mm, "end": v(31.83, 24.05) * mm});
            skArc(sketch, "E832.0.57", {"start": v(31.83, 24.05) * mm, "mid": v(32.46, 24.1) * mm, "end": v(33.09, 24.16) * mm});
            skArc(sketch, "E832.0.58", {"start": v(33.09, 24.16) * mm, "mid": v(33.9, 24.28) * mm, "end": v(34.7, 24.43) * mm});
            skLineSegment(sketch, "E832.0.59", {"start": v(34.7, 24.43) * mm, "end": v(34.75, 24.44) * mm});
            skLineSegment(sketch, "E832.0.60", {"start": v(34.75, 24.44) * mm, "end": v(34.85, 24.46) * mm});
            skArc(sketch, "E832.0.61", {"start": v(34.85, 24.46) * mm, "mid": v(34.9, 24.47) * mm, "end": v(34.95, 24.48) * mm});
            skArc(sketch, "E832.0.62", {"start": v(34.95, 24.48) * mm, "mid": v(35, 24.49) * mm, "end": v(35.06, 24.5) * mm});
            skLineSegment(sketch, "E832.0.63", {"start": v(35.06, 24.5) * mm, "end": v(35.13, 24.51) * mm});
            skLineSegment(sketch, "E832.0.64", {"start": v(35.13, 24.51) * mm, "end": v(35.45, 24.58) * mm});
            skLineSegment(sketch, "E832.0.65", {"start": v(35.45, 24.58) * mm, "end": v(35.49, 24.6) * mm});
            skArc(sketch, "E832.0.66", {"start": v(35.49, 24.6) * mm, "mid": v(35.56, 24.6) * mm, "end": v(35.62, 24.63) * mm});
            skLineSegment(sketch, "E832.0.67", {"start": v(35.62, 24.63) * mm, "end": v(35.68, 24.64) * mm});
            skLineSegment(sketch, "E832.0.68", {"start": v(35.68, 24.64) * mm, "end": v(35.86, 24.68) * mm});
            skArc(sketch, "E832.0.69", {"start": v(35.86, 24.68) * mm, "mid": v(36.12, 24.75) * mm, "end": v(36.39, 24.83) * mm});
            skArc(sketch, "E832.0.70", {"start": v(36.39, 24.83) * mm, "mid": v(40.57, 26.79) * mm, "end": v(44.14, 29.72) * mm});
            skArc(sketch, "E832.0.71", {"start": v(44.14, 29.72) * mm, "mid": v(45.63, 31.49) * mm, "end": v(46.88, 33.43) * mm});
            skArc(sketch, "E832.0.72", {"start": v(46.88, 33.43) * mm, "mid": v(47.88, 35.52) * mm, "end": v(48.61, 37.71) * mm});
            skArc(sketch, "E832.0.73", {"start": v(48.61, 37.71) * mm, "mid": v(48.65, 37.85) * mm, "end": v(48.68, 37.98) * mm});
            skArc(sketch, "E832.0.74", {"start": v(48.68, 37.98) * mm, "mid": v(48.8, 38.5) * mm, "end": v(48.89, 39.02) * mm});
            skArc(sketch, "E832.0.75", {"start": v(48.89, 39.02) * mm, "mid": v(48.9, 39.13) * mm, "end": v(48.92, 39.25) * mm});
            skArc(sketch, "E832.0.76", {"start": v(48.92, 39.25) * mm, "mid": v(49.03, 40.14) * mm, "end": v(49.09, 41.04) * mm});
            skArc(sketch, "E832.0.77", {"start": v(49.09, 41.04) * mm, "mid": v(49.1, 41.1) * mm, "end": v(49.1, 41.18) * mm});
            skLineSegment(sketch, "E832.0.78", {"start": v(49.1, 41.18) * mm, "end": v(43.06, 41.18) * mm});
            skLineSegment(sketch, "E832.0.79", {"start": v(43.06, 41.18) * mm, "end": v(42.09, 40.2) * mm});
            skLineSegment(sketch, "E832.0.80", {"start": v(42.09, 40.2) * mm, "end": v(41.89, 40) * mm});
            skLineSegment(sketch, "E832.0.81", {"start": v(41.89, 40) * mm, "end": v(41.69, 39.8) * mm});
            skLineSegment(sketch, "E832.0.82", {"start": v(41.69, 39.8) * mm, "end": v(41.63, 39.75) * mm});
            skLineSegment(sketch, "E833.0.0", {"start": v(46.12, 63.52) * mm, "end": v(46.44, 63.52) * mm});
            skLineSegment(sketch, "E833.0.1", {"start": v(46.44, 63.52) * mm, "end": v(53.57, 63.52) * mm});
            skLineSegment(sketch, "E833.0.2", {"start": v(53.57, 63.52) * mm, "end": v(60.7, 63.52) * mm});
            skLineSegment(sketch, "E833.0.3", {"start": v(60.7, 63.52) * mm, "end": v(61.02, 63.52) * mm});
            skLineSegment(sketch, "E833.0.4", {"start": v(61.02, 63.52) * mm, "end": v(61.02, 64.43) * mm});
            skArc(sketch, "E833.0.5", {"start": v(61.02, 64.43) * mm, "mid": v(60.87, 64.51) * mm, "end": v(60.82, 64.67) * mm});
            skLineSegment(sketch, "E833.0.6", {"start": v(60.82, 64.67) * mm, "end": v(60.82, 64.87) * mm});
            skArc(sketch, "E833.0.7", {"start": v(60.82, 64.87) * mm, "mid": v(60.87, 65.03) * mm, "end": v(61.02, 65.12) * mm});
            skLineSegment(sketch, "E833.0.8", {"start": v(61.02, 65.12) * mm, "end": v(61.02, 66.02) * mm});
            skLineSegment(sketch, "E833.0.9", {"start": v(61.02, 66.02) * mm, "end": v(60.7, 66.02) * mm});
            skLineSegment(sketch, "E833.0.10", {"start": v(60.7, 66.02) * mm, "end": v(53.57, 66.02) * mm});
            skLineSegment(sketch, "E833.0.11", {"start": v(53.57, 66.02) * mm, "end": v(46.44, 66.02) * mm});
            skLineSegment(sketch, "E833.0.12", {"start": v(46.44, 66.02) * mm, "end": v(46.12, 66.02) * mm});
            skLineSegment(sketch, "E833.0.13", {"start": v(46.12, 66.02) * mm, "end": v(46.12, 65.12) * mm});
            skArc(sketch, "E833.0.14", {"start": v(46.12, 65.12) * mm, "mid": v(46.26, 65.03) * mm, "end": v(46.32, 64.87) * mm});
            skLineSegment(sketch, "E833.0.15", {"start": v(46.32, 64.87) * mm, "end": v(46.32, 64.67) * mm});
            skArc(sketch, "E833.0.16", {"start": v(46.32, 64.67) * mm, "mid": v(46.26, 64.51) * mm, "end": v(46.12, 64.43) * mm});
            skLineSegment(sketch, "E833.0.17", {"start": v(46.12, 64.43) * mm, "end": v(46.12, 63.52) * mm});
            skLineSegment(sketch, "E834.0.0", {"start": v(46.12, 18.52) * mm, "end": v(46.44, 18.52) * mm});
            skLineSegment(sketch, "E834.0.1", {"start": v(46.44, 18.52) * mm, "end": v(53.57, 18.52) * mm});
            skLineSegment(sketch, "E834.0.2", {"start": v(53.57, 18.52) * mm, "end": v(60.7, 18.52) * mm});
            skLineSegment(sketch, "E834.0.3", {"start": v(60.7, 18.52) * mm, "end": v(61.02, 18.52) * mm});
            skLineSegment(sketch, "E834.0.4", {"start": v(61.02, 18.52) * mm, "end": v(61.02, 19.43) * mm});
            skArc(sketch, "E834.0.5", {"start": v(61.02, 19.43) * mm, "mid": v(60.87, 19.51) * mm, "end": v(60.82, 19.67) * mm});
            skLineSegment(sketch, "E834.0.6", {"start": v(60.82, 19.67) * mm, "end": v(60.82, 19.87) * mm});
            skArc(sketch, "E834.0.7", {"start": v(60.82, 19.87) * mm, "mid": v(60.87, 20.03) * mm, "end": v(61.02, 20.12) * mm});
            skLineSegment(sketch, "E834.0.8", {"start": v(61.02, 20.12) * mm, "end": v(61.02, 21.02) * mm});
            skLineSegment(sketch, "E834.0.9", {"start": v(61.02, 21.02) * mm, "end": v(60.7, 21.02) * mm});
            skLineSegment(sketch, "E834.0.10", {"start": v(60.7, 21.02) * mm, "end": v(53.57, 21.02) * mm});
            skLineSegment(sketch, "E834.0.11", {"start": v(53.57, 21.02) * mm, "end": v(46.44, 21.02) * mm});
            skLineSegment(sketch, "E834.0.12", {"start": v(46.44, 21.02) * mm, "end": v(46.12, 21.02) * mm});
            skLineSegment(sketch, "E834.0.13", {"start": v(46.12, 21.02) * mm, "end": v(46.12, 20.12) * mm});
            skArc(sketch, "E834.0.14", {"start": v(46.12, 20.12) * mm, "mid": v(46.26, 20.03) * mm, "end": v(46.32, 19.87) * mm});
            skLineSegment(sketch, "E834.0.15", {"start": v(46.32, 19.87) * mm, "end": v(46.32, 19.67) * mm});
            skArc(sketch, "E834.0.16", {"start": v(46.32, 19.67) * mm, "mid": v(46.26, 19.51) * mm, "end": v(46.12, 19.43) * mm});
            skLineSegment(sketch, "E834.0.17", {"start": v(46.12, 19.43) * mm, "end": v(46.12, 18.52) * mm});
            skArc(sketch, "E835.0.0", {"start": v(30.43, 60) * mm, "mid": v(30.3, 60) * mm, "end": v(30.16, 60) * mm});
            skLineSegment(sketch, "E835.0.1", {"start": v(30.16, 60) * mm, "end": v(30.1, 60) * mm});
            skArc(sketch, "E835.0.2", {"start": v(30.1, 60) * mm, "mid": v(29.68, 59.98) * mm, "end": v(29.25, 59.95) * mm});
            skArc(sketch, "E835.0.3", {"start": v(29.25, 59.95) * mm, "mid": v(28.6, 59.88) * mm, "end": v(27.97, 59.8) * mm});
            skArc(sketch, "E835.0.4", {"start": v(27.97, 59.8) * mm, "mid": v(27.65, 59.75) * mm, "end": v(27.34, 59.69) * mm});
            skArc(sketch, "E835.0.5", {"start": v(27.34, 59.69) * mm, "mid": v(27.02, 59.62) * mm, "end": v(26.71, 59.54) * mm});
            skArc(sketch, "E835.0.6", {"start": v(26.71, 59.54) * mm, "mid": v(26.07, 59.36) * mm, "end": v(25.43, 59.15) * mm});
            skArc(sketch, "E835.0.7", {"start": v(25.43, 59.15) * mm, "mid": v(25.14, 59.04) * mm, "end": v(24.84, 58.93) * mm});
            skArc(sketch, "E835.0.8", {"start": v(24.84, 58.93) * mm, "mid": v(23.73, 58.45) * mm, "end": v(22.64, 57.9) * mm});
            skArc(sketch, "E835.0.9", {"start": v(22.64, 57.9) * mm, "mid": v(19.18, 55.42) * mm, "end": v(16.36, 52.25) * mm});
            skArc(sketch, "E835.0.10", {"start": v(16.36, 52.25) * mm, "mid": v(16.32, 52.2) * mm, "end": v(16.28, 52.14) * mm});
            skArc(sketch, "E835.0.11", {"start": v(16.28, 52.14) * mm, "mid": v(15.19, 50.35) * mm, "end": v(14.3, 48.45) * mm});
            skArc(sketch, "E835.0.12", {"start": v(14.3, 48.45) * mm, "mid": v(13.95, 47.46) * mm, "end": v(13.65, 46.45) * mm});
            skArc(sketch, "E835.0.13", {"start": v(13.65, 46.45) * mm, "mid": v(13.42, 45.43) * mm, "end": v(13.25, 44.4) * mm});
            skArc(sketch, "E835.0.14", {"start": v(13.25, 44.4) * mm, "mid": v(13.24, 44.32) * mm, "end": v(13.24, 44.25) * mm});
            skLineSegment(sketch, "E835.0.15", {"start": v(13.24, 44.25) * mm, "end": v(13.2, 43.98) * mm});
            skLineSegment(sketch, "E835.0.16", {"start": v(13.2, 43.98) * mm, "end": v(13.17, 43.73) * mm});
            skLineSegment(sketch, "E835.0.17", {"start": v(13.17, 43.73) * mm, "end": v(13.17, 43.73) * mm});
            skArc(sketch, "E835.0.18", {"start": v(13.17, 43.73) * mm, "mid": v(13.16, 43.6) * mm, "end": v(13.15, 43.49) * mm});
            skLineSegment(sketch, "E835.0.19", {"start": v(13.15, 43.49) * mm, "end": v(13.12, 43.27) * mm});
            skLineSegment(sketch, "E835.0.20", {"start": v(13.12, 43.27) * mm, "end": v(13.12, 43.21) * mm});
            skArc(sketch, "E835.0.21", {"start": v(13.12, 43.21) * mm, "mid": v(13.1, 43.02) * mm, "end": v(13.09, 42.82) * mm});
            skLineSegment(sketch, "E835.0.22", {"start": v(13.09, 42.82) * mm, "end": v(19.09, 42.82) * mm});
            skLineSegment(sketch, "E835.0.23", {"start": v(19.09, 42.82) * mm, "end": v(20.2, 43.93) * mm});
            skLineSegment(sketch, "E835.0.24", {"start": v(20.2, 43.93) * mm, "end": v(20.5, 44.22) * mm});
            skLineSegment(sketch, "E835.0.25", {"start": v(20.5, 44.22) * mm, "end": v(20.52, 44.24) * mm});
            skLineSegment(sketch, "E835.0.26", {"start": v(20.52, 44.24) * mm, "end": v(20.6, 44.32) * mm});
            skLineSegment(sketch, "E835.0.27", {"start": v(20.6, 44.32) * mm, "end": v(20.74, 44.45) * mm});
            skLineSegment(sketch, "E835.0.28", {"start": v(20.74, 44.45) * mm, "end": v(20.92, 44.62) * mm});
            skLineSegment(sketch, "E835.0.29", {"start": v(20.92, 44.62) * mm, "end": v(20.95, 44.65) * mm});
            skArc(sketch, "E835.0.30", {"start": v(20.95, 44.65) * mm, "mid": v(21.3, 44.97) * mm, "end": v(21.67, 45.28) * mm});
            skArc(sketch, "E835.0.31", {"start": v(21.67, 45.28) * mm, "mid": v(21.73, 45.32) * mm, "end": v(21.78, 45.36) * mm});
            skArc(sketch, "E835.0.32", {"start": v(21.78, 45.36) * mm, "mid": v(21.9, 45.45) * mm, "end": v(22.03, 45.53) * mm});
            skArc(sketch, "E835.0.33", {"start": v(22.03, 45.53) * mm, "mid": v(22.07, 45.55) * mm, "end": v(22.1, 45.56) * mm});
            skArc(sketch, "E835.0.34", {"start": v(22.1, 45.56) * mm, "mid": v(22.14, 45.58) * mm, "end": v(22.18, 45.58) * mm});
            skLineSegment(sketch, "E835.0.35", {"start": v(22.18, 45.58) * mm, "end": v(22.23, 45.57) * mm});
            skArc(sketch, "E835.0.36", {"start": v(22.23, 45.57) * mm, "mid": v(22.29, 45.48) * mm, "end": v(22.37, 45.4) * mm});
            skArc(sketch, "E835.0.37", {"start": v(22.37, 45.4) * mm, "mid": v(22.47, 45.36) * mm, "end": v(22.58, 45.36) * mm});
            skArc(sketch, "E835.0.38", {"start": v(22.58, 45.36) * mm, "mid": v(22.65, 45.37) * mm, "end": v(22.73, 45.38) * mm});
            skArc(sketch, "E835.0.39", {"start": v(22.73, 45.38) * mm, "mid": v(22.81, 45.42) * mm, "end": v(22.9, 45.46) * mm});
            skArc(sketch, "E835.0.40", {"start": v(22.9, 45.46) * mm, "mid": v(23, 45.51) * mm, "end": v(23.11, 45.58) * mm});
            skArc(sketch, "E835.0.41", {"start": v(23.11, 45.58) * mm, "mid": v(23.24, 45.67) * mm, "end": v(23.37, 45.76) * mm});
            skLineSegment(sketch, "E835.0.42", {"start": v(23.37, 45.76) * mm, "end": v(23.5, 45.87) * mm});
            skArc(sketch, "E835.0.43", {"start": v(23.5, 45.87) * mm, "mid": v(23.68, 46.02) * mm, "end": v(23.86, 46.17) * mm});
            skLineSegment(sketch, "E835.0.44", {"start": v(23.86, 46.17) * mm, "end": v(24.05, 46.34) * mm});
            skLineSegment(sketch, "E835.0.45", {"start": v(24.05, 46.34) * mm, "end": v(24.15, 46.43) * mm});
            skLineSegment(sketch, "E835.0.46", {"start": v(24.15, 46.43) * mm, "end": v(24.38, 46.64) * mm});
            skArc(sketch, "E835.0.47", {"start": v(24.38, 46.64) * mm, "mid": v(24.5, 46.77) * mm, "end": v(24.63, 46.89) * mm});
            skLineSegment(sketch, "E835.0.48", {"start": v(24.63, 46.89) * mm, "end": v(24.77, 47.02) * mm});
            skArc(sketch, "E835.0.49", {"start": v(24.77, 47.02) * mm, "mid": v(25.12, 47.37) * mm, "end": v(25.47, 47.72) * mm});
            skLineSegment(sketch, "E835.0.50", {"start": v(25.47, 47.72) * mm, "end": v(25.9, 48.14) * mm});
            skLineSegment(sketch, "E835.0.51", {"start": v(25.9, 48.14) * mm, "end": v(26.03, 48.28) * mm});
            skLineSegment(sketch, "E835.0.52", {"start": v(26.03, 48.28) * mm, "end": v(26.22, 48.48) * mm});
            skLineSegment(sketch, "E835.0.53", {"start": v(26.22, 48.48) * mm, "end": v(26.47, 48.73) * mm});
            skLineSegment(sketch, "E835.0.54", {"start": v(26.47, 48.73) * mm, "end": v(26.53, 48.8) * mm});
            skArc(sketch, "E835.0.55", {"start": v(26.53, 48.8) * mm, "mid": v(26.7, 48.98) * mm, "end": v(26.88, 49.17) * mm});
            skArc(sketch, "E835.0.56", {"start": v(26.88, 49.17) * mm, "mid": v(27.1, 49.42) * mm, "end": v(27.32, 49.68) * mm});
            skArc(sketch, "E835.0.57", {"start": v(27.32, 49.68) * mm, "mid": v(27.44, 49.83) * mm, "end": v(27.55, 49.98) * mm});
            skArc(sketch, "E835.0.58", {"start": v(27.55, 49.98) * mm, "mid": v(27.61, 50.07) * mm, "end": v(27.66, 50.16) * mm});
            skArc(sketch, "E835.0.59", {"start": v(27.66, 50.16) * mm, "mid": v(27.72, 50.25) * mm, "end": v(27.76, 50.35) * mm});
            skArc(sketch, "E835.0.60", {"start": v(27.76, 50.35) * mm, "mid": v(27.8, 50.47) * mm, "end": v(27.81, 50.59) * mm});
            skArc(sketch, "E835.0.61", {"start": v(27.81, 50.59) * mm, "mid": v(27.8, 50.72) * mm, "end": v(27.73, 50.85) * mm});
            skArc(sketch, "E835.0.62", {"start": v(27.73, 50.85) * mm, "mid": v(27.7, 50.9) * mm, "end": v(27.64, 50.96) * mm});
            skLineSegment(sketch, "E835.0.63", {"start": v(27.64, 50.96) * mm, "end": v(27.62, 51.05) * mm});
            skArc(sketch, "E835.0.64", {"start": v(27.62, 51.05) * mm, "mid": v(27.64, 51.1) * mm, "end": v(27.65, 51.14) * mm});
            skArc(sketch, "E835.0.65", {"start": v(27.65, 51.14) * mm, "mid": v(27.7, 51.21) * mm, "end": v(27.74, 51.29) * mm});
            skArc(sketch, "E835.0.66", {"start": v(27.74, 51.29) * mm, "mid": v(27.84, 51.43) * mm, "end": v(27.94, 51.57) * mm});
            skArc(sketch, "E835.0.67", {"start": v(27.94, 51.57) * mm, "mid": v(28.16, 51.83) * mm, "end": v(28.39, 52.08) * mm});
            skArc(sketch, "E835.0.68", {"start": v(28.39, 52.08) * mm, "mid": v(28.45, 52.16) * mm, "end": v(28.52, 52.23) * mm});
            skLineSegment(sketch, "E835.0.69", {"start": v(28.52, 52.23) * mm, "end": v(28.67, 52.39) * mm});
            skLineSegment(sketch, "E835.0.70", {"start": v(28.67, 52.39) * mm, "end": v(28.85, 52.57) * mm});
            skLineSegment(sketch, "E835.0.71", {"start": v(28.85, 52.57) * mm, "end": v(29.05, 52.78) * mm});
            skArc(sketch, "E835.0.72", {"start": v(29.05, 52.78) * mm, "mid": v(29.17, 52.9) * mm, "end": v(29.28, 53.01) * mm});
            skLineSegment(sketch, "E835.0.73", {"start": v(29.28, 53.01) * mm, "end": v(30.43, 54.15) * mm});
            skLineSegment(sketch, "E835.0.74", {"start": v(30.43, 54.15) * mm, "end": v(30.43, 60) * mm});
            skSolve(sketch);
        }
        {
            var Q0;
            Q0=makeQuery(id+"F12.imprint","IMPRINT",FACE,{"disambiguationData":[TD([[makeQuery(id+"F12.imprint","IMPRINT",EDGE,{"derivedFrom":sQuery(id+"F12.wireOp",EDGE,"E829.0.0")}),1.0]])]});
            extrude(context, id + "F13", {"entities" : qUnion([Q0]), "depth" : (getVariable(context, 'Thickness')) * mm, "offsetDistance" : 25 * mm});
        }
    });
